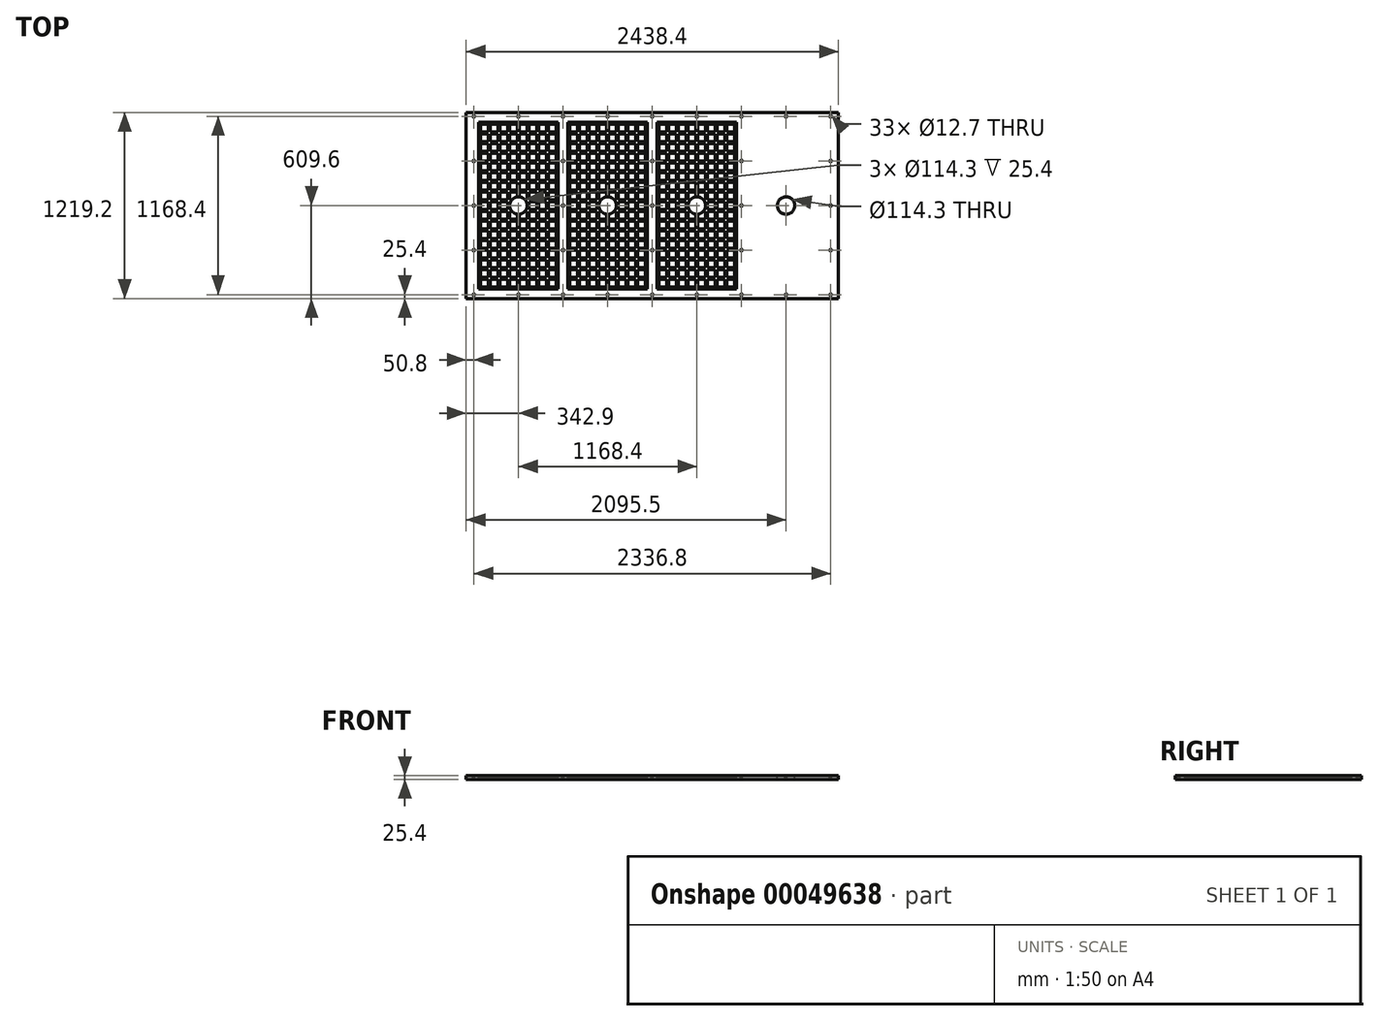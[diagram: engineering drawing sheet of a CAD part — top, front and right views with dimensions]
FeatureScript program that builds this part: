
annotation { "Feature Type Name" : "Feature", "Feature Type Description" : "" }
export const myFeature = defineFeature(function(context is Context, id is Id, definition is map)
    precondition{}
    {
        {
            var Q0;
            Q0=qCreatedBy(makeId("Top.planeOp"),FACE);
            var sketch = newSketch(context, id + "F0", { "sketchPlane" : qUnion([Q0])});
            skLineSegment(sketch, "E0", {"start": v(0, 0) * mm, "end": v(0, 1219.2) * mm});
            skLineSegment(sketch, "E1", {"start": v(0, 1219.2) * mm, "end": v(2438.4, 1219.2) * mm});
            skLineSegment(sketch, "E2", {"start": v(2438.4, 1219.2) * mm, "end": v(2438.4, 0) * mm});
            skLineSegment(sketch, "E3", {"start": v(2438.4, 0) * mm, "end": v(0, 0) * mm});
            skSolve(sketch);
        }
        {
            var Q0;
            Q0=makeQuery(id+"F0.imprint","IMPRINT",FACE,{"disambiguationData":[TD([[makeQuery(id+"F0.imprint","IMPRINT",EDGE,{"derivedFrom":sQuery(id+"F0.wireOp",EDGE,"E0")}),-1.0]])]});
            extrude(context, id + "F1", {"entities" : qUnion([Q0]), "depth" : 25.4 * mm});
        }
        {
            var Q0;
            Q0=makeQuery(id+"F1.opExtrude","CAP_FACE",FACE,{"disambiguationData":[OSD([sQuery(id+"F0.wireOp",EDGE,"E0"),sQuery(id+"F0.wireOp",EDGE,"E1"),sQuery(id+"F0.wireOp",EDGE,"E2"),sQuery(id+"F0.wireOp",EDGE,"E3")])],"isStart":false});
            var sketch = newSketch(context, id + "F2", { "sketchPlane" : qUnion([Q0])});
            skCircle(sketch, "E4", {"center": v(50.8, 1193.8) * mm, "radius": 6.35 * mm});
            skLineSegment(sketch, "E5", {"start": v(50.8, 1193.8) * mm, "end": v(635, 1193.8) * mm, "construction": true});
            skLineSegment(sketch, "E6", {"start": v(635, 1193.8) * mm, "end": v(1219.2, 1193.8) * mm, "construction": true});
            skLineSegment(sketch, "E7", {"start": v(1219.2, 1193.8) * mm, "end": v(1803.4, 1193.8) * mm, "construction": true});
            skLineSegment(sketch, "E8", {"start": v(1803.4, 1193.8) * mm, "end": v(2387.6, 1193.8) * mm, "construction": true});
            skLineSegment(sketch, "E9", {"start": v(2387.6, 1193.8) * mm, "end": v(2387.6, 609.6) * mm, "construction": true});
            skLineSegment(sketch, "E10", {"start": v(2387.6, 609.6) * mm, "end": v(2387.6, 25.4) * mm, "construction": true});
            skLineSegment(sketch, "E11", {"start": v(50.8, 1193.8) * mm, "end": v(0, 1193.8) * mm, "construction": true});
            skLineSegment(sketch, "E12", {"start": v(2387.6, 1193.8) * mm, "end": v(2438.4, 1193.8) * mm, "construction": true});
            skLineSegment(sketch, "E13", {"start": v(2387.6, 1193.8) * mm, "end": v(2387.6, 1219.2) * mm, "construction": true});
            skLineSegment(sketch, "E14", {"start": v(2387.6, 25.4) * mm, "end": v(2387.6, 0) * mm, "construction": true});
            skLineSegment(sketch, "E15", {"start": v(635, 1193.8) * mm, "end": v(635, 609.6) * mm, "construction": true});
            skLineSegment(sketch, "E16", {"start": v(1219.2, 1193.8) * mm, "end": v(1219.2, 609.6) * mm, "construction": true});
            skLineSegment(sketch, "E17", {"start": v(1803.4, 1193.8) * mm, "end": v(1803.4, 609.6) * mm, "construction": true});
            skCircle(sketch, "E18", {"center": v(635, 1193.8) * mm, "radius": 6.35 * mm});
            skCircle(sketch, "E19", {"center": v(342.9, 1193.8) * mm, "radius": 6.35 * mm});
            skCircle(sketch, "E20", {"center": v(927.1, 1193.8) * mm, "radius": 6.35 * mm});
            skCircle(sketch, "E21", {"center": v(1219.2, 1193.8) * mm, "radius": 6.35 * mm});
            skCircle(sketch, "E22", {"center": v(1511.3, 1193.8) * mm, "radius": 6.35 * mm});
            skCircle(sketch, "E23", {"center": v(1803.4, 1193.8) * mm, "radius": 6.35 * mm});
            skCircle(sketch, "E24", {"center": v(2095.5, 1193.8) * mm, "radius": 6.35 * mm});
            skCircle(sketch, "E25", {"center": v(2387.6, 1193.8) * mm, "radius": 6.35 * mm});
            skCircle(sketch, "E26", {"center": v(1803.4, 901.7) * mm, "radius": 6.35 * mm});
            skCircle(sketch, "E27", {"center": v(1219.2, 901.7) * mm, "radius": 6.35 * mm});
            skCircle(sketch, "E28", {"center": v(635, 901.7) * mm, "radius": 6.35 * mm});
            skCircle(sketch, "E29", {"center": v(2387.6, 901.7) * mm, "radius": 6.35 * mm});
            skLineSegment(sketch, "E30", {"start": v(50.8, 1193.8) * mm, "end": v(50.8, 609.6) * mm, "construction": true});
            skLineSegment(sketch, "E31", {"start": v(50.8, 609.6) * mm, "end": v(635, 609.6) * mm, "construction": true});
            skLineSegment(sketch, "E32", {"start": v(1219.2, 609.6) * mm, "end": v(635, 609.6) * mm, "construction": true});
            skLineSegment(sketch, "E33", {"start": v(1219.2, 609.6) * mm, "end": v(1803.4, 609.6) * mm, "construction": true});
            skLineSegment(sketch, "E34", {"start": v(1803.4, 609.6) * mm, "end": v(2387.6, 609.6) * mm, "construction": true});
            skCircle(sketch, "E35", {"center": v(342.9, 609.6) * mm, "radius": 57.15 * mm});
            skCircle(sketch, "E36", {"center": v(927.1, 609.6) * mm, "radius": 57.15 * mm});
            skCircle(sketch, "E37", {"center": v(1511.3, 609.6) * mm, "radius": 57.15 * mm});
            skCircle(sketch, "E38", {"center": v(2095.5, 609.6) * mm, "radius": 57.15 * mm});
            skCircle(sketch, "E39", {"center": v(50.8, 901.7) * mm, "radius": 6.35 * mm});
            skCircle(sketch, "E40.MirrorC", {"center": v(50.8, 317.5) * mm, "radius": 6.35 * mm});
            skCircle(sketch, "E41.MirrorC", {"center": v(50.8, 25.4) * mm, "radius": 6.35 * mm});
            skCircle(sketch, "E42.MirrorC", {"center": v(342.9, 25.4) * mm, "radius": 6.35 * mm});
            skCircle(sketch, "E43.MirrorC", {"center": v(635, 317.5) * mm, "radius": 6.35 * mm});
            skCircle(sketch, "E44.MirrorC", {"center": v(635, 25.4) * mm, "radius": 6.35 * mm});
            skCircle(sketch, "E45.MirrorC", {"center": v(927.1, 25.4) * mm, "radius": 6.35 * mm});
            skCircle(sketch, "E46.MirrorC", {"center": v(1219.2, 25.4) * mm, "radius": 6.35 * mm});
            skCircle(sketch, "E47.MirrorC", {"center": v(1219.2, 317.5) * mm, "radius": 6.35 * mm});
            skCircle(sketch, "E48.MirrorC", {"center": v(1511.3, 25.4) * mm, "radius": 6.35 * mm});
            skCircle(sketch, "E49.MirrorC", {"center": v(1803.4, 25.4) * mm, "radius": 6.35 * mm});
            skCircle(sketch, "E50.MirrorC", {"center": v(1803.4, 317.5) * mm, "radius": 6.35 * mm});
            skCircle(sketch, "E51.MirrorC", {"center": v(2095.5, 25.4) * mm, "radius": 6.35 * mm});
            skCircle(sketch, "E52.MirrorC", {"center": v(2387.6, 25.4) * mm, "radius": 6.35 * mm});
            skCircle(sketch, "E53.MirrorC", {"center": v(2387.6, 317.5) * mm, "radius": 6.35 * mm});
            skCircle(sketch, "E54", {"center": v(50.8, 609.6) * mm, "radius": 6.35 * mm});
            skCircle(sketch, "E55", {"center": v(635, 609.6) * mm, "radius": 6.35 * mm});
            skCircle(sketch, "E56", {"center": v(1219.2, 609.6) * mm, "radius": 6.35 * mm});
            skCircle(sketch, "E57", {"center": v(1803.4, 609.6) * mm, "radius": 6.35 * mm});
            skCircle(sketch, "E58", {"center": v(2387.6, 609.6) * mm, "radius": 6.35 * mm});
            skSolve(sketch);
        }
        {
            var Q0;
            Q0 = qSketchRegion(id + "F2", true);
            extrude(context, id + "F3", {"entities" : qUnion([Q0]), "operationType" : NewBodyOperationType.REMOVE, "endBound" : BoundingType.UP_TO_NEXT, "oppositeDirection" : true, "depth" : 25.4 * mm});
        }
        {
            var Q0;
            Q0=makeQuery(id+"F1.opExtrude","CAP_FACE",FACE,{"disambiguationData":[OSD([sQuery(id+"F0.wireOp",EDGE,"E0"),sQuery(id+"F0.wireOp",EDGE,"E1"),sQuery(id+"F0.wireOp",EDGE,"E2"),sQuery(id+"F0.wireOp",EDGE,"E3")])],"isStart":false});
            var sketch = newSketch(context, id + "F4", { "sketchPlane" : qUnion([Q0])});
            skLineSegment(sketch, "E59", {"start": v(342.9, 1193.8) * mm, "end": v(342.9, 1155.7) * mm, "construction": true});
            skLineSegment(sketch, "E60", {"start": v(603.25, 609.6) * mm, "end": v(635, 609.6) * mm, "construction": true});
            skLineSegment(sketch, "E61", {"start": v(342.9, 25.4) * mm, "end": v(342.9, 63.5) * mm, "construction": true});
            skLineSegment(sketch, "E62", {"start": v(50.8, 609.6) * mm, "end": v(82.55, 609.6) * mm, "construction": true});
            skLineSegment(sketch, "E63.rect.bottom", {"start": v(603.25, 1155.7) * mm, "end": v(82.55, 1155.7) * mm});
            skLineSegment(sketch, "E63.rect.top", {"start": v(603.25, 63.5) * mm, "end": v(82.55, 63.5) * mm});
            skLineSegment(sketch, "E63.rect.left", {"start": v(603.25, 1155.7) * mm, "end": v(603.25, 63.5) * mm});
            skLineSegment(sketch, "E63.rect.right", {"start": v(82.55, 1155.7) * mm, "end": v(82.55, 63.5) * mm});
            skPoint(sketch, "E63.rect.middle", {"position": v(342.9, 609.6) * mm});
            skLineSegment(sketch, "E64.rect.bottom", {"start": v(146.05, 1092.2) * mm, "end": v(95.25, 1092.2) * mm});
            skLineSegment(sketch, "E64.rect.top", {"start": v(146.05, 1143) * mm, "end": v(95.25, 1143) * mm});
            skLineSegment(sketch, "E64.rect.left", {"start": v(146.05, 1092.2) * mm, "end": v(146.05, 1143) * mm});
            skLineSegment(sketch, "E64.rect.right", {"start": v(95.25, 1092.2) * mm, "end": v(95.25, 1143) * mm});
            skPoint(sketch, "E64.rect.middle", {"position": v(120.65, 1117.6) * mm});
            skLineSegment(sketch, "E65.0.1.0", {"start": v(146.05, 1028.7) * mm, "end": v(146.05, 1079.5) * mm});
            skLineSegment(sketch, "E65.0.1.1", {"start": v(146.05, 1079.5) * mm, "end": v(95.25, 1079.5) * mm});
            skLineSegment(sketch, "E65.0.1.2", {"start": v(95.25, 1028.7) * mm, "end": v(95.25, 1079.5) * mm});
            skLineSegment(sketch, "E65.0.1.3", {"start": v(146.05, 1028.7) * mm, "end": v(95.25, 1028.7) * mm});
            skLineSegment(sketch, "E65.0.2.0", {"start": v(146.05, 965.2) * mm, "end": v(146.05, 1016) * mm});
            skLineSegment(sketch, "E65.0.2.1", {"start": v(146.05, 1016) * mm, "end": v(95.25, 1016) * mm});
            skLineSegment(sketch, "E65.0.2.2", {"start": v(95.25, 965.2) * mm, "end": v(95.25, 1016) * mm});
            skLineSegment(sketch, "E65.0.2.3", {"start": v(146.05, 965.2) * mm, "end": v(95.25, 965.2) * mm});
            skLineSegment(sketch, "E65.0.3.0", {"start": v(146.05, 901.7) * mm, "end": v(146.05, 952.5) * mm});
            skLineSegment(sketch, "E65.0.3.1", {"start": v(146.05, 952.5) * mm, "end": v(95.25, 952.5) * mm});
            skLineSegment(sketch, "E65.0.3.2", {"start": v(95.25, 901.7) * mm, "end": v(95.25, 952.5) * mm});
            skLineSegment(sketch, "E65.0.3.3", {"start": v(146.05, 901.7) * mm, "end": v(95.25, 901.7) * mm});
            skLineSegment(sketch, "E65.0.4.0", {"start": v(146.05, 838.2) * mm, "end": v(146.05, 889) * mm});
            skLineSegment(sketch, "E65.0.4.1", {"start": v(146.05, 889) * mm, "end": v(95.25, 889) * mm});
            skLineSegment(sketch, "E65.0.4.2", {"start": v(95.25, 838.2) * mm, "end": v(95.25, 889) * mm});
            skLineSegment(sketch, "E65.0.4.3", {"start": v(146.05, 838.2) * mm, "end": v(95.25, 838.2) * mm});
            skLineSegment(sketch, "E65.0.5.0", {"start": v(146.05, 774.7) * mm, "end": v(146.05, 825.5) * mm});
            skLineSegment(sketch, "E65.0.5.1", {"start": v(146.05, 825.5) * mm, "end": v(95.25, 825.5) * mm});
            skLineSegment(sketch, "E65.0.5.2", {"start": v(95.25, 774.7) * mm, "end": v(95.25, 825.5) * mm});
            skLineSegment(sketch, "E65.0.5.3", {"start": v(146.05, 774.7) * mm, "end": v(95.25, 774.7) * mm});
            skLineSegment(sketch, "E65.0.6.0", {"start": v(146.05, 711.2) * mm, "end": v(146.05, 762) * mm});
            skLineSegment(sketch, "E65.0.6.1", {"start": v(146.05, 762) * mm, "end": v(95.25, 762) * mm});
            skLineSegment(sketch, "E65.0.6.2", {"start": v(95.25, 711.2) * mm, "end": v(95.25, 762) * mm});
            skLineSegment(sketch, "E65.0.6.3", {"start": v(146.05, 711.2) * mm, "end": v(95.25, 711.2) * mm});
            skLineSegment(sketch, "E65.0.7.0", {"start": v(146.05, 647.7) * mm, "end": v(146.05, 698.5) * mm});
            skLineSegment(sketch, "E65.0.7.1", {"start": v(146.05, 698.5) * mm, "end": v(95.25, 698.5) * mm});
            skLineSegment(sketch, "E65.0.7.2", {"start": v(95.25, 647.7) * mm, "end": v(95.25, 698.5) * mm});
            skLineSegment(sketch, "E65.0.7.3", {"start": v(146.05, 647.7) * mm, "end": v(95.25, 647.7) * mm});
            skLineSegment(sketch, "E65.0.8.0", {"start": v(146.05, 584.2) * mm, "end": v(146.05, 635) * mm});
            skLineSegment(sketch, "E65.0.8.1", {"start": v(146.05, 635) * mm, "end": v(95.25, 635) * mm});
            skLineSegment(sketch, "E65.0.8.2", {"start": v(95.25, 584.2) * mm, "end": v(95.25, 635) * mm});
            skLineSegment(sketch, "E65.0.8.3", {"start": v(146.05, 584.2) * mm, "end": v(95.25, 584.2) * mm});
            skLineSegment(sketch, "E65.0.9.0", {"start": v(146.05, 520.7) * mm, "end": v(146.05, 571.5) * mm});
            skLineSegment(sketch, "E65.0.9.1", {"start": v(146.05, 571.5) * mm, "end": v(95.25, 571.5) * mm});
            skLineSegment(sketch, "E65.0.9.2", {"start": v(95.25, 520.7) * mm, "end": v(95.25, 571.5) * mm});
            skLineSegment(sketch, "E65.0.9.3", {"start": v(146.05, 520.7) * mm, "end": v(95.25, 520.7) * mm});
            skLineSegment(sketch, "E65.0.10.0", {"start": v(146.05, 457.2) * mm, "end": v(146.05, 508) * mm});
            skLineSegment(sketch, "E65.0.10.1", {"start": v(146.05, 508) * mm, "end": v(95.25, 508) * mm});
            skLineSegment(sketch, "E65.0.10.2", {"start": v(95.25, 457.2) * mm, "end": v(95.25, 508) * mm});
            skLineSegment(sketch, "E65.0.10.3", {"start": v(146.05, 457.2) * mm, "end": v(95.25, 457.2) * mm});
            skLineSegment(sketch, "E65.0.11.0", {"start": v(146.05, 393.7) * mm, "end": v(146.05, 444.5) * mm});
            skLineSegment(sketch, "E65.0.11.1", {"start": v(146.05, 444.5) * mm, "end": v(95.25, 444.5) * mm});
            skLineSegment(sketch, "E65.0.11.2", {"start": v(95.25, 393.7) * mm, "end": v(95.25, 444.5) * mm});
            skLineSegment(sketch, "E65.0.11.3", {"start": v(146.05, 393.7) * mm, "end": v(95.25, 393.7) * mm});
            skLineSegment(sketch, "E65.0.12.0", {"start": v(146.05, 330.2) * mm, "end": v(146.05, 381) * mm});
            skLineSegment(sketch, "E65.0.12.1", {"start": v(146.05, 381) * mm, "end": v(95.25, 381) * mm});
            skLineSegment(sketch, "E65.0.12.2", {"start": v(95.25, 330.2) * mm, "end": v(95.25, 381) * mm});
            skLineSegment(sketch, "E65.0.12.3", {"start": v(146.05, 330.2) * mm, "end": v(95.25, 330.2) * mm});
            skLineSegment(sketch, "E65.0.13.0", {"start": v(146.05, 266.7) * mm, "end": v(146.05, 317.5) * mm});
            skLineSegment(sketch, "E65.0.13.1", {"start": v(146.05, 317.5) * mm, "end": v(95.25, 317.5) * mm});
            skLineSegment(sketch, "E65.0.13.2", {"start": v(95.25, 266.7) * mm, "end": v(95.25, 317.5) * mm});
            skLineSegment(sketch, "E65.0.13.3", {"start": v(146.05, 266.7) * mm, "end": v(95.25, 266.7) * mm});
            skLineSegment(sketch, "E65.0.14.0", {"start": v(146.05, 203.2) * mm, "end": v(146.05, 254) * mm});
            skLineSegment(sketch, "E65.0.14.1", {"start": v(146.05, 254) * mm, "end": v(95.25, 254) * mm});
            skLineSegment(sketch, "E65.0.14.2", {"start": v(95.25, 203.2) * mm, "end": v(95.25, 254) * mm});
            skLineSegment(sketch, "E65.0.14.3", {"start": v(146.05, 203.2) * mm, "end": v(95.25, 203.2) * mm});
            skLineSegment(sketch, "E65.0.15.0", {"start": v(146.05, 139.7) * mm, "end": v(146.05, 190.5) * mm});
            skLineSegment(sketch, "E65.0.15.1", {"start": v(146.05, 190.5) * mm, "end": v(95.25, 190.5) * mm});
            skLineSegment(sketch, "E65.0.15.2", {"start": v(95.25, 139.7) * mm, "end": v(95.25, 190.5) * mm});
            skLineSegment(sketch, "E65.0.15.3", {"start": v(146.05, 139.7) * mm, "end": v(95.25, 139.7) * mm});
            skLineSegment(sketch, "E65.1.0.0", {"start": v(209.55, 1092.2) * mm, "end": v(209.55, 1143) * mm});
            skLineSegment(sketch, "E65.1.0.1", {"start": v(209.55, 1143) * mm, "end": v(158.75, 1143) * mm});
            skLineSegment(sketch, "E65.1.0.2", {"start": v(158.75, 1092.2) * mm, "end": v(158.75, 1143) * mm});
            skLineSegment(sketch, "E65.1.0.3", {"start": v(209.55, 1092.2) * mm, "end": v(158.75, 1092.2) * mm});
            skLineSegment(sketch, "E65.1.1.0", {"start": v(209.55, 1028.7) * mm, "end": v(209.55, 1079.5) * mm});
            skLineSegment(sketch, "E65.1.1.1", {"start": v(209.55, 1079.5) * mm, "end": v(158.75, 1079.5) * mm});
            skLineSegment(sketch, "E65.1.1.2", {"start": v(158.75, 1028.7) * mm, "end": v(158.75, 1079.5) * mm});
            skLineSegment(sketch, "E65.1.1.3", {"start": v(209.55, 1028.7) * mm, "end": v(158.75, 1028.7) * mm});
            skLineSegment(sketch, "E65.1.2.0", {"start": v(209.55, 965.2) * mm, "end": v(209.55, 1016) * mm});
            skLineSegment(sketch, "E65.1.2.1", {"start": v(209.55, 1016) * mm, "end": v(158.75, 1016) * mm});
            skLineSegment(sketch, "E65.1.2.2", {"start": v(158.75, 965.2) * mm, "end": v(158.75, 1016) * mm});
            skLineSegment(sketch, "E65.1.2.3", {"start": v(209.55, 965.2) * mm, "end": v(158.75, 965.2) * mm});
            skLineSegment(sketch, "E65.1.3.0", {"start": v(209.55, 901.7) * mm, "end": v(209.55, 952.5) * mm});
            skLineSegment(sketch, "E65.1.3.1", {"start": v(209.55, 952.5) * mm, "end": v(158.75, 952.5) * mm});
            skLineSegment(sketch, "E65.1.3.2", {"start": v(158.75, 901.7) * mm, "end": v(158.75, 952.5) * mm});
            skLineSegment(sketch, "E65.1.3.3", {"start": v(209.55, 901.7) * mm, "end": v(158.75, 901.7) * mm});
            skLineSegment(sketch, "E65.1.4.0", {"start": v(209.55, 838.2) * mm, "end": v(209.55, 889) * mm});
            skLineSegment(sketch, "E65.1.4.1", {"start": v(209.55, 889) * mm, "end": v(158.75, 889) * mm});
            skLineSegment(sketch, "E65.1.4.2", {"start": v(158.75, 838.2) * mm, "end": v(158.75, 889) * mm});
            skLineSegment(sketch, "E65.1.4.3", {"start": v(209.55, 838.2) * mm, "end": v(158.75, 838.2) * mm});
            skLineSegment(sketch, "E65.1.5.0", {"start": v(209.55, 774.7) * mm, "end": v(209.55, 825.5) * mm});
            skLineSegment(sketch, "E65.1.5.1", {"start": v(209.55, 825.5) * mm, "end": v(158.75, 825.5) * mm});
            skLineSegment(sketch, "E65.1.5.2", {"start": v(158.75, 774.7) * mm, "end": v(158.75, 825.5) * mm});
            skLineSegment(sketch, "E65.1.5.3", {"start": v(209.55, 774.7) * mm, "end": v(158.75, 774.7) * mm});
            skLineSegment(sketch, "E65.1.6.0", {"start": v(209.55, 711.2) * mm, "end": v(209.55, 762) * mm});
            skLineSegment(sketch, "E65.1.6.1", {"start": v(209.55, 762) * mm, "end": v(158.75, 762) * mm});
            skLineSegment(sketch, "E65.1.6.2", {"start": v(158.75, 711.2) * mm, "end": v(158.75, 762) * mm});
            skLineSegment(sketch, "E65.1.6.3", {"start": v(209.55, 711.2) * mm, "end": v(158.75, 711.2) * mm});
            skLineSegment(sketch, "E65.1.7.0", {"start": v(209.55, 647.7) * mm, "end": v(209.55, 698.5) * mm});
            skLineSegment(sketch, "E65.1.7.1", {"start": v(209.55, 698.5) * mm, "end": v(158.75, 698.5) * mm});
            skLineSegment(sketch, "E65.1.7.2", {"start": v(158.75, 647.7) * mm, "end": v(158.75, 698.5) * mm});
            skLineSegment(sketch, "E65.1.7.3", {"start": v(209.55, 647.7) * mm, "end": v(158.75, 647.7) * mm});
            skLineSegment(sketch, "E65.1.8.0", {"start": v(209.55, 584.2) * mm, "end": v(209.55, 635) * mm});
            skLineSegment(sketch, "E65.1.8.1", {"start": v(209.55, 635) * mm, "end": v(158.75, 635) * mm});
            skLineSegment(sketch, "E65.1.8.2", {"start": v(158.75, 584.2) * mm, "end": v(158.75, 635) * mm});
            skLineSegment(sketch, "E65.1.8.3", {"start": v(209.55, 584.2) * mm, "end": v(158.75, 584.2) * mm});
            skLineSegment(sketch, "E65.1.9.0", {"start": v(209.55, 520.7) * mm, "end": v(209.55, 571.5) * mm});
            skLineSegment(sketch, "E65.1.9.1", {"start": v(209.55, 571.5) * mm, "end": v(158.75, 571.5) * mm});
            skLineSegment(sketch, "E65.1.9.2", {"start": v(158.75, 520.7) * mm, "end": v(158.75, 571.5) * mm});
            skLineSegment(sketch, "E65.1.9.3", {"start": v(209.55, 520.7) * mm, "end": v(158.75, 520.7) * mm});
            skLineSegment(sketch, "E65.1.10.0", {"start": v(209.55, 457.2) * mm, "end": v(209.55, 508) * mm});
            skLineSegment(sketch, "E65.1.10.1", {"start": v(209.55, 508) * mm, "end": v(158.75, 508) * mm});
            skLineSegment(sketch, "E65.1.10.2", {"start": v(158.75, 457.2) * mm, "end": v(158.75, 508) * mm});
            skLineSegment(sketch, "E65.1.10.3", {"start": v(209.55, 457.2) * mm, "end": v(158.75, 457.2) * mm});
            skLineSegment(sketch, "E65.1.11.0", {"start": v(209.55, 393.7) * mm, "end": v(209.55, 444.5) * mm});
            skLineSegment(sketch, "E65.1.11.1", {"start": v(209.55, 444.5) * mm, "end": v(158.75, 444.5) * mm});
            skLineSegment(sketch, "E65.1.11.2", {"start": v(158.75, 393.7) * mm, "end": v(158.75, 444.5) * mm});
            skLineSegment(sketch, "E65.1.11.3", {"start": v(209.55, 393.7) * mm, "end": v(158.75, 393.7) * mm});
            skLineSegment(sketch, "E65.1.12.0", {"start": v(209.55, 330.2) * mm, "end": v(209.55, 381) * mm});
            skLineSegment(sketch, "E65.1.12.1", {"start": v(209.55, 381) * mm, "end": v(158.75, 381) * mm});
            skLineSegment(sketch, "E65.1.12.2", {"start": v(158.75, 330.2) * mm, "end": v(158.75, 381) * mm});
            skLineSegment(sketch, "E65.1.12.3", {"start": v(209.55, 330.2) * mm, "end": v(158.75, 330.2) * mm});
            skLineSegment(sketch, "E65.1.13.0", {"start": v(209.55, 266.7) * mm, "end": v(209.55, 317.5) * mm});
            skLineSegment(sketch, "E65.1.13.1", {"start": v(209.55, 317.5) * mm, "end": v(158.75, 317.5) * mm});
            skLineSegment(sketch, "E65.1.13.2", {"start": v(158.75, 266.7) * mm, "end": v(158.75, 317.5) * mm});
            skLineSegment(sketch, "E65.1.13.3", {"start": v(209.55, 266.7) * mm, "end": v(158.75, 266.7) * mm});
            skLineSegment(sketch, "E65.1.14.0", {"start": v(209.55, 203.2) * mm, "end": v(209.55, 254) * mm});
            skLineSegment(sketch, "E65.1.14.1", {"start": v(209.55, 254) * mm, "end": v(158.75, 254) * mm});
            skLineSegment(sketch, "E65.1.14.2", {"start": v(158.75, 203.2) * mm, "end": v(158.75, 254) * mm});
            skLineSegment(sketch, "E65.1.14.3", {"start": v(209.55, 203.2) * mm, "end": v(158.75, 203.2) * mm});
            skLineSegment(sketch, "E65.1.15.0", {"start": v(209.55, 139.7) * mm, "end": v(209.55, 190.5) * mm});
            skLineSegment(sketch, "E65.1.15.1", {"start": v(209.55, 190.5) * mm, "end": v(158.75, 190.5) * mm});
            skLineSegment(sketch, "E65.1.15.2", {"start": v(158.75, 139.7) * mm, "end": v(158.75, 190.5) * mm});
            skLineSegment(sketch, "E65.1.15.3", {"start": v(209.55, 139.7) * mm, "end": v(158.75, 139.7) * mm});
            skLineSegment(sketch, "E65.2.0.0", {"start": v(273.05, 1092.2) * mm, "end": v(273.05, 1143) * mm});
            skLineSegment(sketch, "E65.2.0.1", {"start": v(273.05, 1143) * mm, "end": v(222.25, 1143) * mm});
            skLineSegment(sketch, "E65.2.0.2", {"start": v(222.25, 1092.2) * mm, "end": v(222.25, 1143) * mm});
            skLineSegment(sketch, "E65.2.0.3", {"start": v(273.05, 1092.2) * mm, "end": v(222.25, 1092.2) * mm});
            skLineSegment(sketch, "E65.2.1.0", {"start": v(273.05, 1028.7) * mm, "end": v(273.05, 1079.5) * mm});
            skLineSegment(sketch, "E65.2.1.1", {"start": v(273.05, 1079.5) * mm, "end": v(222.25, 1079.5) * mm});
            skLineSegment(sketch, "E65.2.1.2", {"start": v(222.25, 1028.7) * mm, "end": v(222.25, 1079.5) * mm});
            skLineSegment(sketch, "E65.2.1.3", {"start": v(273.05, 1028.7) * mm, "end": v(222.25, 1028.7) * mm});
            skLineSegment(sketch, "E65.2.2.0", {"start": v(273.05, 965.2) * mm, "end": v(273.05, 1016) * mm});
            skLineSegment(sketch, "E65.2.2.1", {"start": v(273.05, 1016) * mm, "end": v(222.25, 1016) * mm});
            skLineSegment(sketch, "E65.2.2.2", {"start": v(222.25, 965.2) * mm, "end": v(222.25, 1016) * mm});
            skLineSegment(sketch, "E65.2.2.3", {"start": v(273.05, 965.2) * mm, "end": v(222.25, 965.2) * mm});
            skLineSegment(sketch, "E65.2.3.0", {"start": v(273.05, 901.7) * mm, "end": v(273.05, 952.5) * mm});
            skLineSegment(sketch, "E65.2.3.1", {"start": v(273.05, 952.5) * mm, "end": v(222.25, 952.5) * mm});
            skLineSegment(sketch, "E65.2.3.2", {"start": v(222.25, 901.7) * mm, "end": v(222.25, 952.5) * mm});
            skLineSegment(sketch, "E65.2.3.3", {"start": v(273.05, 901.7) * mm, "end": v(222.25, 901.7) * mm});
            skLineSegment(sketch, "E65.2.4.0", {"start": v(273.05, 838.2) * mm, "end": v(273.05, 889) * mm});
            skLineSegment(sketch, "E65.2.4.1", {"start": v(273.05, 889) * mm, "end": v(222.25, 889) * mm});
            skLineSegment(sketch, "E65.2.4.2", {"start": v(222.25, 838.2) * mm, "end": v(222.25, 889) * mm});
            skLineSegment(sketch, "E65.2.4.3", {"start": v(273.05, 838.2) * mm, "end": v(222.25, 838.2) * mm});
            skLineSegment(sketch, "E65.2.5.0", {"start": v(273.05, 774.7) * mm, "end": v(273.05, 825.5) * mm});
            skLineSegment(sketch, "E65.2.5.1", {"start": v(273.05, 825.5) * mm, "end": v(222.25, 825.5) * mm});
            skLineSegment(sketch, "E65.2.5.2", {"start": v(222.25, 774.7) * mm, "end": v(222.25, 825.5) * mm});
            skLineSegment(sketch, "E65.2.5.3", {"start": v(273.05, 774.7) * mm, "end": v(222.25, 774.7) * mm});
            skLineSegment(sketch, "E65.2.6.0", {"start": v(273.05, 711.2) * mm, "end": v(273.05, 762) * mm});
            skLineSegment(sketch, "E65.2.6.1", {"start": v(273.05, 762) * mm, "end": v(222.25, 762) * mm});
            skLineSegment(sketch, "E65.2.6.2", {"start": v(222.25, 711.2) * mm, "end": v(222.25, 762) * mm});
            skLineSegment(sketch, "E65.2.6.3", {"start": v(273.05, 711.2) * mm, "end": v(222.25, 711.2) * mm});
            skLineSegment(sketch, "E65.2.7.0", {"start": v(273.05, 647.7) * mm, "end": v(273.05, 698.5) * mm});
            skLineSegment(sketch, "E65.2.7.1", {"start": v(273.05, 698.5) * mm, "end": v(222.25, 698.5) * mm});
            skLineSegment(sketch, "E65.2.7.2", {"start": v(222.25, 647.7) * mm, "end": v(222.25, 698.5) * mm});
            skLineSegment(sketch, "E65.2.7.3", {"start": v(273.05, 647.7) * mm, "end": v(222.25, 647.7) * mm});
            skLineSegment(sketch, "E65.2.8.0", {"start": v(273.05, 584.2) * mm, "end": v(273.05, 635) * mm});
            skLineSegment(sketch, "E65.2.8.1", {"start": v(273.05, 635) * mm, "end": v(222.25, 635) * mm});
            skLineSegment(sketch, "E65.2.8.2", {"start": v(222.25, 584.2) * mm, "end": v(222.25, 635) * mm});
            skLineSegment(sketch, "E65.2.8.3", {"start": v(273.05, 584.2) * mm, "end": v(222.25, 584.2) * mm});
            skLineSegment(sketch, "E65.2.9.0", {"start": v(273.05, 520.7) * mm, "end": v(273.05, 571.5) * mm});
            skLineSegment(sketch, "E65.2.9.1", {"start": v(273.05, 571.5) * mm, "end": v(222.25, 571.5) * mm});
            skLineSegment(sketch, "E65.2.9.2", {"start": v(222.25, 520.7) * mm, "end": v(222.25, 571.5) * mm});
            skLineSegment(sketch, "E65.2.9.3", {"start": v(273.05, 520.7) * mm, "end": v(222.25, 520.7) * mm});
            skLineSegment(sketch, "E65.2.10.0", {"start": v(273.05, 457.2) * mm, "end": v(273.05, 508) * mm});
            skLineSegment(sketch, "E65.2.10.1", {"start": v(273.05, 508) * mm, "end": v(222.25, 508) * mm});
            skLineSegment(sketch, "E65.2.10.2", {"start": v(222.25, 457.2) * mm, "end": v(222.25, 508) * mm});
            skLineSegment(sketch, "E65.2.10.3", {"start": v(273.05, 457.2) * mm, "end": v(222.25, 457.2) * mm});
            skLineSegment(sketch, "E65.2.11.0", {"start": v(273.05, 393.7) * mm, "end": v(273.05, 444.5) * mm});
            skLineSegment(sketch, "E65.2.11.1", {"start": v(273.05, 444.5) * mm, "end": v(222.25, 444.5) * mm});
            skLineSegment(sketch, "E65.2.11.2", {"start": v(222.25, 393.7) * mm, "end": v(222.25, 444.5) * mm});
            skLineSegment(sketch, "E65.2.11.3", {"start": v(273.05, 393.7) * mm, "end": v(222.25, 393.7) * mm});
            skLineSegment(sketch, "E65.2.12.0", {"start": v(273.05, 330.2) * mm, "end": v(273.05, 381) * mm});
            skLineSegment(sketch, "E65.2.12.1", {"start": v(273.05, 381) * mm, "end": v(222.25, 381) * mm});
            skLineSegment(sketch, "E65.2.12.2", {"start": v(222.25, 330.2) * mm, "end": v(222.25, 381) * mm});
            skLineSegment(sketch, "E65.2.12.3", {"start": v(273.05, 330.2) * mm, "end": v(222.25, 330.2) * mm});
            skLineSegment(sketch, "E65.2.13.0", {"start": v(273.05, 266.7) * mm, "end": v(273.05, 317.5) * mm});
            skLineSegment(sketch, "E65.2.13.1", {"start": v(273.05, 317.5) * mm, "end": v(222.25, 317.5) * mm});
            skLineSegment(sketch, "E65.2.13.2", {"start": v(222.25, 266.7) * mm, "end": v(222.25, 317.5) * mm});
            skLineSegment(sketch, "E65.2.13.3", {"start": v(273.05, 266.7) * mm, "end": v(222.25, 266.7) * mm});
            skLineSegment(sketch, "E65.2.14.0", {"start": v(273.05, 203.2) * mm, "end": v(273.05, 254) * mm});
            skLineSegment(sketch, "E65.2.14.1", {"start": v(273.05, 254) * mm, "end": v(222.25, 254) * mm});
            skLineSegment(sketch, "E65.2.14.2", {"start": v(222.25, 203.2) * mm, "end": v(222.25, 254) * mm});
            skLineSegment(sketch, "E65.2.14.3", {"start": v(273.05, 203.2) * mm, "end": v(222.25, 203.2) * mm});
            skLineSegment(sketch, "E65.2.15.0", {"start": v(273.05, 139.7) * mm, "end": v(273.05, 190.5) * mm});
            skLineSegment(sketch, "E65.2.15.1", {"start": v(273.05, 190.5) * mm, "end": v(222.25, 190.5) * mm});
            skLineSegment(sketch, "E65.2.15.2", {"start": v(222.25, 139.7) * mm, "end": v(222.25, 190.5) * mm});
            skLineSegment(sketch, "E65.2.15.3", {"start": v(273.05, 139.7) * mm, "end": v(222.25, 139.7) * mm});
            skLineSegment(sketch, "E65.3.0.0", {"start": v(336.54, 1092.2) * mm, "end": v(336.54, 1143) * mm});
            skLineSegment(sketch, "E65.3.0.1", {"start": v(336.54, 1143) * mm, "end": v(285.74, 1143) * mm});
            skLineSegment(sketch, "E65.3.0.2", {"start": v(285.74, 1092.2) * mm, "end": v(285.74, 1143) * mm});
            skLineSegment(sketch, "E65.3.0.3", {"start": v(336.54, 1092.2) * mm, "end": v(285.74, 1092.2) * mm});
            skLineSegment(sketch, "E65.3.1.0", {"start": v(336.54, 1028.7) * mm, "end": v(336.54, 1079.5) * mm});
            skLineSegment(sketch, "E65.3.1.1", {"start": v(336.54, 1079.5) * mm, "end": v(285.74, 1079.5) * mm});
            skLineSegment(sketch, "E65.3.1.2", {"start": v(285.74, 1028.7) * mm, "end": v(285.74, 1079.5) * mm});
            skLineSegment(sketch, "E65.3.1.3", {"start": v(336.54, 1028.7) * mm, "end": v(285.74, 1028.7) * mm});
            skLineSegment(sketch, "E65.3.2.0", {"start": v(336.54, 965.2) * mm, "end": v(336.54, 1016) * mm});
            skLineSegment(sketch, "E65.3.2.1", {"start": v(336.54, 1016) * mm, "end": v(285.74, 1016) * mm});
            skLineSegment(sketch, "E65.3.2.2", {"start": v(285.74, 965.2) * mm, "end": v(285.74, 1016) * mm});
            skLineSegment(sketch, "E65.3.2.3", {"start": v(336.54, 965.2) * mm, "end": v(285.74, 965.2) * mm});
            skLineSegment(sketch, "E65.3.3.0", {"start": v(336.54, 901.7) * mm, "end": v(336.54, 952.5) * mm});
            skLineSegment(sketch, "E65.3.3.1", {"start": v(336.54, 952.5) * mm, "end": v(285.74, 952.5) * mm});
            skLineSegment(sketch, "E65.3.3.2", {"start": v(285.74, 901.7) * mm, "end": v(285.74, 952.5) * mm});
            skLineSegment(sketch, "E65.3.3.3", {"start": v(336.54, 901.7) * mm, "end": v(285.74, 901.7) * mm});
            skLineSegment(sketch, "E65.3.4.0", {"start": v(336.54, 838.2) * mm, "end": v(336.54, 889) * mm});
            skLineSegment(sketch, "E65.3.4.1", {"start": v(336.54, 889) * mm, "end": v(285.74, 889) * mm});
            skLineSegment(sketch, "E65.3.4.2", {"start": v(285.74, 838.2) * mm, "end": v(285.74, 889) * mm});
            skLineSegment(sketch, "E65.3.4.3", {"start": v(336.54, 838.2) * mm, "end": v(285.74, 838.2) * mm});
            skLineSegment(sketch, "E65.3.5.0", {"start": v(336.54, 774.7) * mm, "end": v(336.54, 825.5) * mm});
            skLineSegment(sketch, "E65.3.5.1", {"start": v(336.54, 825.5) * mm, "end": v(285.74, 825.5) * mm});
            skLineSegment(sketch, "E65.3.5.2", {"start": v(285.74, 774.7) * mm, "end": v(285.74, 825.5) * mm});
            skLineSegment(sketch, "E65.3.5.3", {"start": v(336.54, 774.7) * mm, "end": v(285.74, 774.7) * mm});
            skLineSegment(sketch, "E65.3.6.0", {"start": v(336.54, 711.2) * mm, "end": v(336.54, 762) * mm});
            skLineSegment(sketch, "E65.3.6.1", {"start": v(336.54, 762) * mm, "end": v(285.74, 762) * mm});
            skLineSegment(sketch, "E65.3.6.2", {"start": v(285.74, 711.2) * mm, "end": v(285.74, 762) * mm});
            skLineSegment(sketch, "E65.3.6.3", {"start": v(336.54, 711.2) * mm, "end": v(285.74, 711.2) * mm});
            skLineSegment(sketch, "E65.3.7.0", {"start": v(336.54, 647.7) * mm, "end": v(336.54, 698.5) * mm});
            skLineSegment(sketch, "E65.3.7.1", {"start": v(336.54, 698.5) * mm, "end": v(285.74, 698.5) * mm});
            skLineSegment(sketch, "E65.3.7.2", {"start": v(285.74, 647.7) * mm, "end": v(285.74, 698.5) * mm});
            skLineSegment(sketch, "E65.3.7.3", {"start": v(336.54, 647.7) * mm, "end": v(285.74, 647.7) * mm});
            skLineSegment(sketch, "E65.3.8.0", {"start": v(336.54, 584.2) * mm, "end": v(336.54, 635) * mm});
            skLineSegment(sketch, "E65.3.8.1", {"start": v(336.54, 635) * mm, "end": v(285.74, 635) * mm});
            skLineSegment(sketch, "E65.3.8.2", {"start": v(285.74, 584.2) * mm, "end": v(285.74, 635) * mm});
            skLineSegment(sketch, "E65.3.8.3", {"start": v(336.54, 584.2) * mm, "end": v(285.74, 584.2) * mm});
            skLineSegment(sketch, "E65.3.9.0", {"start": v(336.54, 520.7) * mm, "end": v(336.54, 571.5) * mm});
            skLineSegment(sketch, "E65.3.9.1", {"start": v(336.54, 571.5) * mm, "end": v(285.74, 571.5) * mm});
            skLineSegment(sketch, "E65.3.9.2", {"start": v(285.74, 520.7) * mm, "end": v(285.74, 571.5) * mm});
            skLineSegment(sketch, "E65.3.9.3", {"start": v(336.54, 520.7) * mm, "end": v(285.74, 520.7) * mm});
            skLineSegment(sketch, "E65.3.10.0", {"start": v(336.54, 457.2) * mm, "end": v(336.54, 508) * mm});
            skLineSegment(sketch, "E65.3.10.1", {"start": v(336.54, 508) * mm, "end": v(285.74, 508) * mm});
            skLineSegment(sketch, "E65.3.10.2", {"start": v(285.74, 457.2) * mm, "end": v(285.74, 508) * mm});
            skLineSegment(sketch, "E65.3.10.3", {"start": v(336.54, 457.2) * mm, "end": v(285.74, 457.2) * mm});
            skLineSegment(sketch, "E65.3.11.0", {"start": v(336.54, 393.7) * mm, "end": v(336.54, 444.5) * mm});
            skLineSegment(sketch, "E65.3.11.1", {"start": v(336.54, 444.5) * mm, "end": v(285.74, 444.5) * mm});
            skLineSegment(sketch, "E65.3.11.2", {"start": v(285.74, 393.7) * mm, "end": v(285.74, 444.5) * mm});
            skLineSegment(sketch, "E65.3.11.3", {"start": v(336.54, 393.7) * mm, "end": v(285.74, 393.7) * mm});
            skLineSegment(sketch, "E65.3.12.0", {"start": v(336.54, 330.2) * mm, "end": v(336.54, 381) * mm});
            skLineSegment(sketch, "E65.3.12.1", {"start": v(336.54, 381) * mm, "end": v(285.74, 381) * mm});
            skLineSegment(sketch, "E65.3.12.2", {"start": v(285.74, 330.2) * mm, "end": v(285.74, 381) * mm});
            skLineSegment(sketch, "E65.3.12.3", {"start": v(336.54, 330.2) * mm, "end": v(285.74, 330.2) * mm});
            skLineSegment(sketch, "E65.3.13.0", {"start": v(336.54, 266.7) * mm, "end": v(336.54, 317.5) * mm});
            skLineSegment(sketch, "E65.3.13.1", {"start": v(336.54, 317.5) * mm, "end": v(285.74, 317.5) * mm});
            skLineSegment(sketch, "E65.3.13.2", {"start": v(285.74, 266.7) * mm, "end": v(285.74, 317.5) * mm});
            skLineSegment(sketch, "E65.3.13.3", {"start": v(336.54, 266.7) * mm, "end": v(285.74, 266.7) * mm});
            skLineSegment(sketch, "E65.3.14.0", {"start": v(336.54, 203.2) * mm, "end": v(336.54, 254) * mm});
            skLineSegment(sketch, "E65.3.14.1", {"start": v(336.54, 254) * mm, "end": v(285.74, 254) * mm});
            skLineSegment(sketch, "E65.3.14.2", {"start": v(285.74, 203.2) * mm, "end": v(285.74, 254) * mm});
            skLineSegment(sketch, "E65.3.14.3", {"start": v(336.54, 203.2) * mm, "end": v(285.74, 203.2) * mm});
            skLineSegment(sketch, "E65.3.15.0", {"start": v(336.54, 139.7) * mm, "end": v(336.54, 190.5) * mm});
            skLineSegment(sketch, "E65.3.15.1", {"start": v(336.54, 190.5) * mm, "end": v(285.74, 190.5) * mm});
            skLineSegment(sketch, "E65.3.15.2", {"start": v(285.74, 139.7) * mm, "end": v(285.74, 190.5) * mm});
            skLineSegment(sketch, "E65.3.15.3", {"start": v(336.54, 139.7) * mm, "end": v(285.74, 139.7) * mm});
            skLineSegment(sketch, "E65.4.0.0", {"start": v(400.04, 1092.2) * mm, "end": v(400.04, 1143) * mm});
            skLineSegment(sketch, "E65.4.0.1", {"start": v(400.04, 1143) * mm, "end": v(349.24, 1143) * mm});
            skLineSegment(sketch, "E65.4.0.2", {"start": v(349.24, 1092.2) * mm, "end": v(349.24, 1143) * mm});
            skLineSegment(sketch, "E65.4.0.3", {"start": v(400.04, 1092.2) * mm, "end": v(349.24, 1092.2) * mm});
            skLineSegment(sketch, "E65.4.1.0", {"start": v(400.04, 1028.7) * mm, "end": v(400.04, 1079.5) * mm});
            skLineSegment(sketch, "E65.4.1.1", {"start": v(400.04, 1079.5) * mm, "end": v(349.24, 1079.5) * mm});
            skLineSegment(sketch, "E65.4.1.2", {"start": v(349.24, 1028.7) * mm, "end": v(349.24, 1079.5) * mm});
            skLineSegment(sketch, "E65.4.1.3", {"start": v(400.04, 1028.7) * mm, "end": v(349.24, 1028.7) * mm});
            skLineSegment(sketch, "E65.4.2.0", {"start": v(400.04, 965.2) * mm, "end": v(400.04, 1016) * mm});
            skLineSegment(sketch, "E65.4.2.1", {"start": v(400.04, 1016) * mm, "end": v(349.24, 1016) * mm});
            skLineSegment(sketch, "E65.4.2.2", {"start": v(349.24, 965.2) * mm, "end": v(349.24, 1016) * mm});
            skLineSegment(sketch, "E65.4.2.3", {"start": v(400.04, 965.2) * mm, "end": v(349.24, 965.2) * mm});
            skLineSegment(sketch, "E65.4.3.0", {"start": v(400.04, 901.7) * mm, "end": v(400.04, 952.5) * mm});
            skLineSegment(sketch, "E65.4.3.1", {"start": v(400.04, 952.5) * mm, "end": v(349.24, 952.5) * mm});
            skLineSegment(sketch, "E65.4.3.2", {"start": v(349.24, 901.7) * mm, "end": v(349.24, 952.5) * mm});
            skLineSegment(sketch, "E65.4.3.3", {"start": v(400.04, 901.7) * mm, "end": v(349.24, 901.7) * mm});
            skLineSegment(sketch, "E65.4.4.0", {"start": v(400.04, 838.2) * mm, "end": v(400.04, 889) * mm});
            skLineSegment(sketch, "E65.4.4.1", {"start": v(400.04, 889) * mm, "end": v(349.24, 889) * mm});
            skLineSegment(sketch, "E65.4.4.2", {"start": v(349.24, 838.2) * mm, "end": v(349.24, 889) * mm});
            skLineSegment(sketch, "E65.4.4.3", {"start": v(400.04, 838.2) * mm, "end": v(349.24, 838.2) * mm});
            skLineSegment(sketch, "E65.4.5.0", {"start": v(400.04, 774.7) * mm, "end": v(400.04, 825.5) * mm});
            skLineSegment(sketch, "E65.4.5.1", {"start": v(400.04, 825.5) * mm, "end": v(349.24, 825.5) * mm});
            skLineSegment(sketch, "E65.4.5.2", {"start": v(349.24, 774.7) * mm, "end": v(349.24, 825.5) * mm});
            skLineSegment(sketch, "E65.4.5.3", {"start": v(400.04, 774.7) * mm, "end": v(349.24, 774.7) * mm});
            skLineSegment(sketch, "E65.4.6.0", {"start": v(400.04, 711.2) * mm, "end": v(400.04, 762) * mm});
            skLineSegment(sketch, "E65.4.6.1", {"start": v(400.04, 762) * mm, "end": v(349.24, 762) * mm});
            skLineSegment(sketch, "E65.4.6.2", {"start": v(349.24, 711.2) * mm, "end": v(349.24, 762) * mm});
            skLineSegment(sketch, "E65.4.6.3", {"start": v(400.04, 711.2) * mm, "end": v(349.24, 711.2) * mm});
            skLineSegment(sketch, "E65.4.7.0", {"start": v(400.04, 647.7) * mm, "end": v(400.04, 698.5) * mm});
            skLineSegment(sketch, "E65.4.7.1", {"start": v(400.04, 698.5) * mm, "end": v(349.24, 698.5) * mm});
            skLineSegment(sketch, "E65.4.7.2", {"start": v(349.24, 647.7) * mm, "end": v(349.24, 698.5) * mm});
            skLineSegment(sketch, "E65.4.7.3", {"start": v(400.04, 647.7) * mm, "end": v(349.24, 647.7) * mm});
            skLineSegment(sketch, "E65.4.8.0", {"start": v(400.04, 584.2) * mm, "end": v(400.04, 635) * mm});
            skLineSegment(sketch, "E65.4.8.1", {"start": v(400.04, 635) * mm, "end": v(349.24, 635) * mm});
            skLineSegment(sketch, "E65.4.8.2", {"start": v(349.24, 584.2) * mm, "end": v(349.24, 635) * mm});
            skLineSegment(sketch, "E65.4.8.3", {"start": v(400.04, 584.2) * mm, "end": v(349.24, 584.2) * mm});
            skLineSegment(sketch, "E65.4.9.0", {"start": v(400.04, 520.7) * mm, "end": v(400.04, 571.5) * mm});
            skLineSegment(sketch, "E65.4.9.1", {"start": v(400.04, 571.5) * mm, "end": v(349.24, 571.5) * mm});
            skLineSegment(sketch, "E65.4.9.2", {"start": v(349.24, 520.7) * mm, "end": v(349.24, 571.5) * mm});
            skLineSegment(sketch, "E65.4.9.3", {"start": v(400.04, 520.7) * mm, "end": v(349.24, 520.7) * mm});
            skLineSegment(sketch, "E65.4.10.0", {"start": v(400.04, 457.2) * mm, "end": v(400.04, 508) * mm});
            skLineSegment(sketch, "E65.4.10.1", {"start": v(400.04, 508) * mm, "end": v(349.24, 508) * mm});
            skLineSegment(sketch, "E65.4.10.2", {"start": v(349.24, 457.2) * mm, "end": v(349.24, 508) * mm});
            skLineSegment(sketch, "E65.4.10.3", {"start": v(400.04, 457.2) * mm, "end": v(349.24, 457.2) * mm});
            skLineSegment(sketch, "E65.4.11.0", {"start": v(400.04, 393.7) * mm, "end": v(400.04, 444.5) * mm});
            skLineSegment(sketch, "E65.4.11.1", {"start": v(400.04, 444.5) * mm, "end": v(349.24, 444.5) * mm});
            skLineSegment(sketch, "E65.4.11.2", {"start": v(349.24, 393.7) * mm, "end": v(349.24, 444.5) * mm});
            skLineSegment(sketch, "E65.4.11.3", {"start": v(400.04, 393.7) * mm, "end": v(349.24, 393.7) * mm});
            skLineSegment(sketch, "E65.4.12.0", {"start": v(400.04, 330.2) * mm, "end": v(400.04, 381) * mm});
            skLineSegment(sketch, "E65.4.12.1", {"start": v(400.04, 381) * mm, "end": v(349.24, 381) * mm});
            skLineSegment(sketch, "E65.4.12.2", {"start": v(349.24, 330.2) * mm, "end": v(349.24, 381) * mm});
            skLineSegment(sketch, "E65.4.12.3", {"start": v(400.04, 330.2) * mm, "end": v(349.24, 330.2) * mm});
            skLineSegment(sketch, "E65.4.13.0", {"start": v(400.04, 266.7) * mm, "end": v(400.04, 317.5) * mm});
            skLineSegment(sketch, "E65.4.13.1", {"start": v(400.04, 317.5) * mm, "end": v(349.24, 317.5) * mm});
            skLineSegment(sketch, "E65.4.13.2", {"start": v(349.24, 266.7) * mm, "end": v(349.24, 317.5) * mm});
            skLineSegment(sketch, "E65.4.13.3", {"start": v(400.04, 266.7) * mm, "end": v(349.24, 266.7) * mm});
            skLineSegment(sketch, "E65.4.14.0", {"start": v(400.04, 203.2) * mm, "end": v(400.04, 254) * mm});
            skLineSegment(sketch, "E65.4.14.1", {"start": v(400.04, 254) * mm, "end": v(349.24, 254) * mm});
            skLineSegment(sketch, "E65.4.14.2", {"start": v(349.24, 203.2) * mm, "end": v(349.24, 254) * mm});
            skLineSegment(sketch, "E65.4.14.3", {"start": v(400.04, 203.2) * mm, "end": v(349.24, 203.2) * mm});
            skLineSegment(sketch, "E65.4.15.0", {"start": v(400.04, 139.7) * mm, "end": v(400.04, 190.5) * mm});
            skLineSegment(sketch, "E65.4.15.1", {"start": v(400.04, 190.5) * mm, "end": v(349.24, 190.5) * mm});
            skLineSegment(sketch, "E65.4.15.2", {"start": v(349.24, 139.7) * mm, "end": v(349.24, 190.5) * mm});
            skLineSegment(sketch, "E65.4.15.3", {"start": v(400.04, 139.7) * mm, "end": v(349.24, 139.7) * mm});
            skLineSegment(sketch, "E65.5.0.0", {"start": v(463.54, 1092.2) * mm, "end": v(463.54, 1143) * mm});
            skLineSegment(sketch, "E65.5.0.1", {"start": v(463.54, 1143) * mm, "end": v(412.74, 1143) * mm});
            skLineSegment(sketch, "E65.5.0.2", {"start": v(412.74, 1092.2) * mm, "end": v(412.74, 1143) * mm});
            skLineSegment(sketch, "E65.5.0.3", {"start": v(463.54, 1092.2) * mm, "end": v(412.74, 1092.2) * mm});
            skLineSegment(sketch, "E65.5.1.0", {"start": v(463.54, 1028.7) * mm, "end": v(463.54, 1079.5) * mm});
            skLineSegment(sketch, "E65.5.1.1", {"start": v(463.54, 1079.5) * mm, "end": v(412.74, 1079.5) * mm});
            skLineSegment(sketch, "E65.5.1.2", {"start": v(412.74, 1028.7) * mm, "end": v(412.74, 1079.5) * mm});
            skLineSegment(sketch, "E65.5.1.3", {"start": v(463.54, 1028.7) * mm, "end": v(412.74, 1028.7) * mm});
            skLineSegment(sketch, "E65.5.2.0", {"start": v(463.54, 965.2) * mm, "end": v(463.54, 1016) * mm});
            skLineSegment(sketch, "E65.5.2.1", {"start": v(463.54, 1016) * mm, "end": v(412.74, 1016) * mm});
            skLineSegment(sketch, "E65.5.2.2", {"start": v(412.74, 965.2) * mm, "end": v(412.74, 1016) * mm});
            skLineSegment(sketch, "E65.5.2.3", {"start": v(463.54, 965.2) * mm, "end": v(412.74, 965.2) * mm});
            skLineSegment(sketch, "E65.5.3.0", {"start": v(463.54, 901.7) * mm, "end": v(463.54, 952.5) * mm});
            skLineSegment(sketch, "E65.5.3.1", {"start": v(463.54, 952.5) * mm, "end": v(412.74, 952.5) * mm});
            skLineSegment(sketch, "E65.5.3.2", {"start": v(412.74, 901.7) * mm, "end": v(412.74, 952.5) * mm});
            skLineSegment(sketch, "E65.5.3.3", {"start": v(463.54, 901.7) * mm, "end": v(412.74, 901.7) * mm});
            skLineSegment(sketch, "E65.5.4.0", {"start": v(463.54, 838.2) * mm, "end": v(463.54, 889) * mm});
            skLineSegment(sketch, "E65.5.4.1", {"start": v(463.54, 889) * mm, "end": v(412.74, 889) * mm});
            skLineSegment(sketch, "E65.5.4.2", {"start": v(412.74, 838.2) * mm, "end": v(412.74, 889) * mm});
            skLineSegment(sketch, "E65.5.4.3", {"start": v(463.54, 838.2) * mm, "end": v(412.74, 838.2) * mm});
            skLineSegment(sketch, "E65.5.5.0", {"start": v(463.54, 774.7) * mm, "end": v(463.54, 825.5) * mm});
            skLineSegment(sketch, "E65.5.5.1", {"start": v(463.54, 825.5) * mm, "end": v(412.74, 825.5) * mm});
            skLineSegment(sketch, "E65.5.5.2", {"start": v(412.74, 774.7) * mm, "end": v(412.74, 825.5) * mm});
            skLineSegment(sketch, "E65.5.5.3", {"start": v(463.54, 774.7) * mm, "end": v(412.74, 774.7) * mm});
            skLineSegment(sketch, "E65.5.6.0", {"start": v(463.54, 711.2) * mm, "end": v(463.54, 762) * mm});
            skLineSegment(sketch, "E65.5.6.1", {"start": v(463.54, 762) * mm, "end": v(412.74, 762) * mm});
            skLineSegment(sketch, "E65.5.6.2", {"start": v(412.74, 711.2) * mm, "end": v(412.74, 762) * mm});
            skLineSegment(sketch, "E65.5.6.3", {"start": v(463.54, 711.2) * mm, "end": v(412.74, 711.2) * mm});
            skLineSegment(sketch, "E65.5.7.0", {"start": v(463.54, 647.7) * mm, "end": v(463.54, 698.5) * mm});
            skLineSegment(sketch, "E65.5.7.1", {"start": v(463.54, 698.5) * mm, "end": v(412.74, 698.5) * mm});
            skLineSegment(sketch, "E65.5.7.2", {"start": v(412.74, 647.7) * mm, "end": v(412.74, 698.5) * mm});
            skLineSegment(sketch, "E65.5.7.3", {"start": v(463.54, 647.7) * mm, "end": v(412.74, 647.7) * mm});
            skLineSegment(sketch, "E65.5.8.0", {"start": v(463.54, 584.2) * mm, "end": v(463.54, 635) * mm});
            skLineSegment(sketch, "E65.5.8.1", {"start": v(463.54, 635) * mm, "end": v(412.74, 635) * mm});
            skLineSegment(sketch, "E65.5.8.2", {"start": v(412.74, 584.2) * mm, "end": v(412.74, 635) * mm});
            skLineSegment(sketch, "E65.5.8.3", {"start": v(463.54, 584.2) * mm, "end": v(412.74, 584.2) * mm});
            skLineSegment(sketch, "E65.5.9.0", {"start": v(463.54, 520.7) * mm, "end": v(463.54, 571.5) * mm});
            skLineSegment(sketch, "E65.5.9.1", {"start": v(463.54, 571.5) * mm, "end": v(412.74, 571.5) * mm});
            skLineSegment(sketch, "E65.5.9.2", {"start": v(412.74, 520.7) * mm, "end": v(412.74, 571.5) * mm});
            skLineSegment(sketch, "E65.5.9.3", {"start": v(463.54, 520.7) * mm, "end": v(412.74, 520.7) * mm});
            skLineSegment(sketch, "E65.5.10.0", {"start": v(463.54, 457.2) * mm, "end": v(463.54, 508) * mm});
            skLineSegment(sketch, "E65.5.10.1", {"start": v(463.54, 508) * mm, "end": v(412.74, 508) * mm});
            skLineSegment(sketch, "E65.5.10.2", {"start": v(412.74, 457.2) * mm, "end": v(412.74, 508) * mm});
            skLineSegment(sketch, "E65.5.10.3", {"start": v(463.54, 457.2) * mm, "end": v(412.74, 457.2) * mm});
            skLineSegment(sketch, "E65.5.11.0", {"start": v(463.54, 393.7) * mm, "end": v(463.54, 444.5) * mm});
            skLineSegment(sketch, "E65.5.11.1", {"start": v(463.54, 444.5) * mm, "end": v(412.74, 444.5) * mm});
            skLineSegment(sketch, "E65.5.11.2", {"start": v(412.74, 393.7) * mm, "end": v(412.74, 444.5) * mm});
            skLineSegment(sketch, "E65.5.11.3", {"start": v(463.54, 393.7) * mm, "end": v(412.74, 393.7) * mm});
            skLineSegment(sketch, "E65.5.12.0", {"start": v(463.54, 330.2) * mm, "end": v(463.54, 381) * mm});
            skLineSegment(sketch, "E65.5.12.1", {"start": v(463.54, 381) * mm, "end": v(412.74, 381) * mm});
            skLineSegment(sketch, "E65.5.12.2", {"start": v(412.74, 330.2) * mm, "end": v(412.74, 381) * mm});
            skLineSegment(sketch, "E65.5.12.3", {"start": v(463.54, 330.2) * mm, "end": v(412.74, 330.2) * mm});
            skLineSegment(sketch, "E65.5.13.0", {"start": v(463.54, 266.7) * mm, "end": v(463.54, 317.5) * mm});
            skLineSegment(sketch, "E65.5.13.1", {"start": v(463.54, 317.5) * mm, "end": v(412.74, 317.5) * mm});
            skLineSegment(sketch, "E65.5.13.2", {"start": v(412.74, 266.7) * mm, "end": v(412.74, 317.5) * mm});
            skLineSegment(sketch, "E65.5.13.3", {"start": v(463.54, 266.7) * mm, "end": v(412.74, 266.7) * mm});
            skLineSegment(sketch, "E65.5.14.0", {"start": v(463.54, 203.2) * mm, "end": v(463.54, 254) * mm});
            skLineSegment(sketch, "E65.5.14.1", {"start": v(463.54, 254) * mm, "end": v(412.74, 254) * mm});
            skLineSegment(sketch, "E65.5.14.2", {"start": v(412.74, 203.2) * mm, "end": v(412.74, 254) * mm});
            skLineSegment(sketch, "E65.5.14.3", {"start": v(463.54, 203.2) * mm, "end": v(412.74, 203.2) * mm});
            skLineSegment(sketch, "E65.5.15.0", {"start": v(463.54, 139.7) * mm, "end": v(463.54, 190.5) * mm});
            skLineSegment(sketch, "E65.5.15.1", {"start": v(463.54, 190.5) * mm, "end": v(412.74, 190.5) * mm});
            skLineSegment(sketch, "E65.5.15.2", {"start": v(412.74, 139.7) * mm, "end": v(412.74, 190.5) * mm});
            skLineSegment(sketch, "E65.5.15.3", {"start": v(463.54, 139.7) * mm, "end": v(412.74, 139.7) * mm});
            skLineSegment(sketch, "E65.6.0.0", {"start": v(527.04, 1092.2) * mm, "end": v(527.04, 1143) * mm});
            skLineSegment(sketch, "E65.6.0.1", {"start": v(527.04, 1143) * mm, "end": v(476.24, 1143) * mm});
            skLineSegment(sketch, "E65.6.0.2", {"start": v(476.24, 1092.2) * mm, "end": v(476.24, 1143) * mm});
            skLineSegment(sketch, "E65.6.0.3", {"start": v(527.04, 1092.2) * mm, "end": v(476.24, 1092.2) * mm});
            skLineSegment(sketch, "E65.6.1.0", {"start": v(527.04, 1028.7) * mm, "end": v(527.04, 1079.5) * mm});
            skLineSegment(sketch, "E65.6.1.1", {"start": v(527.04, 1079.5) * mm, "end": v(476.24, 1079.5) * mm});
            skLineSegment(sketch, "E65.6.1.2", {"start": v(476.24, 1028.7) * mm, "end": v(476.24, 1079.5) * mm});
            skLineSegment(sketch, "E65.6.1.3", {"start": v(527.04, 1028.7) * mm, "end": v(476.24, 1028.7) * mm});
            skLineSegment(sketch, "E65.6.2.0", {"start": v(527.04, 965.2) * mm, "end": v(527.04, 1016) * mm});
            skLineSegment(sketch, "E65.6.2.1", {"start": v(527.04, 1016) * mm, "end": v(476.24, 1016) * mm});
            skLineSegment(sketch, "E65.6.2.2", {"start": v(476.24, 965.2) * mm, "end": v(476.24, 1016) * mm});
            skLineSegment(sketch, "E65.6.2.3", {"start": v(527.04, 965.2) * mm, "end": v(476.24, 965.2) * mm});
            skLineSegment(sketch, "E65.6.3.0", {"start": v(527.04, 901.7) * mm, "end": v(527.04, 952.5) * mm});
            skLineSegment(sketch, "E65.6.3.1", {"start": v(527.04, 952.5) * mm, "end": v(476.24, 952.5) * mm});
            skLineSegment(sketch, "E65.6.3.2", {"start": v(476.24, 901.7) * mm, "end": v(476.24, 952.5) * mm});
            skLineSegment(sketch, "E65.6.3.3", {"start": v(527.04, 901.7) * mm, "end": v(476.24, 901.7) * mm});
            skLineSegment(sketch, "E65.6.4.0", {"start": v(527.04, 838.2) * mm, "end": v(527.04, 889) * mm});
            skLineSegment(sketch, "E65.6.4.1", {"start": v(527.04, 889) * mm, "end": v(476.24, 889) * mm});
            skLineSegment(sketch, "E65.6.4.2", {"start": v(476.24, 838.2) * mm, "end": v(476.24, 889) * mm});
            skLineSegment(sketch, "E65.6.4.3", {"start": v(527.04, 838.2) * mm, "end": v(476.24, 838.2) * mm});
            skLineSegment(sketch, "E65.6.5.0", {"start": v(527.04, 774.7) * mm, "end": v(527.04, 825.5) * mm});
            skLineSegment(sketch, "E65.6.5.1", {"start": v(527.04, 825.5) * mm, "end": v(476.24, 825.5) * mm});
            skLineSegment(sketch, "E65.6.5.2", {"start": v(476.24, 774.7) * mm, "end": v(476.24, 825.5) * mm});
            skLineSegment(sketch, "E65.6.5.3", {"start": v(527.04, 774.7) * mm, "end": v(476.24, 774.7) * mm});
            skLineSegment(sketch, "E65.6.6.0", {"start": v(527.04, 711.2) * mm, "end": v(527.04, 762) * mm});
            skLineSegment(sketch, "E65.6.6.1", {"start": v(527.04, 762) * mm, "end": v(476.24, 762) * mm});
            skLineSegment(sketch, "E65.6.6.2", {"start": v(476.24, 711.2) * mm, "end": v(476.24, 762) * mm});
            skLineSegment(sketch, "E65.6.6.3", {"start": v(527.04, 711.2) * mm, "end": v(476.24, 711.2) * mm});
            skLineSegment(sketch, "E65.6.7.0", {"start": v(527.04, 647.7) * mm, "end": v(527.04, 698.5) * mm});
            skLineSegment(sketch, "E65.6.7.1", {"start": v(527.04, 698.5) * mm, "end": v(476.24, 698.5) * mm});
            skLineSegment(sketch, "E65.6.7.2", {"start": v(476.24, 647.7) * mm, "end": v(476.24, 698.5) * mm});
            skLineSegment(sketch, "E65.6.7.3", {"start": v(527.04, 647.7) * mm, "end": v(476.24, 647.7) * mm});
            skLineSegment(sketch, "E65.6.8.0", {"start": v(527.04, 584.2) * mm, "end": v(527.04, 635) * mm});
            skLineSegment(sketch, "E65.6.8.1", {"start": v(527.04, 635) * mm, "end": v(476.24, 635) * mm});
            skLineSegment(sketch, "E65.6.8.2", {"start": v(476.24, 584.2) * mm, "end": v(476.24, 635) * mm});
            skLineSegment(sketch, "E65.6.8.3", {"start": v(527.04, 584.2) * mm, "end": v(476.24, 584.2) * mm});
            skLineSegment(sketch, "E65.6.9.0", {"start": v(527.04, 520.7) * mm, "end": v(527.04, 571.5) * mm});
            skLineSegment(sketch, "E65.6.9.1", {"start": v(527.04, 571.5) * mm, "end": v(476.24, 571.5) * mm});
            skLineSegment(sketch, "E65.6.9.2", {"start": v(476.24, 520.7) * mm, "end": v(476.24, 571.5) * mm});
            skLineSegment(sketch, "E65.6.9.3", {"start": v(527.04, 520.7) * mm, "end": v(476.24, 520.7) * mm});
            skLineSegment(sketch, "E65.6.10.0", {"start": v(527.04, 457.2) * mm, "end": v(527.04, 508) * mm});
            skLineSegment(sketch, "E65.6.10.1", {"start": v(527.04, 508) * mm, "end": v(476.24, 508) * mm});
            skLineSegment(sketch, "E65.6.10.2", {"start": v(476.24, 457.2) * mm, "end": v(476.24, 508) * mm});
            skLineSegment(sketch, "E65.6.10.3", {"start": v(527.04, 457.2) * mm, "end": v(476.24, 457.2) * mm});
            skLineSegment(sketch, "E65.6.11.0", {"start": v(527.04, 393.7) * mm, "end": v(527.04, 444.5) * mm});
            skLineSegment(sketch, "E65.6.11.1", {"start": v(527.04, 444.5) * mm, "end": v(476.24, 444.5) * mm});
            skLineSegment(sketch, "E65.6.11.2", {"start": v(476.24, 393.7) * mm, "end": v(476.24, 444.5) * mm});
            skLineSegment(sketch, "E65.6.11.3", {"start": v(527.04, 393.7) * mm, "end": v(476.24, 393.7) * mm});
            skLineSegment(sketch, "E65.6.12.0", {"start": v(527.04, 330.2) * mm, "end": v(527.04, 381) * mm});
            skLineSegment(sketch, "E65.6.12.1", {"start": v(527.04, 381) * mm, "end": v(476.24, 381) * mm});
            skLineSegment(sketch, "E65.6.12.2", {"start": v(476.24, 330.2) * mm, "end": v(476.24, 381) * mm});
            skLineSegment(sketch, "E65.6.12.3", {"start": v(527.04, 330.2) * mm, "end": v(476.24, 330.2) * mm});
            skLineSegment(sketch, "E65.6.13.0", {"start": v(527.04, 266.7) * mm, "end": v(527.04, 317.5) * mm});
            skLineSegment(sketch, "E65.6.13.1", {"start": v(527.04, 317.5) * mm, "end": v(476.24, 317.5) * mm});
            skLineSegment(sketch, "E65.6.13.2", {"start": v(476.24, 266.7) * mm, "end": v(476.24, 317.5) * mm});
            skLineSegment(sketch, "E65.6.13.3", {"start": v(527.04, 266.7) * mm, "end": v(476.24, 266.7) * mm});
            skLineSegment(sketch, "E65.6.14.0", {"start": v(527.04, 203.2) * mm, "end": v(527.04, 254) * mm});
            skLineSegment(sketch, "E65.6.14.1", {"start": v(527.04, 254) * mm, "end": v(476.24, 254) * mm});
            skLineSegment(sketch, "E65.6.14.2", {"start": v(476.24, 203.2) * mm, "end": v(476.24, 254) * mm});
            skLineSegment(sketch, "E65.6.14.3", {"start": v(527.04, 203.2) * mm, "end": v(476.24, 203.2) * mm});
            skLineSegment(sketch, "E65.6.15.0", {"start": v(527.04, 139.7) * mm, "end": v(527.04, 190.5) * mm});
            skLineSegment(sketch, "E65.6.15.1", {"start": v(527.04, 190.5) * mm, "end": v(476.24, 190.5) * mm});
            skLineSegment(sketch, "E65.6.15.2", {"start": v(476.24, 139.7) * mm, "end": v(476.24, 190.5) * mm});
            skLineSegment(sketch, "E65.6.15.3", {"start": v(527.04, 139.7) * mm, "end": v(476.24, 139.7) * mm});
            skLineSegment(sketch, "E65.7.0.0", {"start": v(590.53, 1092.2) * mm, "end": v(590.53, 1143) * mm});
            skLineSegment(sketch, "E65.7.0.1", {"start": v(590.53, 1143) * mm, "end": v(539.73, 1143) * mm});
            skLineSegment(sketch, "E65.7.0.2", {"start": v(539.73, 1092.2) * mm, "end": v(539.73, 1143) * mm});
            skLineSegment(sketch, "E65.7.0.3", {"start": v(590.53, 1092.2) * mm, "end": v(539.73, 1092.2) * mm});
            skLineSegment(sketch, "E65.7.1.0", {"start": v(590.53, 1028.7) * mm, "end": v(590.53, 1079.5) * mm});
            skLineSegment(sketch, "E65.7.1.1", {"start": v(590.53, 1079.5) * mm, "end": v(539.73, 1079.5) * mm});
            skLineSegment(sketch, "E65.7.1.2", {"start": v(539.73, 1028.7) * mm, "end": v(539.73, 1079.5) * mm});
            skLineSegment(sketch, "E65.7.1.3", {"start": v(590.53, 1028.7) * mm, "end": v(539.73, 1028.7) * mm});
            skLineSegment(sketch, "E65.7.2.0", {"start": v(590.53, 965.2) * mm, "end": v(590.53, 1016) * mm});
            skLineSegment(sketch, "E65.7.2.1", {"start": v(590.53, 1016) * mm, "end": v(539.73, 1016) * mm});
            skLineSegment(sketch, "E65.7.2.2", {"start": v(539.73, 965.2) * mm, "end": v(539.73, 1016) * mm});
            skLineSegment(sketch, "E65.7.2.3", {"start": v(590.53, 965.2) * mm, "end": v(539.73, 965.2) * mm});
            skLineSegment(sketch, "E65.7.3.0", {"start": v(590.53, 901.7) * mm, "end": v(590.53, 952.5) * mm});
            skLineSegment(sketch, "E65.7.3.1", {"start": v(590.53, 952.5) * mm, "end": v(539.73, 952.5) * mm});
            skLineSegment(sketch, "E65.7.3.2", {"start": v(539.73, 901.7) * mm, "end": v(539.73, 952.5) * mm});
            skLineSegment(sketch, "E65.7.3.3", {"start": v(590.53, 901.7) * mm, "end": v(539.73, 901.7) * mm});
            skLineSegment(sketch, "E65.7.4.0", {"start": v(590.53, 838.2) * mm, "end": v(590.53, 889) * mm});
            skLineSegment(sketch, "E65.7.4.1", {"start": v(590.53, 889) * mm, "end": v(539.73, 889) * mm});
            skLineSegment(sketch, "E65.7.4.2", {"start": v(539.73, 838.2) * mm, "end": v(539.73, 889) * mm});
            skLineSegment(sketch, "E65.7.4.3", {"start": v(590.53, 838.2) * mm, "end": v(539.73, 838.2) * mm});
            skLineSegment(sketch, "E65.7.5.0", {"start": v(590.53, 774.7) * mm, "end": v(590.53, 825.5) * mm});
            skLineSegment(sketch, "E65.7.5.1", {"start": v(590.53, 825.5) * mm, "end": v(539.73, 825.5) * mm});
            skLineSegment(sketch, "E65.7.5.2", {"start": v(539.73, 774.7) * mm, "end": v(539.73, 825.5) * mm});
            skLineSegment(sketch, "E65.7.5.3", {"start": v(590.53, 774.7) * mm, "end": v(539.73, 774.7) * mm});
            skLineSegment(sketch, "E65.7.6.0", {"start": v(590.53, 711.2) * mm, "end": v(590.53, 762) * mm});
            skLineSegment(sketch, "E65.7.6.1", {"start": v(590.53, 762) * mm, "end": v(539.73, 762) * mm});
            skLineSegment(sketch, "E65.7.6.2", {"start": v(539.73, 711.2) * mm, "end": v(539.73, 762) * mm});
            skLineSegment(sketch, "E65.7.6.3", {"start": v(590.53, 711.2) * mm, "end": v(539.73, 711.2) * mm});
            skLineSegment(sketch, "E65.7.7.0", {"start": v(590.53, 647.7) * mm, "end": v(590.53, 698.5) * mm});
            skLineSegment(sketch, "E65.7.7.1", {"start": v(590.53, 698.5) * mm, "end": v(539.73, 698.5) * mm});
            skLineSegment(sketch, "E65.7.7.2", {"start": v(539.73, 647.7) * mm, "end": v(539.73, 698.5) * mm});
            skLineSegment(sketch, "E65.7.7.3", {"start": v(590.53, 647.7) * mm, "end": v(539.73, 647.7) * mm});
            skLineSegment(sketch, "E65.7.8.0", {"start": v(590.53, 584.2) * mm, "end": v(590.53, 635) * mm});
            skLineSegment(sketch, "E65.7.8.1", {"start": v(590.53, 635) * mm, "end": v(539.73, 635) * mm});
            skLineSegment(sketch, "E65.7.8.2", {"start": v(539.73, 584.2) * mm, "end": v(539.73, 635) * mm});
            skLineSegment(sketch, "E65.7.8.3", {"start": v(590.53, 584.2) * mm, "end": v(539.73, 584.2) * mm});
            skLineSegment(sketch, "E65.7.9.0", {"start": v(590.53, 520.7) * mm, "end": v(590.53, 571.5) * mm});
            skLineSegment(sketch, "E65.7.9.1", {"start": v(590.53, 571.5) * mm, "end": v(539.73, 571.5) * mm});
            skLineSegment(sketch, "E65.7.9.2", {"start": v(539.73, 520.7) * mm, "end": v(539.73, 571.5) * mm});
            skLineSegment(sketch, "E65.7.9.3", {"start": v(590.53, 520.7) * mm, "end": v(539.73, 520.7) * mm});
            skLineSegment(sketch, "E65.7.10.0", {"start": v(590.53, 457.2) * mm, "end": v(590.53, 508) * mm});
            skLineSegment(sketch, "E65.7.10.1", {"start": v(590.53, 508) * mm, "end": v(539.73, 508) * mm});
            skLineSegment(sketch, "E65.7.10.2", {"start": v(539.73, 457.2) * mm, "end": v(539.73, 508) * mm});
            skLineSegment(sketch, "E65.7.10.3", {"start": v(590.53, 457.2) * mm, "end": v(539.73, 457.2) * mm});
            skLineSegment(sketch, "E65.7.11.0", {"start": v(590.53, 393.7) * mm, "end": v(590.53, 444.5) * mm});
            skLineSegment(sketch, "E65.7.11.1", {"start": v(590.53, 444.5) * mm, "end": v(539.73, 444.5) * mm});
            skLineSegment(sketch, "E65.7.11.2", {"start": v(539.73, 393.7) * mm, "end": v(539.73, 444.5) * mm});
            skLineSegment(sketch, "E65.7.11.3", {"start": v(590.53, 393.7) * mm, "end": v(539.73, 393.7) * mm});
            skLineSegment(sketch, "E65.7.12.0", {"start": v(590.53, 330.2) * mm, "end": v(590.53, 381) * mm});
            skLineSegment(sketch, "E65.7.12.1", {"start": v(590.53, 381) * mm, "end": v(539.73, 381) * mm});
            skLineSegment(sketch, "E65.7.12.2", {"start": v(539.73, 330.2) * mm, "end": v(539.73, 381) * mm});
            skLineSegment(sketch, "E65.7.12.3", {"start": v(590.53, 330.2) * mm, "end": v(539.73, 330.2) * mm});
            skLineSegment(sketch, "E65.7.13.0", {"start": v(590.53, 266.7) * mm, "end": v(590.53, 317.5) * mm});
            skLineSegment(sketch, "E65.7.13.1", {"start": v(590.53, 317.5) * mm, "end": v(539.73, 317.5) * mm});
            skLineSegment(sketch, "E65.7.13.2", {"start": v(539.73, 266.7) * mm, "end": v(539.73, 317.5) * mm});
            skLineSegment(sketch, "E65.7.13.3", {"start": v(590.53, 266.7) * mm, "end": v(539.73, 266.7) * mm});
            skLineSegment(sketch, "E65.7.14.0", {"start": v(590.53, 203.2) * mm, "end": v(590.53, 254) * mm});
            skLineSegment(sketch, "E65.7.14.1", {"start": v(590.53, 254) * mm, "end": v(539.73, 254) * mm});
            skLineSegment(sketch, "E65.7.14.2", {"start": v(539.73, 203.2) * mm, "end": v(539.73, 254) * mm});
            skLineSegment(sketch, "E65.7.14.3", {"start": v(590.53, 203.2) * mm, "end": v(539.73, 203.2) * mm});
            skLineSegment(sketch, "E65.7.15.0", {"start": v(590.53, 139.7) * mm, "end": v(590.53, 190.5) * mm});
            skLineSegment(sketch, "E65.7.15.1", {"start": v(590.53, 190.5) * mm, "end": v(539.73, 190.5) * mm});
            skLineSegment(sketch, "E65.7.15.2", {"start": v(539.73, 139.7) * mm, "end": v(539.73, 190.5) * mm});
            skLineSegment(sketch, "E65.7.15.3", {"start": v(590.53, 139.7) * mm, "end": v(539.73, 139.7) * mm});
            skLineSegment(sketch, "E65.direction1", {"start": v(109.18, 1054.37) * mm, "end": v(201.15, 1054.37) * mm, "construction": true});
            skLineSegment(sketch, "E65.direction2", {"start": v(109.18, 1054.37) * mm, "end": v(109.18, 952.93) * mm, "construction": true});
            skLineSegment(sketch, "E66.direction1", {"start": v(95.25, 266.7) * mm, "end": v(679.45, 266.7) * mm, "construction": true});
            skLineSegment(sketch, "E67.0.0.16", {"start": v(146.05, 76.2) * mm, "end": v(146.05, 127) * mm});
            skLineSegment(sketch, "E67.3.0.16", {"start": v(146.05, 127) * mm, "end": v(95.25, 127) * mm});
            skLineSegment(sketch, "E67.6.0.16", {"start": v(95.25, 76.2) * mm, "end": v(95.25, 127) * mm});
            skLineSegment(sketch, "E67.9.0.16", {"start": v(146.05, 76.2) * mm, "end": v(95.25, 76.2) * mm});
            skLineSegment(sketch, "E67.0.1.16", {"start": v(209.55, 76.2) * mm, "end": v(209.55, 127) * mm});
            skLineSegment(sketch, "E67.3.1.16", {"start": v(209.55, 127) * mm, "end": v(158.75, 127) * mm});
            skLineSegment(sketch, "E67.6.1.16", {"start": v(158.75, 76.2) * mm, "end": v(158.75, 127) * mm});
            skLineSegment(sketch, "E67.9.1.16", {"start": v(209.55, 76.2) * mm, "end": v(158.75, 76.2) * mm});
            skLineSegment(sketch, "E67.0.2.16", {"start": v(273.05, 76.2) * mm, "end": v(273.05, 127) * mm});
            skLineSegment(sketch, "E67.3.2.16", {"start": v(273.05, 127) * mm, "end": v(222.25, 127) * mm});
            skLineSegment(sketch, "E67.6.2.16", {"start": v(222.25, 76.2) * mm, "end": v(222.25, 127) * mm});
            skLineSegment(sketch, "E67.9.2.16", {"start": v(273.05, 76.2) * mm, "end": v(222.25, 76.2) * mm});
            skLineSegment(sketch, "E67.0.3.16", {"start": v(336.54, 76.2) * mm, "end": v(336.54, 127) * mm});
            skLineSegment(sketch, "E67.3.3.16", {"start": v(336.54, 127) * mm, "end": v(285.74, 127) * mm});
            skLineSegment(sketch, "E67.6.3.16", {"start": v(285.74, 76.2) * mm, "end": v(285.74, 127) * mm});
            skLineSegment(sketch, "E67.9.3.16", {"start": v(336.54, 76.2) * mm, "end": v(285.74, 76.2) * mm});
            skLineSegment(sketch, "E67.0.4.16", {"start": v(400.04, 76.2) * mm, "end": v(400.04, 127) * mm});
            skLineSegment(sketch, "E67.3.4.16", {"start": v(400.04, 127) * mm, "end": v(349.24, 127) * mm});
            skLineSegment(sketch, "E67.6.4.16", {"start": v(349.24, 76.2) * mm, "end": v(349.24, 127) * mm});
            skLineSegment(sketch, "E67.9.4.16", {"start": v(400.04, 76.2) * mm, "end": v(349.24, 76.2) * mm});
            skLineSegment(sketch, "E67.0.5.16", {"start": v(463.54, 76.2) * mm, "end": v(463.54, 127) * mm});
            skLineSegment(sketch, "E67.3.5.16", {"start": v(463.54, 127) * mm, "end": v(412.74, 127) * mm});
            skLineSegment(sketch, "E67.6.5.16", {"start": v(412.74, 76.2) * mm, "end": v(412.74, 127) * mm});
            skLineSegment(sketch, "E67.9.5.16", {"start": v(463.54, 76.2) * mm, "end": v(412.74, 76.2) * mm});
            skLineSegment(sketch, "E67.0.6.16", {"start": v(527.04, 76.2) * mm, "end": v(527.04, 127) * mm});
            skLineSegment(sketch, "E67.3.6.16", {"start": v(527.04, 127) * mm, "end": v(476.24, 127) * mm});
            skLineSegment(sketch, "E67.6.6.16", {"start": v(476.24, 76.2) * mm, "end": v(476.24, 127) * mm});
            skLineSegment(sketch, "E67.9.6.16", {"start": v(527.04, 76.2) * mm, "end": v(476.24, 76.2) * mm});
            skLineSegment(sketch, "E67.0.7.16", {"start": v(590.53, 76.2) * mm, "end": v(590.53, 127) * mm});
            skLineSegment(sketch, "E67.3.7.16", {"start": v(590.53, 127) * mm, "end": v(539.73, 127) * mm});
            skLineSegment(sketch, "E67.6.7.16", {"start": v(539.73, 76.2) * mm, "end": v(539.73, 127) * mm});
            skLineSegment(sketch, "E67.9.7.16", {"start": v(590.53, 76.2) * mm, "end": v(539.73, 76.2) * mm});
            skLineSegment(sketch, "E68.direction1", {"start": v(285.74, 127) * mm, "end": v(870.3, 127) * mm, "construction": true});
            skLineSegment(sketch, "E69.1.0.0", {"start": v(1111.24, 774.7) * mm, "end": v(1060.44, 774.7) * mm});
            skLineSegment(sketch, "E69.1.0.1", {"start": v(1111.24, 1028.7) * mm, "end": v(1060.44, 1028.7) * mm});
            skLineSegment(sketch, "E69.1.0.2", {"start": v(1047.74, 266.7) * mm, "end": v(996.94, 266.7) * mm});
            skLineSegment(sketch, "E69.1.0.3", {"start": v(1047.74, 520.7) * mm, "end": v(996.94, 520.7) * mm});
            skLineSegment(sketch, "E69.1.0.4", {"start": v(1111.24, 266.7) * mm, "end": v(1060.44, 266.7) * mm});
            skLineSegment(sketch, "E69.1.0.5", {"start": v(1111.24, 520.7) * mm, "end": v(1060.44, 520.7) * mm});
            skLineSegment(sketch, "E69.1.0.6", {"start": v(1174.73, 266.7) * mm, "end": v(1123.93, 266.7) * mm});
            skLineSegment(sketch, "E69.1.0.7", {"start": v(1174.73, 520.7) * mm, "end": v(1123.93, 520.7) * mm});
            skLineSegment(sketch, "E69.1.0.8", {"start": v(1174.73, 774.7) * mm, "end": v(1123.93, 774.7) * mm});
            skLineSegment(sketch, "E69.1.0.9", {"start": v(1174.73, 1028.7) * mm, "end": v(1123.93, 1028.7) * mm});
            skLineSegment(sketch, "E69.1.0.10", {"start": v(1047.74, 76.2) * mm, "end": v(1047.74, 127) * mm});
            skLineSegment(sketch, "E69.1.0.11", {"start": v(793.75, 76.2) * mm, "end": v(793.75, 127) * mm});
            skLineSegment(sketch, "E69.1.0.12", {"start": v(730.25, 774.7) * mm, "end": v(679.45, 774.7) * mm});
            skLineSegment(sketch, "E69.1.0.13", {"start": v(793.75, 774.7) * mm, "end": v(742.95, 774.7) * mm});
            skLineSegment(sketch, "E69.1.0.14", {"start": v(793.75, 1028.7) * mm, "end": v(742.95, 1028.7) * mm});
            skLineSegment(sketch, "E69.1.0.15", {"start": v(730.25, 266.7) * mm, "end": v(679.45, 266.7) * mm});
            skLineSegment(sketch, "E69.1.0.16", {"start": v(730.25, 520.7) * mm, "end": v(679.45, 520.7) * mm});
            skLineSegment(sketch, "E69.1.0.17", {"start": v(857.25, 774.7) * mm, "end": v(806.45, 774.7) * mm});
            skLineSegment(sketch, "E69.1.0.18", {"start": v(857.25, 1028.7) * mm, "end": v(806.45, 1028.7) * mm});
            skLineSegment(sketch, "E69.1.0.19", {"start": v(793.75, 266.7) * mm, "end": v(742.95, 266.7) * mm});
            skLineSegment(sketch, "E69.1.0.20", {"start": v(793.75, 520.7) * mm, "end": v(742.95, 520.7) * mm});
            skLineSegment(sketch, "E69.1.0.21", {"start": v(920.74, 774.7) * mm, "end": v(869.94, 774.7) * mm});
            skLineSegment(sketch, "E69.1.0.22", {"start": v(920.74, 1028.7) * mm, "end": v(869.94, 1028.7) * mm});
            skLineSegment(sketch, "E69.1.0.23", {"start": v(857.25, 266.7) * mm, "end": v(806.45, 266.7) * mm});
            skLineSegment(sketch, "E69.1.0.24", {"start": v(857.25, 520.7) * mm, "end": v(806.45, 520.7) * mm});
            skLineSegment(sketch, "E69.1.0.25", {"start": v(984.24, 774.7) * mm, "end": v(933.44, 774.7) * mm});
            skLineSegment(sketch, "E69.1.0.26", {"start": v(984.24, 1028.7) * mm, "end": v(933.44, 1028.7) * mm});
            skLineSegment(sketch, "E69.1.0.27", {"start": v(920.74, 266.7) * mm, "end": v(869.94, 266.7) * mm});
            skLineSegment(sketch, "E69.1.0.28", {"start": v(920.74, 520.7) * mm, "end": v(869.94, 520.7) * mm});
            skLineSegment(sketch, "E69.1.0.29", {"start": v(1047.74, 774.7) * mm, "end": v(996.94, 774.7) * mm});
            skLineSegment(sketch, "E69.1.0.30", {"start": v(1047.74, 1028.7) * mm, "end": v(996.94, 1028.7) * mm});
            skLineSegment(sketch, "E69.1.0.31", {"start": v(984.24, 266.7) * mm, "end": v(933.44, 266.7) * mm});
            skLineSegment(sketch, "E69.1.0.32", {"start": v(984.24, 520.7) * mm, "end": v(933.44, 520.7) * mm});
            skLineSegment(sketch, "E69.1.0.33", {"start": v(730.25, 711.2) * mm, "end": v(730.25, 762) * mm});
            skLineSegment(sketch, "E69.1.0.34", {"start": v(730.25, 965.2) * mm, "end": v(730.25, 1016) * mm});
            skLineSegment(sketch, "E69.1.0.35", {"start": v(793.75, 711.2) * mm, "end": v(793.75, 762) * mm});
            skLineSegment(sketch, "E69.1.0.36", {"start": v(793.75, 965.2) * mm, "end": v(793.75, 1016) * mm});
            skLineSegment(sketch, "E69.1.0.37", {"start": v(730.25, 203.2) * mm, "end": v(730.25, 254) * mm});
            skLineSegment(sketch, "E69.1.0.38", {"start": v(730.25, 457.2) * mm, "end": v(730.25, 508) * mm});
            skLineSegment(sketch, "E69.1.0.39", {"start": v(857.25, 711.2) * mm, "end": v(857.25, 762) * mm});
            skLineSegment(sketch, "E69.1.0.40", {"start": v(857.25, 965.2) * mm, "end": v(857.25, 1016) * mm});
            skLineSegment(sketch, "E69.1.0.41", {"start": v(793.75, 203.2) * mm, "end": v(793.75, 254) * mm});
            skLineSegment(sketch, "E69.1.0.42", {"start": v(793.75, 457.2) * mm, "end": v(793.75, 508) * mm});
            skLineSegment(sketch, "E69.1.0.43", {"start": v(920.74, 711.2) * mm, "end": v(920.74, 762) * mm});
            skLineSegment(sketch, "E69.1.0.44", {"start": v(920.74, 965.2) * mm, "end": v(920.74, 1016) * mm});
            skLineSegment(sketch, "E69.1.0.45", {"start": v(857.25, 203.2) * mm, "end": v(857.25, 254) * mm});
            skLineSegment(sketch, "E69.1.0.46", {"start": v(857.25, 457.2) * mm, "end": v(857.25, 508) * mm});
            skLineSegment(sketch, "E69.1.0.47", {"start": v(984.24, 711.2) * mm, "end": v(984.24, 762) * mm});
            skLineSegment(sketch, "E69.1.0.48", {"start": v(984.24, 965.2) * mm, "end": v(984.24, 1016) * mm});
            skLineSegment(sketch, "E69.1.0.49", {"start": v(920.74, 203.2) * mm, "end": v(920.74, 254) * mm});
            skLineSegment(sketch, "E69.1.0.50", {"start": v(920.74, 457.2) * mm, "end": v(920.74, 508) * mm});
            skLineSegment(sketch, "E69.1.0.51", {"start": v(1047.74, 711.2) * mm, "end": v(1047.74, 762) * mm});
            skLineSegment(sketch, "E69.1.0.52", {"start": v(1047.74, 965.2) * mm, "end": v(1047.74, 1016) * mm});
            skLineSegment(sketch, "E69.1.0.53", {"start": v(984.24, 203.2) * mm, "end": v(984.24, 254) * mm});
            skLineSegment(sketch, "E69.1.0.54", {"start": v(984.24, 457.2) * mm, "end": v(984.24, 508) * mm});
            skLineSegment(sketch, "E69.1.0.55", {"start": v(1111.24, 965.2) * mm, "end": v(1111.24, 1016) * mm});
            skLineSegment(sketch, "E69.1.0.56", {"start": v(1047.74, 203.2) * mm, "end": v(1047.74, 254) * mm});
            skLineSegment(sketch, "E69.1.0.57", {"start": v(1047.74, 457.2) * mm, "end": v(1047.74, 508) * mm});
            skLineSegment(sketch, "E69.1.0.58", {"start": v(1111.24, 203.2) * mm, "end": v(1111.24, 254) * mm});
            skLineSegment(sketch, "E69.1.0.59", {"start": v(1111.24, 457.2) * mm, "end": v(1111.24, 508) * mm});
            skLineSegment(sketch, "E69.1.0.60", {"start": v(1111.24, 711.2) * mm, "end": v(1111.24, 762) * mm});
            skLineSegment(sketch, "E69.1.0.61", {"start": v(1174.73, 203.2) * mm, "end": v(1174.73, 254) * mm});
            skLineSegment(sketch, "E69.1.0.62", {"start": v(1174.73, 457.2) * mm, "end": v(1174.73, 508) * mm});
            skLineSegment(sketch, "E69.1.0.63", {"start": v(1174.73, 711.2) * mm, "end": v(1174.73, 762) * mm});
            skLineSegment(sketch, "E69.1.0.64", {"start": v(1174.73, 965.2) * mm, "end": v(1174.73, 1016) * mm});
            skLineSegment(sketch, "E69.1.0.65", {"start": v(1047.74, 127) * mm, "end": v(996.94, 127) * mm});
            skLineSegment(sketch, "E69.1.0.66", {"start": v(793.75, 127) * mm, "end": v(742.95, 127) * mm});
            skLineSegment(sketch, "E69.1.0.67", {"start": v(793.75, 762) * mm, "end": v(742.95, 762) * mm});
            skLineSegment(sketch, "E69.1.0.68", {"start": v(793.75, 1016) * mm, "end": v(742.95, 1016) * mm});
            skLineSegment(sketch, "E69.1.0.69", {"start": v(730.25, 254) * mm, "end": v(679.45, 254) * mm});
            skLineSegment(sketch, "E69.1.0.70", {"start": v(730.25, 508) * mm, "end": v(679.45, 508) * mm});
            skLineSegment(sketch, "E69.1.0.71", {"start": v(857.25, 762) * mm, "end": v(806.45, 762) * mm});
            skLineSegment(sketch, "E69.1.0.72", {"start": v(857.25, 1016) * mm, "end": v(806.45, 1016) * mm});
            skLineSegment(sketch, "E69.1.0.73", {"start": v(793.75, 254) * mm, "end": v(742.95, 254) * mm});
            skLineSegment(sketch, "E69.1.0.74", {"start": v(793.75, 508) * mm, "end": v(742.95, 508) * mm});
            skLineSegment(sketch, "E69.1.0.75", {"start": v(920.74, 762) * mm, "end": v(869.94, 762) * mm});
            skLineSegment(sketch, "E69.1.0.76", {"start": v(920.74, 1016) * mm, "end": v(869.94, 1016) * mm});
            skLineSegment(sketch, "E69.1.0.77", {"start": v(857.25, 254) * mm, "end": v(806.45, 254) * mm});
            skLineSegment(sketch, "E69.1.0.78", {"start": v(857.25, 508) * mm, "end": v(806.45, 508) * mm});
            skLineSegment(sketch, "E69.1.0.79", {"start": v(984.24, 762) * mm, "end": v(933.44, 762) * mm});
            skLineSegment(sketch, "E69.1.0.80", {"start": v(984.24, 1016) * mm, "end": v(933.44, 1016) * mm});
            skLineSegment(sketch, "E69.1.0.81", {"start": v(920.74, 254) * mm, "end": v(869.94, 254) * mm});
            skLineSegment(sketch, "E69.1.0.82", {"start": v(920.74, 508) * mm, "end": v(869.94, 508) * mm});
            skLineSegment(sketch, "E69.1.0.83", {"start": v(1047.74, 762) * mm, "end": v(996.94, 762) * mm});
            skLineSegment(sketch, "E69.1.0.84", {"start": v(1047.74, 1016) * mm, "end": v(996.94, 1016) * mm});
            skLineSegment(sketch, "E69.1.0.85", {"start": v(984.24, 254) * mm, "end": v(933.44, 254) * mm});
            skLineSegment(sketch, "E69.1.0.86", {"start": v(984.24, 508) * mm, "end": v(933.44, 508) * mm});
            skLineSegment(sketch, "E69.1.0.87", {"start": v(1111.24, 1016) * mm, "end": v(1060.44, 1016) * mm});
            skLineSegment(sketch, "E69.1.0.88", {"start": v(1047.74, 254) * mm, "end": v(996.94, 254) * mm});
            skLineSegment(sketch, "E69.1.0.89", {"start": v(1047.74, 508) * mm, "end": v(996.94, 508) * mm});
            skLineSegment(sketch, "E69.1.0.90", {"start": v(1111.24, 254) * mm, "end": v(1060.44, 254) * mm});
            skLineSegment(sketch, "E69.1.0.91", {"start": v(1111.24, 508) * mm, "end": v(1060.44, 508) * mm});
            skLineSegment(sketch, "E69.1.0.92", {"start": v(1111.24, 762) * mm, "end": v(1060.44, 762) * mm});
            skLineSegment(sketch, "E69.1.0.93", {"start": v(730.25, 762) * mm, "end": v(679.45, 762) * mm});
            skLineSegment(sketch, "E69.1.0.94", {"start": v(730.25, 1016) * mm, "end": v(679.45, 1016) * mm});
            skLineSegment(sketch, "E69.1.0.95", {"start": v(1174.73, 254) * mm, "end": v(1123.93, 254) * mm});
            skLineSegment(sketch, "E69.1.0.96", {"start": v(1174.73, 508) * mm, "end": v(1123.93, 508) * mm});
            skLineSegment(sketch, "E69.1.0.97", {"start": v(1174.73, 762) * mm, "end": v(1123.93, 762) * mm});
            skLineSegment(sketch, "E69.1.0.98", {"start": v(1174.73, 1016) * mm, "end": v(1123.93, 1016) * mm});
            skLineSegment(sketch, "E69.1.0.99", {"start": v(996.94, 76.2) * mm, "end": v(996.94, 127) * mm});
            skLineSegment(sketch, "E69.1.0.100", {"start": v(742.95, 76.2) * mm, "end": v(742.95, 127) * mm});
            skLineSegment(sketch, "E69.1.0.101", {"start": v(806.45, 711.2) * mm, "end": v(806.45, 762) * mm});
            skLineSegment(sketch, "E69.1.0.102", {"start": v(806.45, 965.2) * mm, "end": v(806.45, 1016) * mm});
            skLineSegment(sketch, "E69.1.0.103", {"start": v(742.95, 203.2) * mm, "end": v(742.95, 254) * mm});
            skLineSegment(sketch, "E69.1.0.104", {"start": v(742.95, 457.2) * mm, "end": v(742.95, 508) * mm});
            skLineSegment(sketch, "E69.1.0.105", {"start": v(869.94, 711.2) * mm, "end": v(869.94, 762) * mm});
            skLineSegment(sketch, "E69.1.0.106", {"start": v(869.94, 965.2) * mm, "end": v(869.94, 1016) * mm});
            skLineSegment(sketch, "E69.1.0.107", {"start": v(806.45, 203.2) * mm, "end": v(806.45, 254) * mm});
            skLineSegment(sketch, "E69.1.0.108", {"start": v(806.45, 457.2) * mm, "end": v(806.45, 508) * mm});
            skLineSegment(sketch, "E69.1.0.109", {"start": v(933.44, 711.2) * mm, "end": v(933.44, 762) * mm});
            skLineSegment(sketch, "E69.1.0.110", {"start": v(933.44, 965.2) * mm, "end": v(933.44, 1016) * mm});
            skLineSegment(sketch, "E69.1.0.111", {"start": v(869.94, 203.2) * mm, "end": v(869.94, 254) * mm});
            skLineSegment(sketch, "E69.1.0.112", {"start": v(869.94, 457.2) * mm, "end": v(869.94, 508) * mm});
            skLineSegment(sketch, "E69.1.0.113", {"start": v(996.94, 711.2) * mm, "end": v(996.94, 762) * mm});
            skLineSegment(sketch, "E69.1.0.114", {"start": v(996.94, 965.2) * mm, "end": v(996.94, 1016) * mm});
            skLineSegment(sketch, "E69.1.0.115", {"start": v(933.44, 203.2) * mm, "end": v(933.44, 254) * mm});
            skLineSegment(sketch, "E69.1.0.116", {"start": v(933.44, 457.2) * mm, "end": v(933.44, 508) * mm});
            skLineSegment(sketch, "E69.1.0.117", {"start": v(1060.44, 965.2) * mm, "end": v(1060.44, 1016) * mm});
            skPoint(sketch, "E69.1.0.118", {"position": v(927.1, 609.6) * mm});
            skLineSegment(sketch, "E69.1.0.119", {"start": v(996.94, 203.2) * mm, "end": v(996.94, 254) * mm});
            skLineSegment(sketch, "E69.1.0.120", {"start": v(996.94, 457.2) * mm, "end": v(996.94, 508) * mm});
            skLineSegment(sketch, "E69.1.0.121", {"start": v(1060.44, 203.2) * mm, "end": v(1060.44, 254) * mm});
            skLineSegment(sketch, "E69.1.0.122", {"start": v(1060.44, 457.2) * mm, "end": v(1060.44, 508) * mm});
            skLineSegment(sketch, "E69.1.0.123", {"start": v(1060.44, 711.2) * mm, "end": v(1060.44, 762) * mm});
            skLineSegment(sketch, "E69.1.0.124", {"start": v(1123.93, 203.2) * mm, "end": v(1123.93, 254) * mm});
            skLineSegment(sketch, "E69.1.0.125", {"start": v(1123.93, 457.2) * mm, "end": v(1123.93, 508) * mm});
            skLineSegment(sketch, "E69.1.0.126", {"start": v(1123.93, 711.2) * mm, "end": v(1123.93, 762) * mm});
            skLineSegment(sketch, "E69.1.0.127", {"start": v(1123.93, 965.2) * mm, "end": v(1123.93, 1016) * mm});
            skLineSegment(sketch, "E69.1.0.128", {"start": v(679.45, 711.2) * mm, "end": v(679.45, 762) * mm});
            skLineSegment(sketch, "E69.1.0.129", {"start": v(679.45, 965.2) * mm, "end": v(679.45, 1016) * mm});
            skLineSegment(sketch, "E69.1.0.130", {"start": v(742.95, 711.2) * mm, "end": v(742.95, 762) * mm});
            skLineSegment(sketch, "E69.1.0.131", {"start": v(742.95, 965.2) * mm, "end": v(742.95, 1016) * mm});
            skLineSegment(sketch, "E69.1.0.132", {"start": v(679.45, 203.2) * mm, "end": v(679.45, 254) * mm});
            skLineSegment(sketch, "E69.1.0.133", {"start": v(679.45, 457.2) * mm, "end": v(679.45, 508) * mm});
            skLineSegment(sketch, "E69.1.0.134", {"start": v(1047.74, 76.2) * mm, "end": v(996.94, 76.2) * mm});
            skLineSegment(sketch, "E69.1.0.135", {"start": v(793.75, 76.2) * mm, "end": v(742.95, 76.2) * mm});
            skLineSegment(sketch, "E69.1.0.136", {"start": v(920.74, 711.2) * mm, "end": v(869.94, 711.2) * mm});
            skLineSegment(sketch, "E69.1.0.137", {"start": v(857.25, 203.2) * mm, "end": v(806.45, 203.2) * mm});
            skLineSegment(sketch, "E69.1.0.138", {"start": v(857.25, 457.2) * mm, "end": v(806.45, 457.2) * mm});
            skLineSegment(sketch, "E69.1.0.139", {"start": v(984.24, 711.2) * mm, "end": v(933.44, 711.2) * mm});
            skLineSegment(sketch, "E69.1.0.140", {"start": v(984.24, 965.2) * mm, "end": v(933.44, 965.2) * mm});
            skLineSegment(sketch, "E69.1.0.141", {"start": v(920.74, 203.2) * mm, "end": v(869.94, 203.2) * mm});
            skLineSegment(sketch, "E69.1.0.142", {"start": v(920.74, 457.2) * mm, "end": v(869.94, 457.2) * mm});
            skLineSegment(sketch, "E69.1.0.143", {"start": v(1047.74, 711.2) * mm, "end": v(996.94, 711.2) * mm});
            skLineSegment(sketch, "E69.1.0.144", {"start": v(1047.74, 965.2) * mm, "end": v(996.94, 965.2) * mm});
            skLineSegment(sketch, "E69.1.0.145", {"start": v(984.24, 203.2) * mm, "end": v(933.44, 203.2) * mm});
            skLineSegment(sketch, "E69.1.0.146", {"start": v(984.24, 457.2) * mm, "end": v(933.44, 457.2) * mm});
            skLineSegment(sketch, "E69.1.0.147", {"start": v(1111.24, 965.2) * mm, "end": v(1060.44, 965.2) * mm});
            skLineSegment(sketch, "E69.1.0.148", {"start": v(1047.74, 203.2) * mm, "end": v(996.94, 203.2) * mm});
            skLineSegment(sketch, "E69.1.0.149", {"start": v(1047.74, 457.2) * mm, "end": v(996.94, 457.2) * mm});
            skLineSegment(sketch, "E69.1.0.150", {"start": v(1111.24, 203.2) * mm, "end": v(1060.44, 203.2) * mm});
            skLineSegment(sketch, "E69.1.0.151", {"start": v(1111.24, 457.2) * mm, "end": v(1060.44, 457.2) * mm});
            skLineSegment(sketch, "E69.1.0.152", {"start": v(1111.24, 711.2) * mm, "end": v(1060.44, 711.2) * mm});
            skLineSegment(sketch, "E69.1.0.153", {"start": v(1174.73, 203.2) * mm, "end": v(1123.93, 203.2) * mm});
            skLineSegment(sketch, "E69.1.0.154", {"start": v(1174.73, 457.2) * mm, "end": v(1123.93, 457.2) * mm});
            skLineSegment(sketch, "E69.1.0.155", {"start": v(1174.73, 711.2) * mm, "end": v(1123.93, 711.2) * mm});
            skLineSegment(sketch, "E69.1.0.156", {"start": v(1174.73, 965.2) * mm, "end": v(1123.93, 965.2) * mm});
            skLineSegment(sketch, "E69.1.0.157", {"start": v(1111.24, 76.2) * mm, "end": v(1111.24, 127) * mm});
            skLineSegment(sketch, "E69.1.0.158", {"start": v(857.25, 76.2) * mm, "end": v(857.25, 127) * mm});
            skLineSegment(sketch, "E69.1.0.159", {"start": v(730.25, 711.2) * mm, "end": v(679.45, 711.2) * mm});
            skLineSegment(sketch, "E69.1.0.160", {"start": v(793.75, 711.2) * mm, "end": v(742.95, 711.2) * mm});
            skLineSegment(sketch, "E69.1.0.161", {"start": v(793.75, 965.2) * mm, "end": v(742.95, 965.2) * mm});
            skLineSegment(sketch, "E69.1.0.162", {"start": v(730.25, 203.2) * mm, "end": v(679.45, 203.2) * mm});
            skLineSegment(sketch, "E69.1.0.163", {"start": v(730.25, 457.2) * mm, "end": v(679.45, 457.2) * mm});
            skLineSegment(sketch, "E69.1.0.164", {"start": v(857.25, 711.2) * mm, "end": v(806.45, 711.2) * mm});
            skLineSegment(sketch, "E69.1.0.165", {"start": v(857.25, 965.2) * mm, "end": v(806.45, 965.2) * mm});
            skLineSegment(sketch, "E69.1.0.166", {"start": v(793.75, 203.2) * mm, "end": v(742.95, 203.2) * mm});
            skLineSegment(sketch, "E69.1.0.167", {"start": v(793.75, 457.2) * mm, "end": v(742.95, 457.2) * mm});
            skLineSegment(sketch, "E69.1.0.168", {"start": v(984.24, 647.7) * mm, "end": v(984.24, 698.5) * mm});
            skLineSegment(sketch, "E69.1.0.169", {"start": v(984.24, 901.7) * mm, "end": v(984.24, 952.5) * mm});
            skLineSegment(sketch, "E69.1.0.170", {"start": v(920.74, 139.7) * mm, "end": v(920.74, 190.5) * mm});
            skLineSegment(sketch, "E69.1.0.171", {"start": v(920.74, 393.7) * mm, "end": v(920.74, 444.5) * mm});
            skLineSegment(sketch, "E69.1.0.172", {"start": v(1047.74, 647.7) * mm, "end": v(1047.74, 698.5) * mm});
            skLineSegment(sketch, "E69.1.0.173", {"start": v(1047.74, 901.7) * mm, "end": v(1047.74, 952.5) * mm});
            skLineSegment(sketch, "E69.1.0.174", {"start": v(984.24, 139.7) * mm, "end": v(984.24, 190.5) * mm});
            skLineSegment(sketch, "E69.1.0.175", {"start": v(984.24, 393.7) * mm, "end": v(984.24, 444.5) * mm});
            skLineSegment(sketch, "E69.1.0.176", {"start": v(1111.24, 901.7) * mm, "end": v(1111.24, 952.5) * mm});
            skLineSegment(sketch, "E69.1.0.177", {"start": v(1047.74, 139.7) * mm, "end": v(1047.74, 190.5) * mm});
            skLineSegment(sketch, "E69.1.0.178", {"start": v(1047.74, 393.7) * mm, "end": v(1047.74, 444.5) * mm});
            skLineSegment(sketch, "E69.1.0.179", {"start": v(1111.24, 139.7) * mm, "end": v(1111.24, 190.5) * mm});
            skLineSegment(sketch, "E69.1.0.180", {"start": v(1111.24, 393.7) * mm, "end": v(1111.24, 444.5) * mm});
            skLineSegment(sketch, "E69.1.0.181", {"start": v(1111.24, 647.7) * mm, "end": v(1111.24, 698.5) * mm});
            skLineSegment(sketch, "E69.1.0.182", {"start": v(1174.73, 139.7) * mm, "end": v(1174.73, 190.5) * mm});
            skLineSegment(sketch, "E69.1.0.183", {"start": v(1174.73, 393.7) * mm, "end": v(1174.73, 444.5) * mm});
            skLineSegment(sketch, "E69.1.0.184", {"start": v(1174.73, 647.7) * mm, "end": v(1174.73, 698.5) * mm});
            skLineSegment(sketch, "E69.1.0.185", {"start": v(1174.73, 901.7) * mm, "end": v(1174.73, 952.5) * mm});
            skLineSegment(sketch, "E69.1.0.186", {"start": v(1111.24, 127) * mm, "end": v(1060.44, 127) * mm});
            skLineSegment(sketch, "E69.1.0.187", {"start": v(857.25, 127) * mm, "end": v(806.45, 127) * mm});
            skLineSegment(sketch, "E69.1.0.188", {"start": v(730.25, 647.7) * mm, "end": v(730.25, 698.5) * mm});
            skLineSegment(sketch, "E69.1.0.189", {"start": v(730.25, 901.7) * mm, "end": v(730.25, 952.5) * mm});
            skLineSegment(sketch, "E69.1.0.190", {"start": v(793.75, 647.7) * mm, "end": v(793.75, 698.5) * mm});
            skLineSegment(sketch, "E69.1.0.191", {"start": v(793.75, 901.7) * mm, "end": v(793.75, 952.5) * mm});
            skLineSegment(sketch, "E69.1.0.192", {"start": v(730.25, 139.7) * mm, "end": v(730.25, 190.5) * mm});
            skLineSegment(sketch, "E69.1.0.193", {"start": v(730.25, 393.7) * mm, "end": v(730.25, 444.5) * mm});
            skLineSegment(sketch, "E69.1.0.194", {"start": v(857.25, 647.7) * mm, "end": v(857.25, 698.5) * mm});
            skLineSegment(sketch, "E69.1.0.195", {"start": v(857.25, 901.7) * mm, "end": v(857.25, 952.5) * mm});
            skLineSegment(sketch, "E69.1.0.196", {"start": v(793.75, 139.7) * mm, "end": v(793.75, 190.5) * mm});
            skLineSegment(sketch, "E69.1.0.197", {"start": v(793.75, 393.7) * mm, "end": v(793.75, 444.5) * mm});
            skLineSegment(sketch, "E69.1.0.198", {"start": v(920.74, 647.7) * mm, "end": v(920.74, 698.5) * mm});
            skLineSegment(sketch, "E69.1.0.199", {"start": v(920.74, 901.7) * mm, "end": v(920.74, 952.5) * mm});
            skLineSegment(sketch, "E69.1.0.200", {"start": v(857.25, 139.7) * mm, "end": v(857.25, 190.5) * mm});
            skLineSegment(sketch, "E69.1.0.201", {"start": v(857.25, 393.7) * mm, "end": v(857.25, 444.5) * mm});
            skLineSegment(sketch, "E69.1.0.202", {"start": v(1047.74, 698.5) * mm, "end": v(996.94, 698.5) * mm});
            skLineSegment(sketch, "E69.1.0.203", {"start": v(1047.74, 952.5) * mm, "end": v(996.94, 952.5) * mm});
            skLineSegment(sketch, "E69.1.0.204", {"start": v(984.24, 190.5) * mm, "end": v(933.44, 190.5) * mm});
            skLineSegment(sketch, "E69.1.0.205", {"start": v(984.24, 444.5) * mm, "end": v(933.44, 444.5) * mm});
            skLineSegment(sketch, "E69.1.0.206", {"start": v(1111.24, 952.5) * mm, "end": v(1060.44, 952.5) * mm});
            skLineSegment(sketch, "E69.1.0.207", {"start": v(1047.74, 190.5) * mm, "end": v(996.94, 190.5) * mm});
            skLineSegment(sketch, "E69.1.0.208", {"start": v(1047.74, 444.5) * mm, "end": v(996.94, 444.5) * mm});
            skLineSegment(sketch, "E69.1.0.209", {"start": v(1111.24, 190.5) * mm, "end": v(1060.44, 190.5) * mm});
            skLineSegment(sketch, "E69.1.0.210", {"start": v(1111.24, 444.5) * mm, "end": v(1060.44, 444.5) * mm});
            skLineSegment(sketch, "E69.1.0.211", {"start": v(1111.24, 698.5) * mm, "end": v(1060.44, 698.5) * mm});
            skLineSegment(sketch, "E69.1.0.212", {"start": v(1174.73, 190.5) * mm, "end": v(1123.93, 190.5) * mm});
            skLineSegment(sketch, "E69.1.0.213", {"start": v(1174.73, 444.5) * mm, "end": v(1123.93, 444.5) * mm});
            skLineSegment(sketch, "E69.1.0.214", {"start": v(1174.73, 698.5) * mm, "end": v(1123.93, 698.5) * mm});
            skLineSegment(sketch, "E69.1.0.215", {"start": v(1174.73, 952.5) * mm, "end": v(1123.93, 952.5) * mm});
            skLineSegment(sketch, "E69.1.0.216", {"start": v(1060.44, 76.2) * mm, "end": v(1060.44, 127) * mm});
            skLineSegment(sketch, "E69.1.0.217", {"start": v(806.45, 76.2) * mm, "end": v(806.45, 127) * mm});
            skLineSegment(sketch, "E69.1.0.218", {"start": v(730.25, 698.5) * mm, "end": v(679.45, 698.5) * mm});
            skLineSegment(sketch, "E69.1.0.219", {"start": v(793.75, 698.5) * mm, "end": v(742.95, 698.5) * mm});
            skLineSegment(sketch, "E69.1.0.220", {"start": v(793.75, 952.5) * mm, "end": v(742.95, 952.5) * mm});
            skLineSegment(sketch, "E69.1.0.221", {"start": v(730.25, 190.5) * mm, "end": v(679.45, 190.5) * mm});
            skLineSegment(sketch, "E69.1.0.222", {"start": v(730.25, 444.5) * mm, "end": v(679.45, 444.5) * mm});
            skLineSegment(sketch, "E69.1.0.223", {"start": v(857.25, 698.5) * mm, "end": v(806.45, 698.5) * mm});
            skLineSegment(sketch, "E69.1.0.224", {"start": v(857.25, 952.5) * mm, "end": v(806.45, 952.5) * mm});
            skLineSegment(sketch, "E69.1.0.225", {"start": v(793.75, 190.5) * mm, "end": v(742.95, 190.5) * mm});
            skLineSegment(sketch, "E69.1.0.226", {"start": v(793.75, 444.5) * mm, "end": v(742.95, 444.5) * mm});
            skLineSegment(sketch, "E69.1.0.227", {"start": v(920.74, 698.5) * mm, "end": v(869.94, 698.5) * mm});
            skLineSegment(sketch, "E69.1.0.228", {"start": v(857.25, 190.5) * mm, "end": v(806.45, 190.5) * mm});
            skLineSegment(sketch, "E69.1.0.229", {"start": v(857.25, 444.5) * mm, "end": v(806.45, 444.5) * mm});
            skLineSegment(sketch, "E69.1.0.230", {"start": v(984.24, 698.5) * mm, "end": v(933.44, 698.5) * mm});
            skLineSegment(sketch, "E69.1.0.231", {"start": v(984.24, 952.5) * mm, "end": v(933.44, 952.5) * mm});
            skLineSegment(sketch, "E69.1.0.232", {"start": v(920.74, 190.5) * mm, "end": v(869.94, 190.5) * mm});
            skLineSegment(sketch, "E69.1.0.233", {"start": v(920.74, 444.5) * mm, "end": v(869.94, 444.5) * mm});
            skLineSegment(sketch, "E69.1.0.234", {"start": v(1060.44, 901.7) * mm, "end": v(1060.44, 952.5) * mm});
            skLineSegment(sketch, "E69.1.0.235", {"start": v(996.94, 139.7) * mm, "end": v(996.94, 190.5) * mm});
            skLineSegment(sketch, "E69.1.0.236", {"start": v(996.94, 393.7) * mm, "end": v(996.94, 444.5) * mm});
            skLineSegment(sketch, "E69.1.0.237", {"start": v(1060.44, 139.7) * mm, "end": v(1060.44, 190.5) * mm});
            skLineSegment(sketch, "E69.1.0.238", {"start": v(1060.44, 393.7) * mm, "end": v(1060.44, 444.5) * mm});
            skLineSegment(sketch, "E69.1.0.239", {"start": v(1060.44, 647.7) * mm, "end": v(1060.44, 698.5) * mm});
            skLineSegment(sketch, "E69.1.0.240", {"start": v(1123.93, 139.7) * mm, "end": v(1123.93, 190.5) * mm});
            skLineSegment(sketch, "E69.1.0.241", {"start": v(1123.93, 393.7) * mm, "end": v(1123.93, 444.5) * mm});
            skLineSegment(sketch, "E69.1.0.242", {"start": v(1123.93, 647.7) * mm, "end": v(1123.93, 698.5) * mm});
            skLineSegment(sketch, "E69.1.0.243", {"start": v(1123.93, 901.7) * mm, "end": v(1123.93, 952.5) * mm});
            skLineSegment(sketch, "E69.1.0.244", {"start": v(1111.24, 76.2) * mm, "end": v(1060.44, 76.2) * mm});
            skLineSegment(sketch, "E69.1.0.245", {"start": v(857.25, 76.2) * mm, "end": v(806.45, 76.2) * mm});
            skLineSegment(sketch, "E69.1.0.246", {"start": v(679.45, 647.7) * mm, "end": v(679.45, 698.5) * mm});
            skLineSegment(sketch, "E69.1.0.247", {"start": v(679.45, 901.7) * mm, "end": v(679.45, 952.5) * mm});
            skLineSegment(sketch, "E69.1.0.248", {"start": v(742.95, 647.7) * mm, "end": v(742.95, 698.5) * mm});
            skLineSegment(sketch, "E69.1.0.249", {"start": v(742.95, 901.7) * mm, "end": v(742.95, 952.5) * mm});
            skLineSegment(sketch, "E69.1.0.250", {"start": v(679.45, 139.7) * mm, "end": v(679.45, 190.5) * mm});
            skLineSegment(sketch, "E69.1.0.251", {"start": v(679.45, 393.7) * mm, "end": v(679.45, 444.5) * mm});
            skLineSegment(sketch, "E69.1.0.252", {"start": v(806.45, 647.7) * mm, "end": v(806.45, 698.5) * mm});
            skLineSegment(sketch, "E69.1.0.253", {"start": v(806.45, 901.7) * mm, "end": v(806.45, 952.5) * mm});
            skLineSegment(sketch, "E69.1.0.254", {"start": v(742.95, 139.7) * mm, "end": v(742.95, 190.5) * mm});
            skLineSegment(sketch, "E69.1.0.255", {"start": v(742.95, 393.7) * mm, "end": v(742.95, 444.5) * mm});
            skLineSegment(sketch, "E69.1.0.256", {"start": v(869.94, 647.7) * mm, "end": v(869.94, 698.5) * mm});
            skLineSegment(sketch, "E69.1.0.257", {"start": v(869.94, 901.7) * mm, "end": v(869.94, 952.5) * mm});
            skLineSegment(sketch, "E69.1.0.258", {"start": v(806.45, 139.7) * mm, "end": v(806.45, 190.5) * mm});
            skLineSegment(sketch, "E69.1.0.259", {"start": v(806.45, 393.7) * mm, "end": v(806.45, 444.5) * mm});
            skLineSegment(sketch, "E69.1.0.260", {"start": v(933.44, 647.7) * mm, "end": v(933.44, 698.5) * mm});
            skLineSegment(sketch, "E69.1.0.261", {"start": v(933.44, 901.7) * mm, "end": v(933.44, 952.5) * mm});
            skLineSegment(sketch, "E69.1.0.262", {"start": v(869.94, 139.7) * mm, "end": v(869.94, 190.5) * mm});
            skLineSegment(sketch, "E69.1.0.263", {"start": v(869.94, 393.7) * mm, "end": v(869.94, 444.5) * mm});
            skLineSegment(sketch, "E69.1.0.264", {"start": v(996.94, 647.7) * mm, "end": v(996.94, 698.5) * mm});
            skLineSegment(sketch, "E69.1.0.265", {"start": v(996.94, 901.7) * mm, "end": v(996.94, 952.5) * mm});
            skLineSegment(sketch, "E69.1.0.266", {"start": v(933.44, 139.7) * mm, "end": v(933.44, 190.5) * mm});
            skLineSegment(sketch, "E69.1.0.267", {"start": v(933.44, 393.7) * mm, "end": v(933.44, 444.5) * mm});
            skLineSegment(sketch, "E69.1.0.268", {"start": v(1174.73, 647.7) * mm, "end": v(1123.93, 647.7) * mm});
            skLineSegment(sketch, "E69.1.0.269", {"start": v(1174.73, 901.7) * mm, "end": v(1123.93, 901.7) * mm});
            skLineSegment(sketch, "E69.1.0.270", {"start": v(1111.24, 139.7) * mm, "end": v(1060.44, 139.7) * mm});
            skLineSegment(sketch, "E69.1.0.271", {"start": v(1111.24, 393.7) * mm, "end": v(1060.44, 393.7) * mm});
            skLineSegment(sketch, "E69.1.0.272", {"start": v(1174.73, 76.2) * mm, "end": v(1174.73, 127) * mm});
            skLineSegment(sketch, "E69.1.0.273", {"start": v(920.74, 76.2) * mm, "end": v(920.74, 127) * mm});
            skLineSegment(sketch, "E69.1.0.274", {"start": v(1174.73, 139.7) * mm, "end": v(1123.93, 139.7) * mm});
            skLineSegment(sketch, "E69.1.0.275", {"start": v(1174.73, 393.7) * mm, "end": v(1123.93, 393.7) * mm});
            skLineSegment(sketch, "E69.1.0.276", {"start": v(730.25, 139.7) * mm, "end": v(679.45, 139.7) * mm});
            skLineSegment(sketch, "E69.1.0.277", {"start": v(730.25, 393.7) * mm, "end": v(679.45, 393.7) * mm});
            skLineSegment(sketch, "E69.1.0.278", {"start": v(730.25, 647.7) * mm, "end": v(679.45, 647.7) * mm});
            skLineSegment(sketch, "E69.1.0.279", {"start": v(730.25, 901.7) * mm, "end": v(679.45, 901.7) * mm});
            skLineSegment(sketch, "E69.1.0.280", {"start": v(793.75, 139.7) * mm, "end": v(742.95, 139.7) * mm});
            skLineSegment(sketch, "E69.1.0.281", {"start": v(793.75, 393.7) * mm, "end": v(742.95, 393.7) * mm});
            skLineSegment(sketch, "E69.1.0.282", {"start": v(793.75, 647.7) * mm, "end": v(742.95, 647.7) * mm});
            skLineSegment(sketch, "E69.1.0.283", {"start": v(793.75, 901.7) * mm, "end": v(742.95, 901.7) * mm});
            skLineSegment(sketch, "E69.1.0.284", {"start": v(857.25, 139.7) * mm, "end": v(806.45, 139.7) * mm});
            skLineSegment(sketch, "E69.1.0.285", {"start": v(857.25, 393.7) * mm, "end": v(806.45, 393.7) * mm});
            skLineSegment(sketch, "E69.1.0.286", {"start": v(857.25, 647.7) * mm, "end": v(806.45, 647.7) * mm});
            skLineSegment(sketch, "E69.1.0.287", {"start": v(857.25, 901.7) * mm, "end": v(806.45, 901.7) * mm});
            skLineSegment(sketch, "E69.1.0.288", {"start": v(920.74, 139.7) * mm, "end": v(869.94, 139.7) * mm});
            skLineSegment(sketch, "E69.1.0.289", {"start": v(920.74, 393.7) * mm, "end": v(869.94, 393.7) * mm});
            skLineSegment(sketch, "E69.1.0.290", {"start": v(920.74, 647.7) * mm, "end": v(869.94, 647.7) * mm});
            skLineSegment(sketch, "E69.1.0.291", {"start": v(920.74, 901.7) * mm, "end": v(869.94, 901.7) * mm});
            skLineSegment(sketch, "E69.1.0.292", {"start": v(984.24, 139.7) * mm, "end": v(933.44, 139.7) * mm});
            skLineSegment(sketch, "E69.1.0.293", {"start": v(984.24, 393.7) * mm, "end": v(933.44, 393.7) * mm});
            skLineSegment(sketch, "E69.1.0.294", {"start": v(984.24, 647.7) * mm, "end": v(933.44, 647.7) * mm});
            skLineSegment(sketch, "E69.1.0.295", {"start": v(984.24, 901.7) * mm, "end": v(933.44, 901.7) * mm});
            skLineSegment(sketch, "E69.1.0.296", {"start": v(1047.74, 139.7) * mm, "end": v(996.94, 139.7) * mm});
            skLineSegment(sketch, "E69.1.0.297", {"start": v(1047.74, 393.7) * mm, "end": v(996.94, 393.7) * mm});
            skLineSegment(sketch, "E69.1.0.298", {"start": v(1047.74, 647.7) * mm, "end": v(996.94, 647.7) * mm});
            skLineSegment(sketch, "E69.1.0.299", {"start": v(1047.74, 901.7) * mm, "end": v(996.94, 901.7) * mm});
            skLineSegment(sketch, "E69.1.0.300", {"start": v(1111.24, 901.7) * mm, "end": v(1060.44, 901.7) * mm});
            skLineSegment(sketch, "E69.1.0.301", {"start": v(1111.24, 647.7) * mm, "end": v(1060.44, 647.7) * mm});
            skLineSegment(sketch, "E69.1.0.302", {"start": v(793.75, 1092.2) * mm, "end": v(793.75, 1143) * mm});
            skLineSegment(sketch, "E69.1.0.303", {"start": v(730.25, 330.2) * mm, "end": v(730.25, 381) * mm});
            skLineSegment(sketch, "E69.1.0.304", {"start": v(730.25, 584.2) * mm, "end": v(730.25, 635) * mm});
            skLineSegment(sketch, "E69.1.0.305", {"start": v(730.25, 838.2) * mm, "end": v(730.25, 889) * mm});
            skLineSegment(sketch, "E69.1.0.306", {"start": v(1174.73, 127) * mm, "end": v(1123.93, 127) * mm});
            skLineSegment(sketch, "E69.1.0.307", {"start": v(920.74, 127) * mm, "end": v(869.94, 127) * mm});
            skLineSegment(sketch, "E69.1.0.308", {"start": v(693.38, 1054.37) * mm, "end": v(785.35, 1054.37) * mm, "construction": true});
            skLineSegment(sketch, "E69.1.0.309", {"start": v(1174.73, 330.2) * mm, "end": v(1174.73, 381) * mm});
            skLineSegment(sketch, "E69.1.0.310", {"start": v(857.25, 1092.2) * mm, "end": v(857.25, 1143) * mm});
            skLineSegment(sketch, "E69.1.0.311", {"start": v(793.75, 330.2) * mm, "end": v(793.75, 381) * mm});
            skLineSegment(sketch, "E69.1.0.312", {"start": v(793.75, 584.2) * mm, "end": v(793.75, 635) * mm});
            skLineSegment(sketch, "E69.1.0.313", {"start": v(793.75, 838.2) * mm, "end": v(793.75, 889) * mm});
            skLineSegment(sketch, "E69.1.0.314", {"start": v(920.74, 1092.2) * mm, "end": v(920.74, 1143) * mm});
            skLineSegment(sketch, "E69.1.0.315", {"start": v(857.25, 330.2) * mm, "end": v(857.25, 381) * mm});
            skLineSegment(sketch, "E69.1.0.316", {"start": v(857.25, 584.2) * mm, "end": v(857.25, 635) * mm});
            skLineSegment(sketch, "E69.1.0.317", {"start": v(857.25, 838.2) * mm, "end": v(857.25, 889) * mm});
            skLineSegment(sketch, "E69.1.0.318", {"start": v(984.24, 1092.2) * mm, "end": v(984.24, 1143) * mm});
            skLineSegment(sketch, "E69.1.0.319", {"start": v(920.74, 330.2) * mm, "end": v(920.74, 381) * mm});
            skLineSegment(sketch, "E69.1.0.320", {"start": v(920.74, 838.2) * mm, "end": v(920.74, 889) * mm});
            skLineSegment(sketch, "E69.1.0.321", {"start": v(1047.74, 1092.2) * mm, "end": v(1047.74, 1143) * mm});
            skLineSegment(sketch, "E69.1.0.322", {"start": v(984.24, 330.2) * mm, "end": v(984.24, 381) * mm});
            skLineSegment(sketch, "E69.1.0.323", {"start": v(984.24, 584.2) * mm, "end": v(984.24, 635) * mm});
            skLineSegment(sketch, "E69.1.0.324", {"start": v(984.24, 838.2) * mm, "end": v(984.24, 889) * mm});
            skLineSegment(sketch, "E69.1.0.325", {"start": v(1111.24, 1092.2) * mm, "end": v(1111.24, 1143) * mm});
            skLineSegment(sketch, "E69.1.0.326", {"start": v(1047.74, 330.2) * mm, "end": v(1047.74, 381) * mm});
            skLineSegment(sketch, "E69.1.0.327", {"start": v(1047.74, 584.2) * mm, "end": v(1047.74, 635) * mm});
            skLineSegment(sketch, "E69.1.0.328", {"start": v(1047.74, 838.2) * mm, "end": v(1047.74, 889) * mm});
            skLineSegment(sketch, "E69.1.0.329", {"start": v(1111.24, 838.2) * mm, "end": v(1111.24, 889) * mm});
            skLineSegment(sketch, "E69.1.0.330", {"start": v(1111.24, 584.2) * mm, "end": v(1111.24, 635) * mm});
            skLineSegment(sketch, "E69.1.0.331", {"start": v(1174.73, 838.2) * mm, "end": v(1174.73, 889) * mm});
            skLineSegment(sketch, "E69.1.0.332", {"start": v(1174.73, 1092.2) * mm, "end": v(1174.73, 1143) * mm});
            skLineSegment(sketch, "E69.1.0.333", {"start": v(1111.24, 330.2) * mm, "end": v(1111.24, 381) * mm});
            skLineSegment(sketch, "E69.1.0.334", {"start": v(793.75, 1143) * mm, "end": v(742.95, 1143) * mm});
            skLineSegment(sketch, "E69.1.0.335", {"start": v(730.25, 381) * mm, "end": v(679.45, 381) * mm});
            skLineSegment(sketch, "E69.1.0.336", {"start": v(730.25, 635) * mm, "end": v(679.45, 635) * mm});
            skLineSegment(sketch, "E69.1.0.337", {"start": v(730.25, 889) * mm, "end": v(679.45, 889) * mm});
            skLineSegment(sketch, "E69.1.0.338", {"start": v(857.25, 1143) * mm, "end": v(806.45, 1143) * mm});
            skLineSegment(sketch, "E69.1.0.339", {"start": v(793.75, 381) * mm, "end": v(742.95, 381) * mm});
            skLineSegment(sketch, "E69.1.0.340", {"start": v(793.75, 635) * mm, "end": v(742.95, 635) * mm});
            skLineSegment(sketch, "E69.1.0.341", {"start": v(793.75, 889) * mm, "end": v(742.95, 889) * mm});
            skLineSegment(sketch, "E69.1.0.342", {"start": v(920.74, 1143) * mm, "end": v(869.94, 1143) * mm});
            skLineSegment(sketch, "E69.1.0.343", {"start": v(857.25, 381) * mm, "end": v(806.45, 381) * mm});
            skLineSegment(sketch, "E69.1.0.344", {"start": v(857.25, 635) * mm, "end": v(806.45, 635) * mm});
            skLineSegment(sketch, "E69.1.0.345", {"start": v(857.25, 889) * mm, "end": v(806.45, 889) * mm});
            skLineSegment(sketch, "E69.1.0.346", {"start": v(984.24, 1143) * mm, "end": v(933.44, 1143) * mm});
            skLineSegment(sketch, "E69.1.0.347", {"start": v(920.74, 381) * mm, "end": v(869.94, 381) * mm});
            skLineSegment(sketch, "E69.1.0.348", {"start": v(920.74, 635) * mm, "end": v(869.94, 635) * mm});
            skLineSegment(sketch, "E69.1.0.349", {"start": v(920.74, 889) * mm, "end": v(869.94, 889) * mm});
            skLineSegment(sketch, "E69.1.0.350", {"start": v(1047.74, 1143) * mm, "end": v(996.94, 1143) * mm});
            skLineSegment(sketch, "E69.1.0.351", {"start": v(984.24, 381) * mm, "end": v(933.44, 381) * mm});
            skLineSegment(sketch, "E69.1.0.352", {"start": v(984.24, 635) * mm, "end": v(933.44, 635) * mm});
            skLineSegment(sketch, "E69.1.0.353", {"start": v(984.24, 889) * mm, "end": v(933.44, 889) * mm});
            skLineSegment(sketch, "E69.1.0.354", {"start": v(1111.24, 1143) * mm, "end": v(1060.44, 1143) * mm});
            skLineSegment(sketch, "E69.1.0.355", {"start": v(1047.74, 381) * mm, "end": v(996.94, 381) * mm});
            skLineSegment(sketch, "E69.1.0.356", {"start": v(1047.74, 635) * mm, "end": v(996.94, 635) * mm});
            skLineSegment(sketch, "E69.1.0.357", {"start": v(1047.74, 889) * mm, "end": v(996.94, 889) * mm});
            skLineSegment(sketch, "E69.1.0.358", {"start": v(1111.24, 889) * mm, "end": v(1060.44, 889) * mm});
            skLineSegment(sketch, "E69.1.0.359", {"start": v(1111.24, 635) * mm, "end": v(1060.44, 635) * mm});
            skLineSegment(sketch, "E69.1.0.360", {"start": v(1174.73, 635) * mm, "end": v(1123.93, 635) * mm});
            skLineSegment(sketch, "E69.1.0.361", {"start": v(1174.73, 889) * mm, "end": v(1123.93, 889) * mm});
            skLineSegment(sketch, "E69.1.0.362", {"start": v(1174.73, 1143) * mm, "end": v(1123.93, 1143) * mm});
            skLineSegment(sketch, "E69.1.0.363", {"start": v(1111.24, 381) * mm, "end": v(1060.44, 381) * mm});
            skLineSegment(sketch, "E69.1.0.364", {"start": v(1123.93, 76.2) * mm, "end": v(1123.93, 127) * mm});
            skLineSegment(sketch, "E69.1.0.365", {"start": v(869.94, 76.2) * mm, "end": v(869.94, 127) * mm});
            skLineSegment(sketch, "E69.1.0.366", {"start": v(693.38, 1054.37) * mm, "end": v(693.38, 952.93) * mm, "construction": true});
            skLineSegment(sketch, "E69.1.0.367", {"start": v(1174.73, 381) * mm, "end": v(1123.93, 381) * mm});
            skLineSegment(sketch, "E69.1.0.368", {"start": v(742.95, 1092.2) * mm, "end": v(742.95, 1143) * mm});
            skLineSegment(sketch, "E69.1.0.369", {"start": v(679.45, 330.2) * mm, "end": v(679.45, 381) * mm});
            skLineSegment(sketch, "E69.1.0.370", {"start": v(679.45, 838.2) * mm, "end": v(679.45, 889) * mm});
            skLineSegment(sketch, "E69.1.0.371", {"start": v(806.45, 1092.2) * mm, "end": v(806.45, 1143) * mm});
            skLineSegment(sketch, "E69.1.0.372", {"start": v(742.95, 330.2) * mm, "end": v(742.95, 381) * mm});
            skLineSegment(sketch, "E69.1.0.373", {"start": v(742.95, 584.2) * mm, "end": v(742.95, 635) * mm});
            skLineSegment(sketch, "E69.1.0.374", {"start": v(742.95, 838.2) * mm, "end": v(742.95, 889) * mm});
            skLineSegment(sketch, "E69.1.0.375", {"start": v(869.94, 1092.2) * mm, "end": v(869.94, 1143) * mm});
            skLineSegment(sketch, "E69.1.0.376", {"start": v(806.45, 330.2) * mm, "end": v(806.45, 381) * mm});
            skLineSegment(sketch, "E69.1.0.377", {"start": v(806.45, 584.2) * mm, "end": v(806.45, 635) * mm});
            skLineSegment(sketch, "E69.1.0.378", {"start": v(806.45, 838.2) * mm, "end": v(806.45, 889) * mm});
            skLineSegment(sketch, "E69.1.0.379", {"start": v(933.44, 1092.2) * mm, "end": v(933.44, 1143) * mm});
            skLineSegment(sketch, "E69.1.0.380", {"start": v(869.94, 330.2) * mm, "end": v(869.94, 381) * mm});
            skLineSegment(sketch, "E69.1.0.381", {"start": v(869.94, 584.2) * mm, "end": v(869.94, 635) * mm});
            skLineSegment(sketch, "E69.1.0.382", {"start": v(869.94, 838.2) * mm, "end": v(869.94, 889) * mm});
            skLineSegment(sketch, "E69.1.0.383", {"start": v(996.94, 1092.2) * mm, "end": v(996.94, 1143) * mm});
            skLineSegment(sketch, "E69.1.0.384", {"start": v(933.44, 330.2) * mm, "end": v(933.44, 381) * mm});
            skLineSegment(sketch, "E69.1.0.385", {"start": v(933.44, 838.2) * mm, "end": v(933.44, 889) * mm});
            skLineSegment(sketch, "E69.1.0.386", {"start": v(1060.44, 1092.2) * mm, "end": v(1060.44, 1143) * mm});
            skLineSegment(sketch, "E69.1.0.387", {"start": v(996.94, 330.2) * mm, "end": v(996.94, 381) * mm});
            skLineSegment(sketch, "E69.1.0.388", {"start": v(996.94, 584.2) * mm, "end": v(996.94, 635) * mm});
            skLineSegment(sketch, "E69.1.0.389", {"start": v(996.94, 838.2) * mm, "end": v(996.94, 889) * mm});
            skLineSegment(sketch, "E69.1.0.390", {"start": v(1060.44, 838.2) * mm, "end": v(1060.44, 889) * mm});
            skLineSegment(sketch, "E69.1.0.391", {"start": v(1060.44, 584.2) * mm, "end": v(1060.44, 635) * mm});
            skLineSegment(sketch, "E69.1.0.392", {"start": v(1123.93, 584.2) * mm, "end": v(1123.93, 635) * mm});
            skLineSegment(sketch, "E69.1.0.393", {"start": v(1123.93, 838.2) * mm, "end": v(1123.93, 889) * mm});
            skLineSegment(sketch, "E69.1.0.394", {"start": v(1123.93, 1092.2) * mm, "end": v(1123.93, 1143) * mm});
            skLineSegment(sketch, "E69.1.0.395", {"start": v(1060.44, 330.2) * mm, "end": v(1060.44, 381) * mm});
            skLineSegment(sketch, "E69.1.0.396", {"start": v(920.74, 76.2) * mm, "end": v(869.94, 76.2) * mm});
            skLineSegment(sketch, "E69.1.0.397", {"start": v(679.45, 266.7) * mm, "end": v(1263.65, 266.7) * mm, "construction": true});
            skLineSegment(sketch, "E69.1.0.398", {"start": v(1123.93, 330.2) * mm, "end": v(1123.93, 381) * mm});
            skLineSegment(sketch, "E69.1.0.399", {"start": v(793.75, 1092.2) * mm, "end": v(742.95, 1092.2) * mm});
            skLineSegment(sketch, "E69.1.0.400", {"start": v(730.25, 330.2) * mm, "end": v(679.45, 330.2) * mm});
            skLineSegment(sketch, "E69.1.0.401", {"start": v(730.25, 584.2) * mm, "end": v(679.45, 584.2) * mm});
            skLineSegment(sketch, "E69.1.0.402", {"start": v(730.25, 838.2) * mm, "end": v(679.45, 838.2) * mm});
            skLineSegment(sketch, "E69.1.0.403", {"start": v(857.25, 1092.2) * mm, "end": v(806.45, 1092.2) * mm});
            skLineSegment(sketch, "E69.1.0.404", {"start": v(793.75, 330.2) * mm, "end": v(742.95, 330.2) * mm});
            skLineSegment(sketch, "E69.1.0.405", {"start": v(793.75, 584.2) * mm, "end": v(742.95, 584.2) * mm});
            skLineSegment(sketch, "E69.1.0.406", {"start": v(793.75, 838.2) * mm, "end": v(742.95, 838.2) * mm});
            skLineSegment(sketch, "E69.1.0.407", {"start": v(920.74, 1092.2) * mm, "end": v(869.94, 1092.2) * mm});
            skLineSegment(sketch, "E69.1.0.408", {"start": v(857.25, 330.2) * mm, "end": v(806.45, 330.2) * mm});
            skLineSegment(sketch, "E69.1.0.409", {"start": v(857.25, 584.2) * mm, "end": v(806.45, 584.2) * mm});
            skLineSegment(sketch, "E69.1.0.410", {"start": v(857.25, 838.2) * mm, "end": v(806.45, 838.2) * mm});
            skLineSegment(sketch, "E69.1.0.411", {"start": v(984.24, 1092.2) * mm, "end": v(933.44, 1092.2) * mm});
            skLineSegment(sketch, "E69.1.0.412", {"start": v(920.74, 330.2) * mm, "end": v(869.94, 330.2) * mm});
            skLineSegment(sketch, "E69.1.0.413", {"start": v(920.74, 584.2) * mm, "end": v(869.94, 584.2) * mm});
            skLineSegment(sketch, "E69.1.0.414", {"start": v(920.74, 838.2) * mm, "end": v(869.94, 838.2) * mm});
            skLineSegment(sketch, "E69.1.0.415", {"start": v(1047.74, 1092.2) * mm, "end": v(996.94, 1092.2) * mm});
            skLineSegment(sketch, "E69.1.0.416", {"start": v(984.24, 330.2) * mm, "end": v(933.44, 330.2) * mm});
            skLineSegment(sketch, "E69.1.0.417", {"start": v(984.24, 584.2) * mm, "end": v(933.44, 584.2) * mm});
            skLineSegment(sketch, "E69.1.0.418", {"start": v(984.24, 838.2) * mm, "end": v(933.44, 838.2) * mm});
            skLineSegment(sketch, "E69.1.0.419", {"start": v(1111.24, 1092.2) * mm, "end": v(1060.44, 1092.2) * mm});
            skLineSegment(sketch, "E69.1.0.420", {"start": v(1047.74, 330.2) * mm, "end": v(996.94, 330.2) * mm});
            skLineSegment(sketch, "E69.1.0.421", {"start": v(1047.74, 584.2) * mm, "end": v(996.94, 584.2) * mm});
            skLineSegment(sketch, "E69.1.0.422", {"start": v(1047.74, 838.2) * mm, "end": v(996.94, 838.2) * mm});
            skLineSegment(sketch, "E69.1.0.423", {"start": v(1111.24, 838.2) * mm, "end": v(1060.44, 838.2) * mm});
            skLineSegment(sketch, "E69.1.0.424", {"start": v(1111.24, 584.2) * mm, "end": v(1060.44, 584.2) * mm});
            skLineSegment(sketch, "E69.1.0.425", {"start": v(1174.73, 584.2) * mm, "end": v(1123.93, 584.2) * mm});
            skLineSegment(sketch, "E69.1.0.426", {"start": v(1174.73, 838.2) * mm, "end": v(1123.93, 838.2) * mm});
            skLineSegment(sketch, "E69.1.0.427", {"start": v(1174.73, 1092.2) * mm, "end": v(1123.93, 1092.2) * mm});
            skLineSegment(sketch, "E69.1.0.428", {"start": v(1111.24, 330.2) * mm, "end": v(1060.44, 330.2) * mm});
            skLineSegment(sketch, "E69.1.0.429", {"start": v(869.94, 127) * mm, "end": v(1454.5, 127) * mm, "construction": true});
            skLineSegment(sketch, "E69.1.0.430", {"start": v(730.25, 76.2) * mm, "end": v(730.25, 127) * mm});
            skLineSegment(sketch, "E69.1.0.431", {"start": v(1174.73, 330.2) * mm, "end": v(1123.93, 330.2) * mm});
            skLineSegment(sketch, "E69.1.0.432", {"start": v(730.25, 266.7) * mm, "end": v(730.25, 317.5) * mm});
            skLineSegment(sketch, "E69.1.0.433", {"start": v(730.25, 520.7) * mm, "end": v(730.25, 571.5) * mm});
            skLineSegment(sketch, "E69.1.0.434", {"start": v(730.25, 774.7) * mm, "end": v(730.25, 825.5) * mm});
            skLineSegment(sketch, "E69.1.0.435", {"start": v(857.25, 1028.7) * mm, "end": v(857.25, 1079.5) * mm});
            skLineSegment(sketch, "E69.1.0.436", {"start": v(793.75, 266.7) * mm, "end": v(793.75, 317.5) * mm});
            skLineSegment(sketch, "E69.1.0.437", {"start": v(793.75, 520.7) * mm, "end": v(793.75, 571.5) * mm});
            skLineSegment(sketch, "E69.1.0.438", {"start": v(793.75, 774.7) * mm, "end": v(793.75, 825.5) * mm});
            skLineSegment(sketch, "E69.1.0.439", {"start": v(920.74, 1028.7) * mm, "end": v(920.74, 1079.5) * mm});
            skLineSegment(sketch, "E69.1.0.440", {"start": v(857.25, 266.7) * mm, "end": v(857.25, 317.5) * mm});
            skLineSegment(sketch, "E69.1.0.441", {"start": v(857.25, 520.7) * mm, "end": v(857.25, 571.5) * mm});
            skLineSegment(sketch, "E69.1.0.442", {"start": v(857.25, 774.7) * mm, "end": v(857.25, 825.5) * mm});
            skLineSegment(sketch, "E69.1.0.443", {"start": v(984.24, 1028.7) * mm, "end": v(984.24, 1079.5) * mm});
            skLineSegment(sketch, "E69.1.0.444", {"start": v(920.74, 266.7) * mm, "end": v(920.74, 317.5) * mm});
            skLineSegment(sketch, "E69.1.0.445", {"start": v(920.74, 520.7) * mm, "end": v(920.74, 571.5) * mm});
            skLineSegment(sketch, "E69.1.0.446", {"start": v(920.74, 774.7) * mm, "end": v(920.74, 825.5) * mm});
            skLineSegment(sketch, "E69.1.0.447", {"start": v(1047.74, 1028.7) * mm, "end": v(1047.74, 1079.5) * mm});
            skLineSegment(sketch, "E69.1.0.448", {"start": v(984.24, 266.7) * mm, "end": v(984.24, 317.5) * mm});
            skLineSegment(sketch, "E69.1.0.449", {"start": v(984.24, 520.7) * mm, "end": v(984.24, 571.5) * mm});
            skLineSegment(sketch, "E69.1.0.450", {"start": v(984.24, 774.7) * mm, "end": v(984.24, 825.5) * mm});
            skLineSegment(sketch, "E69.1.0.451", {"start": v(1111.24, 1028.7) * mm, "end": v(1111.24, 1079.5) * mm});
            skLineSegment(sketch, "E69.1.0.452", {"start": v(1047.74, 266.7) * mm, "end": v(1047.74, 317.5) * mm});
            skLineSegment(sketch, "E69.1.0.453", {"start": v(1047.74, 520.7) * mm, "end": v(1047.74, 571.5) * mm});
            skLineSegment(sketch, "E69.1.0.454", {"start": v(1047.74, 774.7) * mm, "end": v(1047.74, 825.5) * mm});
            skLineSegment(sketch, "E69.1.0.455", {"start": v(1111.24, 774.7) * mm, "end": v(1111.24, 825.5) * mm});
            skLineSegment(sketch, "E69.1.0.456", {"start": v(1111.24, 520.7) * mm, "end": v(1111.24, 571.5) * mm});
            skLineSegment(sketch, "E69.1.0.457", {"start": v(1174.73, 520.7) * mm, "end": v(1174.73, 571.5) * mm});
            skLineSegment(sketch, "E69.1.0.458", {"start": v(1174.73, 774.7) * mm, "end": v(1174.73, 825.5) * mm});
            skLineSegment(sketch, "E69.1.0.459", {"start": v(1174.73, 1028.7) * mm, "end": v(1174.73, 1079.5) * mm});
            skLineSegment(sketch, "E69.1.0.460", {"start": v(1111.24, 266.7) * mm, "end": v(1111.24, 317.5) * mm});
            skLineSegment(sketch, "E69.1.0.461", {"start": v(984.24, 127) * mm, "end": v(933.44, 127) * mm});
            skLineSegment(sketch, "E69.1.0.462", {"start": v(730.25, 127) * mm, "end": v(679.45, 127) * mm});
            skLineSegment(sketch, "E69.1.0.463", {"start": v(1174.73, 266.7) * mm, "end": v(1174.73, 317.5) * mm});
            skPoint(sketch, "E69.1.0.464", {"position": v(704.85, 1117.6) * mm});
            skLineSegment(sketch, "E69.1.0.465", {"start": v(984.24, 825.5) * mm, "end": v(933.44, 825.5) * mm});
            skLineSegment(sketch, "E69.1.0.466", {"start": v(984.24, 1079.5) * mm, "end": v(933.44, 1079.5) * mm});
            skLineSegment(sketch, "E69.1.0.467", {"start": v(920.74, 317.5) * mm, "end": v(869.94, 317.5) * mm});
            skLineSegment(sketch, "E69.1.0.468", {"start": v(920.74, 571.5) * mm, "end": v(869.94, 571.5) * mm});
            skLineSegment(sketch, "E69.1.0.469", {"start": v(1047.74, 825.5) * mm, "end": v(996.94, 825.5) * mm});
            skLineSegment(sketch, "E69.1.0.470", {"start": v(1047.74, 1079.5) * mm, "end": v(996.94, 1079.5) * mm});
            skLineSegment(sketch, "E69.1.0.471", {"start": v(984.24, 317.5) * mm, "end": v(933.44, 317.5) * mm});
            skLineSegment(sketch, "E69.1.0.472", {"start": v(984.24, 571.5) * mm, "end": v(933.44, 571.5) * mm});
            skLineSegment(sketch, "E69.1.0.473", {"start": v(1111.24, 825.5) * mm, "end": v(1060.44, 825.5) * mm});
            skLineSegment(sketch, "E69.1.0.474", {"start": v(1111.24, 1079.5) * mm, "end": v(1060.44, 1079.5) * mm});
            skLineSegment(sketch, "E69.1.0.475", {"start": v(1047.74, 317.5) * mm, "end": v(996.94, 317.5) * mm});
            skLineSegment(sketch, "E69.1.0.476", {"start": v(1047.74, 571.5) * mm, "end": v(996.94, 571.5) * mm});
            skLineSegment(sketch, "E69.1.0.477", {"start": v(1111.24, 317.5) * mm, "end": v(1060.44, 317.5) * mm});
            skLineSegment(sketch, "E69.1.0.478", {"start": v(1111.24, 571.5) * mm, "end": v(1060.44, 571.5) * mm});
            skLineSegment(sketch, "E69.1.0.479", {"start": v(1174.73, 317.5) * mm, "end": v(1123.93, 317.5) * mm});
            skLineSegment(sketch, "E69.1.0.480", {"start": v(1174.73, 571.5) * mm, "end": v(1123.93, 571.5) * mm});
            skLineSegment(sketch, "E69.1.0.481", {"start": v(1174.73, 825.5) * mm, "end": v(1123.93, 825.5) * mm});
            skLineSegment(sketch, "E69.1.0.482", {"start": v(1174.73, 1079.5) * mm, "end": v(1123.93, 1079.5) * mm});
            skLineSegment(sketch, "E69.1.0.483", {"start": v(933.44, 76.2) * mm, "end": v(933.44, 127) * mm});
            skLineSegment(sketch, "E69.1.0.484", {"start": v(679.45, 76.2) * mm, "end": v(679.45, 127) * mm});
            skLineSegment(sketch, "E69.1.0.485", {"start": v(730.25, 825.5) * mm, "end": v(679.45, 825.5) * mm});
            skLineSegment(sketch, "E69.1.0.486", {"start": v(793.75, 825.5) * mm, "end": v(742.95, 825.5) * mm});
            skLineSegment(sketch, "E69.1.0.487", {"start": v(793.75, 1079.5) * mm, "end": v(742.95, 1079.5) * mm});
            skLineSegment(sketch, "E69.1.0.488", {"start": v(730.25, 317.5) * mm, "end": v(679.45, 317.5) * mm});
            skLineSegment(sketch, "E69.1.0.489", {"start": v(730.25, 571.5) * mm, "end": v(679.45, 571.5) * mm});
            skLineSegment(sketch, "E69.1.0.490", {"start": v(857.25, 825.5) * mm, "end": v(806.45, 825.5) * mm});
            skLineSegment(sketch, "E69.1.0.491", {"start": v(857.25, 1079.5) * mm, "end": v(806.45, 1079.5) * mm});
            skLineSegment(sketch, "E69.1.0.492", {"start": v(793.75, 317.5) * mm, "end": v(742.95, 317.5) * mm});
            skLineSegment(sketch, "E69.1.0.493", {"start": v(793.75, 571.5) * mm, "end": v(742.95, 571.5) * mm});
            skLineSegment(sketch, "E69.1.0.494", {"start": v(920.74, 825.5) * mm, "end": v(869.94, 825.5) * mm});
            skLineSegment(sketch, "E69.1.0.495", {"start": v(920.74, 1079.5) * mm, "end": v(869.94, 1079.5) * mm});
            skLineSegment(sketch, "E69.1.0.496", {"start": v(857.25, 317.5) * mm, "end": v(806.45, 317.5) * mm});
            skLineSegment(sketch, "E69.1.0.497", {"start": v(857.25, 571.5) * mm, "end": v(806.45, 571.5) * mm});
            skLineSegment(sketch, "E69.1.0.498", {"start": v(730.25, 1079.5) * mm, "end": v(679.45, 1079.5) * mm});
            skLineSegment(sketch, "E69.1.0.499", {"start": v(730.25, 1028.7) * mm, "end": v(679.45, 1028.7) * mm});
            skLineSegment(sketch, "E69.1.0.500", {"start": v(1187.45, 1155.7) * mm, "end": v(666.75, 1155.7) * mm});
            skLineSegment(sketch, "E69.1.0.501", {"start": v(1187.45, 63.5) * mm, "end": v(666.75, 63.5) * mm});
            skLineSegment(sketch, "E69.1.0.502", {"start": v(1187.45, 1155.7) * mm, "end": v(1187.45, 63.5) * mm});
            skLineSegment(sketch, "E69.1.0.503", {"start": v(666.75, 1155.7) * mm, "end": v(666.75, 63.5) * mm});
            skLineSegment(sketch, "E69.1.0.504", {"start": v(996.94, 774.7) * mm, "end": v(996.94, 825.5) * mm});
            skLineSegment(sketch, "E69.1.0.505", {"start": v(996.94, 1028.7) * mm, "end": v(996.94, 1079.5) * mm});
            skLineSegment(sketch, "E69.1.0.506", {"start": v(933.44, 266.7) * mm, "end": v(933.44, 317.5) * mm});
            skLineSegment(sketch, "E69.1.0.507", {"start": v(933.44, 520.7) * mm, "end": v(933.44, 571.5) * mm});
            skLineSegment(sketch, "E69.1.0.508", {"start": v(730.25, 1092.2) * mm, "end": v(679.45, 1092.2) * mm});
            skLineSegment(sketch, "E69.1.0.509", {"start": v(1060.44, 774.7) * mm, "end": v(1060.44, 825.5) * mm});
            skLineSegment(sketch, "E69.1.0.510", {"start": v(1060.44, 1028.7) * mm, "end": v(1060.44, 1079.5) * mm});
            skLineSegment(sketch, "E69.1.0.511", {"start": v(996.94, 266.7) * mm, "end": v(996.94, 317.5) * mm});
            skLineSegment(sketch, "E69.1.0.512", {"start": v(996.94, 520.7) * mm, "end": v(996.94, 571.5) * mm});
            skLineSegment(sketch, "E69.1.0.513", {"start": v(730.25, 1143) * mm, "end": v(679.45, 1143) * mm});
            skLineSegment(sketch, "E69.1.0.514", {"start": v(730.25, 1092.2) * mm, "end": v(730.25, 1143) * mm});
            skLineSegment(sketch, "E69.1.0.515", {"start": v(1060.44, 266.7) * mm, "end": v(1060.44, 317.5) * mm});
            skLineSegment(sketch, "E69.1.0.516", {"start": v(1060.44, 520.7) * mm, "end": v(1060.44, 571.5) * mm});
            skLineSegment(sketch, "E69.1.0.517", {"start": v(679.45, 1092.2) * mm, "end": v(679.45, 1143) * mm});
            skLineSegment(sketch, "E69.1.0.518", {"start": v(1123.93, 266.7) * mm, "end": v(1123.93, 317.5) * mm});
            skLineSegment(sketch, "E69.1.0.519", {"start": v(1123.93, 520.7) * mm, "end": v(1123.93, 571.5) * mm});
            skLineSegment(sketch, "E69.1.0.520", {"start": v(1123.93, 774.7) * mm, "end": v(1123.93, 825.5) * mm});
            skLineSegment(sketch, "E69.1.0.521", {"start": v(1123.93, 1028.7) * mm, "end": v(1123.93, 1079.5) * mm});
            skLineSegment(sketch, "E69.1.0.522", {"start": v(730.25, 1028.7) * mm, "end": v(730.25, 1079.5) * mm});
            skLineSegment(sketch, "E69.1.0.523", {"start": v(730.25, 76.2) * mm, "end": v(679.45, 76.2) * mm});
            skLineSegment(sketch, "E69.1.0.524", {"start": v(679.45, 774.7) * mm, "end": v(679.45, 825.5) * mm});
            skLineSegment(sketch, "E69.1.0.525", {"start": v(742.95, 774.7) * mm, "end": v(742.95, 825.5) * mm});
            skLineSegment(sketch, "E69.1.0.526", {"start": v(742.95, 1028.7) * mm, "end": v(742.95, 1079.5) * mm});
            skLineSegment(sketch, "E69.1.0.527", {"start": v(679.45, 266.7) * mm, "end": v(679.45, 317.5) * mm});
            skLineSegment(sketch, "E69.1.0.528", {"start": v(679.45, 520.7) * mm, "end": v(679.45, 571.5) * mm});
            skLineSegment(sketch, "E69.1.0.529", {"start": v(806.45, 774.7) * mm, "end": v(806.45, 825.5) * mm});
            skLineSegment(sketch, "E69.1.0.530", {"start": v(806.45, 1028.7) * mm, "end": v(806.45, 1079.5) * mm});
            skLineSegment(sketch, "E69.1.0.531", {"start": v(742.95, 266.7) * mm, "end": v(742.95, 317.5) * mm});
            skLineSegment(sketch, "E69.1.0.532", {"start": v(742.95, 520.7) * mm, "end": v(742.95, 571.5) * mm});
            skLineSegment(sketch, "E69.1.0.533", {"start": v(869.94, 774.7) * mm, "end": v(869.94, 825.5) * mm});
            skLineSegment(sketch, "E69.1.0.534", {"start": v(869.94, 1028.7) * mm, "end": v(869.94, 1079.5) * mm});
            skLineSegment(sketch, "E69.1.0.535", {"start": v(806.45, 266.7) * mm, "end": v(806.45, 317.5) * mm});
            skLineSegment(sketch, "E69.1.0.536", {"start": v(806.45, 520.7) * mm, "end": v(806.45, 571.5) * mm});
            skLineSegment(sketch, "E69.1.0.537", {"start": v(933.44, 774.7) * mm, "end": v(933.44, 825.5) * mm});
            skLineSegment(sketch, "E69.1.0.538", {"start": v(933.44, 1028.7) * mm, "end": v(933.44, 1079.5) * mm});
            skLineSegment(sketch, "E69.1.0.539", {"start": v(869.94, 266.7) * mm, "end": v(869.94, 317.5) * mm});
            skLineSegment(sketch, "E69.1.0.540", {"start": v(869.94, 520.7) * mm, "end": v(869.94, 571.5) * mm});
            skLineSegment(sketch, "E69.1.0.541", {"start": v(920.74, 965.2) * mm, "end": v(869.94, 965.2) * mm});
            skLineSegment(sketch, "E69.1.0.542", {"start": v(730.25, 965.2) * mm, "end": v(679.45, 965.2) * mm});
            skLineSegment(sketch, "E69.1.0.543", {"start": v(730.25, 952.5) * mm, "end": v(679.45, 952.5) * mm});
            skLineSegment(sketch, "E69.1.0.544", {"start": v(920.74, 952.5) * mm, "end": v(869.94, 952.5) * mm});
            skLineSegment(sketch, "E69.1.0.545", {"start": v(920.74, 584.2) * mm, "end": v(920.74, 635) * mm});
            skLineSegment(sketch, "E69.1.0.546", {"start": v(1174.73, 584.2) * mm, "end": v(1174.73, 635) * mm});
            skLineSegment(sketch, "E69.1.0.547", {"start": v(679.45, 584.2) * mm, "end": v(679.45, 635) * mm});
            skLineSegment(sketch, "E69.1.0.548", {"start": v(933.44, 584.2) * mm, "end": v(933.44, 635) * mm});
            skLineSegment(sketch, "E69.1.0.549", {"start": v(1174.73, 76.2) * mm, "end": v(1123.93, 76.2) * mm});
            skLineSegment(sketch, "E69.1.0.550", {"start": v(984.24, 76.2) * mm, "end": v(984.24, 127) * mm});
            skLineSegment(sketch, "E69.1.0.551", {"start": v(793.75, 1028.7) * mm, "end": v(793.75, 1079.5) * mm});
            skLineSegment(sketch, "E69.1.0.552", {"start": v(927.1, 1193.8) * mm, "end": v(927.1, 1155.7) * mm, "construction": true});
            skLineSegment(sketch, "E69.1.0.553", {"start": v(1187.45, 609.6) * mm, "end": v(1219.2, 609.6) * mm, "construction": true});
            skLineSegment(sketch, "E69.1.0.554", {"start": v(927.1, 25.4) * mm, "end": v(927.1, 63.5) * mm, "construction": true});
            skLineSegment(sketch, "E69.1.0.555", {"start": v(635, 609.6) * mm, "end": v(666.75, 609.6) * mm, "construction": true});
            skLineSegment(sketch, "E69.1.0.556", {"start": v(984.24, 76.2) * mm, "end": v(933.44, 76.2) * mm});
            skLineSegment(sketch, "E69.1.0.557", {"start": v(679.45, 1028.7) * mm, "end": v(679.45, 1079.5) * mm});
            skLineSegment(sketch, "E69.2.0.0", {"start": v(1695.44, 774.7) * mm, "end": v(1644.64, 774.7) * mm});
            skLineSegment(sketch, "E69.2.0.1", {"start": v(1695.44, 1028.7) * mm, "end": v(1644.64, 1028.7) * mm});
            skLineSegment(sketch, "E69.2.0.2", {"start": v(1631.94, 266.7) * mm, "end": v(1581.14, 266.7) * mm});
            skLineSegment(sketch, "E69.2.0.3", {"start": v(1631.94, 520.7) * mm, "end": v(1581.14, 520.7) * mm});
            skLineSegment(sketch, "E69.2.0.4", {"start": v(1695.44, 266.7) * mm, "end": v(1644.64, 266.7) * mm});
            skLineSegment(sketch, "E69.2.0.5", {"start": v(1695.44, 520.7) * mm, "end": v(1644.64, 520.7) * mm});
            skLineSegment(sketch, "E69.2.0.6", {"start": v(1758.93, 266.7) * mm, "end": v(1708.13, 266.7) * mm});
            skLineSegment(sketch, "E69.2.0.7", {"start": v(1758.93, 520.7) * mm, "end": v(1708.13, 520.7) * mm});
            skLineSegment(sketch, "E69.2.0.8", {"start": v(1758.93, 774.7) * mm, "end": v(1708.13, 774.7) * mm});
            skLineSegment(sketch, "E69.2.0.9", {"start": v(1758.93, 1028.7) * mm, "end": v(1708.13, 1028.7) * mm});
            skLineSegment(sketch, "E69.2.0.10", {"start": v(1631.94, 76.2) * mm, "end": v(1631.94, 127) * mm});
            skLineSegment(sketch, "E69.2.0.11", {"start": v(1377.95, 76.2) * mm, "end": v(1377.95, 127) * mm});
            skLineSegment(sketch, "E69.2.0.12", {"start": v(1314.45, 774.7) * mm, "end": v(1263.65, 774.7) * mm});
            skLineSegment(sketch, "E69.2.0.13", {"start": v(1377.95, 774.7) * mm, "end": v(1327.15, 774.7) * mm});
            skLineSegment(sketch, "E69.2.0.14", {"start": v(1377.95, 1028.7) * mm, "end": v(1327.15, 1028.7) * mm});
            skLineSegment(sketch, "E69.2.0.15", {"start": v(1314.45, 266.7) * mm, "end": v(1263.65, 266.7) * mm});
            skLineSegment(sketch, "E69.2.0.16", {"start": v(1314.45, 520.7) * mm, "end": v(1263.65, 520.7) * mm});
            skLineSegment(sketch, "E69.2.0.17", {"start": v(1441.45, 774.7) * mm, "end": v(1390.65, 774.7) * mm});
            skLineSegment(sketch, "E69.2.0.18", {"start": v(1441.45, 1028.7) * mm, "end": v(1390.65, 1028.7) * mm});
            skLineSegment(sketch, "E69.2.0.19", {"start": v(1377.95, 266.7) * mm, "end": v(1327.15, 266.7) * mm});
            skLineSegment(sketch, "E69.2.0.20", {"start": v(1377.95, 520.7) * mm, "end": v(1327.15, 520.7) * mm});
            skLineSegment(sketch, "E69.2.0.21", {"start": v(1504.94, 774.7) * mm, "end": v(1454.14, 774.7) * mm});
            skLineSegment(sketch, "E69.2.0.22", {"start": v(1504.94, 1028.7) * mm, "end": v(1454.14, 1028.7) * mm});
            skLineSegment(sketch, "E69.2.0.23", {"start": v(1441.45, 266.7) * mm, "end": v(1390.65, 266.7) * mm});
            skLineSegment(sketch, "E69.2.0.24", {"start": v(1441.45, 520.7) * mm, "end": v(1390.65, 520.7) * mm});
            skLineSegment(sketch, "E69.2.0.25", {"start": v(1568.44, 774.7) * mm, "end": v(1517.64, 774.7) * mm});
            skLineSegment(sketch, "E69.2.0.26", {"start": v(1568.44, 1028.7) * mm, "end": v(1517.64, 1028.7) * mm});
            skLineSegment(sketch, "E69.2.0.27", {"start": v(1504.94, 266.7) * mm, "end": v(1454.14, 266.7) * mm});
            skLineSegment(sketch, "E69.2.0.28", {"start": v(1504.94, 520.7) * mm, "end": v(1454.14, 520.7) * mm});
            skLineSegment(sketch, "E69.2.0.29", {"start": v(1631.94, 774.7) * mm, "end": v(1581.14, 774.7) * mm});
            skLineSegment(sketch, "E69.2.0.30", {"start": v(1631.94, 1028.7) * mm, "end": v(1581.14, 1028.7) * mm});
            skLineSegment(sketch, "E69.2.0.31", {"start": v(1568.44, 266.7) * mm, "end": v(1517.64, 266.7) * mm});
            skLineSegment(sketch, "E69.2.0.32", {"start": v(1568.44, 520.7) * mm, "end": v(1517.64, 520.7) * mm});
            skLineSegment(sketch, "E69.2.0.33", {"start": v(1314.45, 711.2) * mm, "end": v(1314.45, 762) * mm});
            skLineSegment(sketch, "E69.2.0.34", {"start": v(1314.45, 965.2) * mm, "end": v(1314.45, 1016) * mm});
            skLineSegment(sketch, "E69.2.0.35", {"start": v(1377.95, 711.2) * mm, "end": v(1377.95, 762) * mm});
            skLineSegment(sketch, "E69.2.0.36", {"start": v(1377.95, 965.2) * mm, "end": v(1377.95, 1016) * mm});
            skLineSegment(sketch, "E69.2.0.37", {"start": v(1314.45, 203.2) * mm, "end": v(1314.45, 254) * mm});
            skLineSegment(sketch, "E69.2.0.38", {"start": v(1314.45, 457.2) * mm, "end": v(1314.45, 508) * mm});
            skLineSegment(sketch, "E69.2.0.39", {"start": v(1441.45, 711.2) * mm, "end": v(1441.45, 762) * mm});
            skLineSegment(sketch, "E69.2.0.40", {"start": v(1441.45, 965.2) * mm, "end": v(1441.45, 1016) * mm});
            skLineSegment(sketch, "E69.2.0.41", {"start": v(1377.95, 203.2) * mm, "end": v(1377.95, 254) * mm});
            skLineSegment(sketch, "E69.2.0.42", {"start": v(1377.95, 457.2) * mm, "end": v(1377.95, 508) * mm});
            skLineSegment(sketch, "E69.2.0.43", {"start": v(1504.94, 711.2) * mm, "end": v(1504.94, 762) * mm});
            skLineSegment(sketch, "E69.2.0.44", {"start": v(1504.94, 965.2) * mm, "end": v(1504.94, 1016) * mm});
            skLineSegment(sketch, "E69.2.0.45", {"start": v(1441.45, 203.2) * mm, "end": v(1441.45, 254) * mm});
            skLineSegment(sketch, "E69.2.0.46", {"start": v(1441.45, 457.2) * mm, "end": v(1441.45, 508) * mm});
            skLineSegment(sketch, "E69.2.0.47", {"start": v(1568.44, 711.2) * mm, "end": v(1568.44, 762) * mm});
            skLineSegment(sketch, "E69.2.0.48", {"start": v(1568.44, 965.2) * mm, "end": v(1568.44, 1016) * mm});
            skLineSegment(sketch, "E69.2.0.49", {"start": v(1504.94, 203.2) * mm, "end": v(1504.94, 254) * mm});
            skLineSegment(sketch, "E69.2.0.50", {"start": v(1504.94, 457.2) * mm, "end": v(1504.94, 508) * mm});
            skLineSegment(sketch, "E69.2.0.51", {"start": v(1631.94, 711.2) * mm, "end": v(1631.94, 762) * mm});
            skLineSegment(sketch, "E69.2.0.52", {"start": v(1631.94, 965.2) * mm, "end": v(1631.94, 1016) * mm});
            skLineSegment(sketch, "E69.2.0.53", {"start": v(1568.44, 203.2) * mm, "end": v(1568.44, 254) * mm});
            skLineSegment(sketch, "E69.2.0.54", {"start": v(1568.44, 457.2) * mm, "end": v(1568.44, 508) * mm});
            skLineSegment(sketch, "E69.2.0.55", {"start": v(1695.44, 965.2) * mm, "end": v(1695.44, 1016) * mm});
            skLineSegment(sketch, "E69.2.0.56", {"start": v(1631.94, 203.2) * mm, "end": v(1631.94, 254) * mm});
            skLineSegment(sketch, "E69.2.0.57", {"start": v(1631.94, 457.2) * mm, "end": v(1631.94, 508) * mm});
            skLineSegment(sketch, "E69.2.0.58", {"start": v(1695.44, 203.2) * mm, "end": v(1695.44, 254) * mm});
            skLineSegment(sketch, "E69.2.0.59", {"start": v(1695.44, 457.2) * mm, "end": v(1695.44, 508) * mm});
            skLineSegment(sketch, "E69.2.0.60", {"start": v(1695.44, 711.2) * mm, "end": v(1695.44, 762) * mm});
            skLineSegment(sketch, "E69.2.0.61", {"start": v(1758.93, 203.2) * mm, "end": v(1758.93, 254) * mm});
            skLineSegment(sketch, "E69.2.0.62", {"start": v(1758.93, 457.2) * mm, "end": v(1758.93, 508) * mm});
            skLineSegment(sketch, "E69.2.0.63", {"start": v(1758.93, 711.2) * mm, "end": v(1758.93, 762) * mm});
            skLineSegment(sketch, "E69.2.0.64", {"start": v(1758.93, 965.2) * mm, "end": v(1758.93, 1016) * mm});
            skLineSegment(sketch, "E69.2.0.65", {"start": v(1631.94, 127) * mm, "end": v(1581.14, 127) * mm});
            skLineSegment(sketch, "E69.2.0.66", {"start": v(1377.95, 127) * mm, "end": v(1327.15, 127) * mm});
            skLineSegment(sketch, "E69.2.0.67", {"start": v(1377.95, 762) * mm, "end": v(1327.15, 762) * mm});
            skLineSegment(sketch, "E69.2.0.68", {"start": v(1377.95, 1016) * mm, "end": v(1327.15, 1016) * mm});
            skLineSegment(sketch, "E69.2.0.69", {"start": v(1314.45, 254) * mm, "end": v(1263.65, 254) * mm});
            skLineSegment(sketch, "E69.2.0.70", {"start": v(1314.45, 508) * mm, "end": v(1263.65, 508) * mm});
            skLineSegment(sketch, "E69.2.0.71", {"start": v(1441.45, 762) * mm, "end": v(1390.65, 762) * mm});
            skLineSegment(sketch, "E69.2.0.72", {"start": v(1441.45, 1016) * mm, "end": v(1390.65, 1016) * mm});
            skLineSegment(sketch, "E69.2.0.73", {"start": v(1377.95, 254) * mm, "end": v(1327.15, 254) * mm});
            skLineSegment(sketch, "E69.2.0.74", {"start": v(1377.95, 508) * mm, "end": v(1327.15, 508) * mm});
            skLineSegment(sketch, "E69.2.0.75", {"start": v(1504.94, 762) * mm, "end": v(1454.14, 762) * mm});
            skLineSegment(sketch, "E69.2.0.76", {"start": v(1504.94, 1016) * mm, "end": v(1454.14, 1016) * mm});
            skLineSegment(sketch, "E69.2.0.77", {"start": v(1441.45, 254) * mm, "end": v(1390.65, 254) * mm});
            skLineSegment(sketch, "E69.2.0.78", {"start": v(1441.45, 508) * mm, "end": v(1390.65, 508) * mm});
            skLineSegment(sketch, "E69.2.0.79", {"start": v(1568.44, 762) * mm, "end": v(1517.64, 762) * mm});
            skLineSegment(sketch, "E69.2.0.80", {"start": v(1568.44, 1016) * mm, "end": v(1517.64, 1016) * mm});
            skLineSegment(sketch, "E69.2.0.81", {"start": v(1504.94, 254) * mm, "end": v(1454.14, 254) * mm});
            skLineSegment(sketch, "E69.2.0.82", {"start": v(1504.94, 508) * mm, "end": v(1454.14, 508) * mm});
            skLineSegment(sketch, "E69.2.0.83", {"start": v(1631.94, 762) * mm, "end": v(1581.14, 762) * mm});
            skLineSegment(sketch, "E69.2.0.84", {"start": v(1631.94, 1016) * mm, "end": v(1581.14, 1016) * mm});
            skLineSegment(sketch, "E69.2.0.85", {"start": v(1568.44, 254) * mm, "end": v(1517.64, 254) * mm});
            skLineSegment(sketch, "E69.2.0.86", {"start": v(1568.44, 508) * mm, "end": v(1517.64, 508) * mm});
            skLineSegment(sketch, "E69.2.0.87", {"start": v(1695.44, 1016) * mm, "end": v(1644.64, 1016) * mm});
            skLineSegment(sketch, "E69.2.0.88", {"start": v(1631.94, 254) * mm, "end": v(1581.14, 254) * mm});
            skLineSegment(sketch, "E69.2.0.89", {"start": v(1631.94, 508) * mm, "end": v(1581.14, 508) * mm});
            skLineSegment(sketch, "E69.2.0.90", {"start": v(1695.44, 254) * mm, "end": v(1644.64, 254) * mm});
            skLineSegment(sketch, "E69.2.0.91", {"start": v(1695.44, 508) * mm, "end": v(1644.64, 508) * mm});
            skLineSegment(sketch, "E69.2.0.92", {"start": v(1695.44, 762) * mm, "end": v(1644.64, 762) * mm});
            skLineSegment(sketch, "E69.2.0.93", {"start": v(1314.45, 762) * mm, "end": v(1263.65, 762) * mm});
            skLineSegment(sketch, "E69.2.0.94", {"start": v(1314.45, 1016) * mm, "end": v(1263.65, 1016) * mm});
            skLineSegment(sketch, "E69.2.0.95", {"start": v(1758.93, 254) * mm, "end": v(1708.13, 254) * mm});
            skLineSegment(sketch, "E69.2.0.96", {"start": v(1758.93, 508) * mm, "end": v(1708.13, 508) * mm});
            skLineSegment(sketch, "E69.2.0.97", {"start": v(1758.93, 762) * mm, "end": v(1708.13, 762) * mm});
            skLineSegment(sketch, "E69.2.0.98", {"start": v(1758.93, 1016) * mm, "end": v(1708.13, 1016) * mm});
            skLineSegment(sketch, "E69.2.0.99", {"start": v(1581.14, 76.2) * mm, "end": v(1581.14, 127) * mm});
            skLineSegment(sketch, "E69.2.0.100", {"start": v(1327.15, 76.2) * mm, "end": v(1327.15, 127) * mm});
            skLineSegment(sketch, "E69.2.0.101", {"start": v(1390.65, 711.2) * mm, "end": v(1390.65, 762) * mm});
            skLineSegment(sketch, "E69.2.0.102", {"start": v(1390.65, 965.2) * mm, "end": v(1390.65, 1016) * mm});
            skLineSegment(sketch, "E69.2.0.103", {"start": v(1327.15, 203.2) * mm, "end": v(1327.15, 254) * mm});
            skLineSegment(sketch, "E69.2.0.104", {"start": v(1327.15, 457.2) * mm, "end": v(1327.15, 508) * mm});
            skLineSegment(sketch, "E69.2.0.105", {"start": v(1454.14, 711.2) * mm, "end": v(1454.14, 762) * mm});
            skLineSegment(sketch, "E69.2.0.106", {"start": v(1454.14, 965.2) * mm, "end": v(1454.14, 1016) * mm});
            skLineSegment(sketch, "E69.2.0.107", {"start": v(1390.65, 203.2) * mm, "end": v(1390.65, 254) * mm});
            skLineSegment(sketch, "E69.2.0.108", {"start": v(1390.65, 457.2) * mm, "end": v(1390.65, 508) * mm});
            skLineSegment(sketch, "E69.2.0.109", {"start": v(1517.64, 711.2) * mm, "end": v(1517.64, 762) * mm});
            skLineSegment(sketch, "E69.2.0.110", {"start": v(1517.64, 965.2) * mm, "end": v(1517.64, 1016) * mm});
            skLineSegment(sketch, "E69.2.0.111", {"start": v(1454.14, 203.2) * mm, "end": v(1454.14, 254) * mm});
            skLineSegment(sketch, "E69.2.0.112", {"start": v(1454.14, 457.2) * mm, "end": v(1454.14, 508) * mm});
            skLineSegment(sketch, "E69.2.0.113", {"start": v(1581.14, 711.2) * mm, "end": v(1581.14, 762) * mm});
            skLineSegment(sketch, "E69.2.0.114", {"start": v(1581.14, 965.2) * mm, "end": v(1581.14, 1016) * mm});
            skLineSegment(sketch, "E69.2.0.115", {"start": v(1517.64, 203.2) * mm, "end": v(1517.64, 254) * mm});
            skLineSegment(sketch, "E69.2.0.116", {"start": v(1517.64, 457.2) * mm, "end": v(1517.64, 508) * mm});
            skLineSegment(sketch, "E69.2.0.117", {"start": v(1644.64, 965.2) * mm, "end": v(1644.64, 1016) * mm});
            skPoint(sketch, "E69.2.0.118", {"position": v(1511.3, 609.6) * mm});
            skLineSegment(sketch, "E69.2.0.119", {"start": v(1581.14, 203.2) * mm, "end": v(1581.14, 254) * mm});
            skLineSegment(sketch, "E69.2.0.120", {"start": v(1581.14, 457.2) * mm, "end": v(1581.14, 508) * mm});
            skLineSegment(sketch, "E69.2.0.121", {"start": v(1644.64, 203.2) * mm, "end": v(1644.64, 254) * mm});
            skLineSegment(sketch, "E69.2.0.122", {"start": v(1644.64, 457.2) * mm, "end": v(1644.64, 508) * mm});
            skLineSegment(sketch, "E69.2.0.123", {"start": v(1644.64, 711.2) * mm, "end": v(1644.64, 762) * mm});
            skLineSegment(sketch, "E69.2.0.124", {"start": v(1708.13, 203.2) * mm, "end": v(1708.13, 254) * mm});
            skLineSegment(sketch, "E69.2.0.125", {"start": v(1708.13, 457.2) * mm, "end": v(1708.13, 508) * mm});
            skLineSegment(sketch, "E69.2.0.126", {"start": v(1708.13, 711.2) * mm, "end": v(1708.13, 762) * mm});
            skLineSegment(sketch, "E69.2.0.127", {"start": v(1708.13, 965.2) * mm, "end": v(1708.13, 1016) * mm});
            skLineSegment(sketch, "E69.2.0.128", {"start": v(1263.65, 711.2) * mm, "end": v(1263.65, 762) * mm});
            skLineSegment(sketch, "E69.2.0.129", {"start": v(1263.65, 965.2) * mm, "end": v(1263.65, 1016) * mm});
            skLineSegment(sketch, "E69.2.0.130", {"start": v(1327.15, 711.2) * mm, "end": v(1327.15, 762) * mm});
            skLineSegment(sketch, "E69.2.0.131", {"start": v(1327.15, 965.2) * mm, "end": v(1327.15, 1016) * mm});
            skLineSegment(sketch, "E69.2.0.132", {"start": v(1263.65, 203.2) * mm, "end": v(1263.65, 254) * mm});
            skLineSegment(sketch, "E69.2.0.133", {"start": v(1263.65, 457.2) * mm, "end": v(1263.65, 508) * mm});
            skLineSegment(sketch, "E69.2.0.134", {"start": v(1631.94, 76.2) * mm, "end": v(1581.14, 76.2) * mm});
            skLineSegment(sketch, "E69.2.0.135", {"start": v(1377.95, 76.2) * mm, "end": v(1327.15, 76.2) * mm});
            skLineSegment(sketch, "E69.2.0.136", {"start": v(1504.94, 711.2) * mm, "end": v(1454.14, 711.2) * mm});
            skLineSegment(sketch, "E69.2.0.137", {"start": v(1441.45, 203.2) * mm, "end": v(1390.65, 203.2) * mm});
            skLineSegment(sketch, "E69.2.0.138", {"start": v(1441.45, 457.2) * mm, "end": v(1390.65, 457.2) * mm});
            skLineSegment(sketch, "E69.2.0.139", {"start": v(1568.44, 711.2) * mm, "end": v(1517.64, 711.2) * mm});
            skLineSegment(sketch, "E69.2.0.140", {"start": v(1568.44, 965.2) * mm, "end": v(1517.64, 965.2) * mm});
            skLineSegment(sketch, "E69.2.0.141", {"start": v(1504.94, 203.2) * mm, "end": v(1454.14, 203.2) * mm});
            skLineSegment(sketch, "E69.2.0.142", {"start": v(1504.94, 457.2) * mm, "end": v(1454.14, 457.2) * mm});
            skLineSegment(sketch, "E69.2.0.143", {"start": v(1631.94, 711.2) * mm, "end": v(1581.14, 711.2) * mm});
            skLineSegment(sketch, "E69.2.0.144", {"start": v(1631.94, 965.2) * mm, "end": v(1581.14, 965.2) * mm});
            skLineSegment(sketch, "E69.2.0.145", {"start": v(1568.44, 203.2) * mm, "end": v(1517.64, 203.2) * mm});
            skLineSegment(sketch, "E69.2.0.146", {"start": v(1568.44, 457.2) * mm, "end": v(1517.64, 457.2) * mm});
            skLineSegment(sketch, "E69.2.0.147", {"start": v(1695.44, 965.2) * mm, "end": v(1644.64, 965.2) * mm});
            skLineSegment(sketch, "E69.2.0.148", {"start": v(1631.94, 203.2) * mm, "end": v(1581.14, 203.2) * mm});
            skLineSegment(sketch, "E69.2.0.149", {"start": v(1631.94, 457.2) * mm, "end": v(1581.14, 457.2) * mm});
            skLineSegment(sketch, "E69.2.0.150", {"start": v(1695.44, 203.2) * mm, "end": v(1644.64, 203.2) * mm});
            skLineSegment(sketch, "E69.2.0.151", {"start": v(1695.44, 457.2) * mm, "end": v(1644.64, 457.2) * mm});
            skLineSegment(sketch, "E69.2.0.152", {"start": v(1695.44, 711.2) * mm, "end": v(1644.64, 711.2) * mm});
            skLineSegment(sketch, "E69.2.0.153", {"start": v(1758.93, 203.2) * mm, "end": v(1708.13, 203.2) * mm});
            skLineSegment(sketch, "E69.2.0.154", {"start": v(1758.93, 457.2) * mm, "end": v(1708.13, 457.2) * mm});
            skLineSegment(sketch, "E69.2.0.155", {"start": v(1758.93, 711.2) * mm, "end": v(1708.13, 711.2) * mm});
            skLineSegment(sketch, "E69.2.0.156", {"start": v(1758.93, 965.2) * mm, "end": v(1708.13, 965.2) * mm});
            skLineSegment(sketch, "E69.2.0.157", {"start": v(1695.44, 76.2) * mm, "end": v(1695.44, 127) * mm});
            skLineSegment(sketch, "E69.2.0.158", {"start": v(1441.45, 76.2) * mm, "end": v(1441.45, 127) * mm});
            skLineSegment(sketch, "E69.2.0.159", {"start": v(1314.45, 711.2) * mm, "end": v(1263.65, 711.2) * mm});
            skLineSegment(sketch, "E69.2.0.160", {"start": v(1377.95, 711.2) * mm, "end": v(1327.15, 711.2) * mm});
            skLineSegment(sketch, "E69.2.0.161", {"start": v(1377.95, 965.2) * mm, "end": v(1327.15, 965.2) * mm});
            skLineSegment(sketch, "E69.2.0.162", {"start": v(1314.45, 203.2) * mm, "end": v(1263.65, 203.2) * mm});
            skLineSegment(sketch, "E69.2.0.163", {"start": v(1314.45, 457.2) * mm, "end": v(1263.65, 457.2) * mm});
            skLineSegment(sketch, "E69.2.0.164", {"start": v(1441.45, 711.2) * mm, "end": v(1390.65, 711.2) * mm});
            skLineSegment(sketch, "E69.2.0.165", {"start": v(1441.45, 965.2) * mm, "end": v(1390.65, 965.2) * mm});
            skLineSegment(sketch, "E69.2.0.166", {"start": v(1377.95, 203.2) * mm, "end": v(1327.15, 203.2) * mm});
            skLineSegment(sketch, "E69.2.0.167", {"start": v(1377.95, 457.2) * mm, "end": v(1327.15, 457.2) * mm});
            skLineSegment(sketch, "E69.2.0.168", {"start": v(1568.44, 647.7) * mm, "end": v(1568.44, 698.5) * mm});
            skLineSegment(sketch, "E69.2.0.169", {"start": v(1568.44, 901.7) * mm, "end": v(1568.44, 952.5) * mm});
            skLineSegment(sketch, "E69.2.0.170", {"start": v(1504.94, 139.7) * mm, "end": v(1504.94, 190.5) * mm});
            skLineSegment(sketch, "E69.2.0.171", {"start": v(1504.94, 393.7) * mm, "end": v(1504.94, 444.5) * mm});
            skLineSegment(sketch, "E69.2.0.172", {"start": v(1631.94, 647.7) * mm, "end": v(1631.94, 698.5) * mm});
            skLineSegment(sketch, "E69.2.0.173", {"start": v(1631.94, 901.7) * mm, "end": v(1631.94, 952.5) * mm});
            skLineSegment(sketch, "E69.2.0.174", {"start": v(1568.44, 139.7) * mm, "end": v(1568.44, 190.5) * mm});
            skLineSegment(sketch, "E69.2.0.175", {"start": v(1568.44, 393.7) * mm, "end": v(1568.44, 444.5) * mm});
            skLineSegment(sketch, "E69.2.0.176", {"start": v(1695.44, 901.7) * mm, "end": v(1695.44, 952.5) * mm});
            skLineSegment(sketch, "E69.2.0.177", {"start": v(1631.94, 139.7) * mm, "end": v(1631.94, 190.5) * mm});
            skLineSegment(sketch, "E69.2.0.178", {"start": v(1631.94, 393.7) * mm, "end": v(1631.94, 444.5) * mm});
            skLineSegment(sketch, "E69.2.0.179", {"start": v(1695.44, 139.7) * mm, "end": v(1695.44, 190.5) * mm});
            skLineSegment(sketch, "E69.2.0.180", {"start": v(1695.44, 393.7) * mm, "end": v(1695.44, 444.5) * mm});
            skLineSegment(sketch, "E69.2.0.181", {"start": v(1695.44, 647.7) * mm, "end": v(1695.44, 698.5) * mm});
            skLineSegment(sketch, "E69.2.0.182", {"start": v(1758.93, 139.7) * mm, "end": v(1758.93, 190.5) * mm});
            skLineSegment(sketch, "E69.2.0.183", {"start": v(1758.93, 393.7) * mm, "end": v(1758.93, 444.5) * mm});
            skLineSegment(sketch, "E69.2.0.184", {"start": v(1758.93, 647.7) * mm, "end": v(1758.93, 698.5) * mm});
            skLineSegment(sketch, "E69.2.0.185", {"start": v(1758.93, 901.7) * mm, "end": v(1758.93, 952.5) * mm});
            skLineSegment(sketch, "E69.2.0.186", {"start": v(1695.44, 127) * mm, "end": v(1644.64, 127) * mm});
            skLineSegment(sketch, "E69.2.0.187", {"start": v(1441.45, 127) * mm, "end": v(1390.65, 127) * mm});
            skLineSegment(sketch, "E69.2.0.188", {"start": v(1314.45, 647.7) * mm, "end": v(1314.45, 698.5) * mm});
            skLineSegment(sketch, "E69.2.0.189", {"start": v(1314.45, 901.7) * mm, "end": v(1314.45, 952.5) * mm});
            skLineSegment(sketch, "E69.2.0.190", {"start": v(1377.95, 647.7) * mm, "end": v(1377.95, 698.5) * mm});
            skLineSegment(sketch, "E69.2.0.191", {"start": v(1377.95, 901.7) * mm, "end": v(1377.95, 952.5) * mm});
            skLineSegment(sketch, "E69.2.0.192", {"start": v(1314.45, 139.7) * mm, "end": v(1314.45, 190.5) * mm});
            skLineSegment(sketch, "E69.2.0.193", {"start": v(1314.45, 393.7) * mm, "end": v(1314.45, 444.5) * mm});
            skLineSegment(sketch, "E69.2.0.194", {"start": v(1441.45, 647.7) * mm, "end": v(1441.45, 698.5) * mm});
            skLineSegment(sketch, "E69.2.0.195", {"start": v(1441.45, 901.7) * mm, "end": v(1441.45, 952.5) * mm});
            skLineSegment(sketch, "E69.2.0.196", {"start": v(1377.95, 139.7) * mm, "end": v(1377.95, 190.5) * mm});
            skLineSegment(sketch, "E69.2.0.197", {"start": v(1377.95, 393.7) * mm, "end": v(1377.95, 444.5) * mm});
            skLineSegment(sketch, "E69.2.0.198", {"start": v(1504.94, 647.7) * mm, "end": v(1504.94, 698.5) * mm});
            skLineSegment(sketch, "E69.2.0.199", {"start": v(1504.94, 901.7) * mm, "end": v(1504.94, 952.5) * mm});
            skLineSegment(sketch, "E69.2.0.200", {"start": v(1441.45, 139.7) * mm, "end": v(1441.45, 190.5) * mm});
            skLineSegment(sketch, "E69.2.0.201", {"start": v(1441.45, 393.7) * mm, "end": v(1441.45, 444.5) * mm});
            skLineSegment(sketch, "E69.2.0.202", {"start": v(1631.94, 698.5) * mm, "end": v(1581.14, 698.5) * mm});
            skLineSegment(sketch, "E69.2.0.203", {"start": v(1631.94, 952.5) * mm, "end": v(1581.14, 952.5) * mm});
            skLineSegment(sketch, "E69.2.0.204", {"start": v(1568.44, 190.5) * mm, "end": v(1517.64, 190.5) * mm});
            skLineSegment(sketch, "E69.2.0.205", {"start": v(1568.44, 444.5) * mm, "end": v(1517.64, 444.5) * mm});
            skLineSegment(sketch, "E69.2.0.206", {"start": v(1695.44, 952.5) * mm, "end": v(1644.64, 952.5) * mm});
            skLineSegment(sketch, "E69.2.0.207", {"start": v(1631.94, 190.5) * mm, "end": v(1581.14, 190.5) * mm});
            skLineSegment(sketch, "E69.2.0.208", {"start": v(1631.94, 444.5) * mm, "end": v(1581.14, 444.5) * mm});
            skLineSegment(sketch, "E69.2.0.209", {"start": v(1695.44, 190.5) * mm, "end": v(1644.64, 190.5) * mm});
            skLineSegment(sketch, "E69.2.0.210", {"start": v(1695.44, 444.5) * mm, "end": v(1644.64, 444.5) * mm});
            skLineSegment(sketch, "E69.2.0.211", {"start": v(1695.44, 698.5) * mm, "end": v(1644.64, 698.5) * mm});
            skLineSegment(sketch, "E69.2.0.212", {"start": v(1758.93, 190.5) * mm, "end": v(1708.13, 190.5) * mm});
            skLineSegment(sketch, "E69.2.0.213", {"start": v(1758.93, 444.5) * mm, "end": v(1708.13, 444.5) * mm});
            skLineSegment(sketch, "E69.2.0.214", {"start": v(1758.93, 698.5) * mm, "end": v(1708.13, 698.5) * mm});
            skLineSegment(sketch, "E69.2.0.215", {"start": v(1758.93, 952.5) * mm, "end": v(1708.13, 952.5) * mm});
            skLineSegment(sketch, "E69.2.0.216", {"start": v(1644.64, 76.2) * mm, "end": v(1644.64, 127) * mm});
            skLineSegment(sketch, "E69.2.0.217", {"start": v(1390.65, 76.2) * mm, "end": v(1390.65, 127) * mm});
            skLineSegment(sketch, "E69.2.0.218", {"start": v(1314.45, 698.5) * mm, "end": v(1263.65, 698.5) * mm});
            skLineSegment(sketch, "E69.2.0.219", {"start": v(1377.95, 698.5) * mm, "end": v(1327.15, 698.5) * mm});
            skLineSegment(sketch, "E69.2.0.220", {"start": v(1377.95, 952.5) * mm, "end": v(1327.15, 952.5) * mm});
            skLineSegment(sketch, "E69.2.0.221", {"start": v(1314.45, 190.5) * mm, "end": v(1263.65, 190.5) * mm});
            skLineSegment(sketch, "E69.2.0.222", {"start": v(1314.45, 444.5) * mm, "end": v(1263.65, 444.5) * mm});
            skLineSegment(sketch, "E69.2.0.223", {"start": v(1441.45, 698.5) * mm, "end": v(1390.65, 698.5) * mm});
            skLineSegment(sketch, "E69.2.0.224", {"start": v(1441.45, 952.5) * mm, "end": v(1390.65, 952.5) * mm});
            skLineSegment(sketch, "E69.2.0.225", {"start": v(1377.95, 190.5) * mm, "end": v(1327.15, 190.5) * mm});
            skLineSegment(sketch, "E69.2.0.226", {"start": v(1377.95, 444.5) * mm, "end": v(1327.15, 444.5) * mm});
            skLineSegment(sketch, "E69.2.0.227", {"start": v(1504.94, 698.5) * mm, "end": v(1454.14, 698.5) * mm});
            skLineSegment(sketch, "E69.2.0.228", {"start": v(1441.45, 190.5) * mm, "end": v(1390.65, 190.5) * mm});
            skLineSegment(sketch, "E69.2.0.229", {"start": v(1441.45, 444.5) * mm, "end": v(1390.65, 444.5) * mm});
            skLineSegment(sketch, "E69.2.0.230", {"start": v(1568.44, 698.5) * mm, "end": v(1517.64, 698.5) * mm});
            skLineSegment(sketch, "E69.2.0.231", {"start": v(1568.44, 952.5) * mm, "end": v(1517.64, 952.5) * mm});
            skLineSegment(sketch, "E69.2.0.232", {"start": v(1504.94, 190.5) * mm, "end": v(1454.14, 190.5) * mm});
            skLineSegment(sketch, "E69.2.0.233", {"start": v(1504.94, 444.5) * mm, "end": v(1454.14, 444.5) * mm});
            skLineSegment(sketch, "E69.2.0.234", {"start": v(1644.64, 901.7) * mm, "end": v(1644.64, 952.5) * mm});
            skLineSegment(sketch, "E69.2.0.235", {"start": v(1581.14, 139.7) * mm, "end": v(1581.14, 190.5) * mm});
            skLineSegment(sketch, "E69.2.0.236", {"start": v(1581.14, 393.7) * mm, "end": v(1581.14, 444.5) * mm});
            skLineSegment(sketch, "E69.2.0.237", {"start": v(1644.64, 139.7) * mm, "end": v(1644.64, 190.5) * mm});
            skLineSegment(sketch, "E69.2.0.238", {"start": v(1644.64, 393.7) * mm, "end": v(1644.64, 444.5) * mm});
            skLineSegment(sketch, "E69.2.0.239", {"start": v(1644.64, 647.7) * mm, "end": v(1644.64, 698.5) * mm});
            skLineSegment(sketch, "E69.2.0.240", {"start": v(1708.13, 139.7) * mm, "end": v(1708.13, 190.5) * mm});
            skLineSegment(sketch, "E69.2.0.241", {"start": v(1708.13, 393.7) * mm, "end": v(1708.13, 444.5) * mm});
            skLineSegment(sketch, "E69.2.0.242", {"start": v(1708.13, 647.7) * mm, "end": v(1708.13, 698.5) * mm});
            skLineSegment(sketch, "E69.2.0.243", {"start": v(1708.13, 901.7) * mm, "end": v(1708.13, 952.5) * mm});
            skLineSegment(sketch, "E69.2.0.244", {"start": v(1695.44, 76.2) * mm, "end": v(1644.64, 76.2) * mm});
            skLineSegment(sketch, "E69.2.0.245", {"start": v(1441.45, 76.2) * mm, "end": v(1390.65, 76.2) * mm});
            skLineSegment(sketch, "E69.2.0.246", {"start": v(1263.65, 647.7) * mm, "end": v(1263.65, 698.5) * mm});
            skLineSegment(sketch, "E69.2.0.247", {"start": v(1263.65, 901.7) * mm, "end": v(1263.65, 952.5) * mm});
            skLineSegment(sketch, "E69.2.0.248", {"start": v(1327.15, 647.7) * mm, "end": v(1327.15, 698.5) * mm});
            skLineSegment(sketch, "E69.2.0.249", {"start": v(1327.15, 901.7) * mm, "end": v(1327.15, 952.5) * mm});
            skLineSegment(sketch, "E69.2.0.250", {"start": v(1263.65, 139.7) * mm, "end": v(1263.65, 190.5) * mm});
            skLineSegment(sketch, "E69.2.0.251", {"start": v(1263.65, 393.7) * mm, "end": v(1263.65, 444.5) * mm});
            skLineSegment(sketch, "E69.2.0.252", {"start": v(1390.65, 647.7) * mm, "end": v(1390.65, 698.5) * mm});
            skLineSegment(sketch, "E69.2.0.253", {"start": v(1390.65, 901.7) * mm, "end": v(1390.65, 952.5) * mm});
            skLineSegment(sketch, "E69.2.0.254", {"start": v(1327.15, 139.7) * mm, "end": v(1327.15, 190.5) * mm});
            skLineSegment(sketch, "E69.2.0.255", {"start": v(1327.15, 393.7) * mm, "end": v(1327.15, 444.5) * mm});
            skLineSegment(sketch, "E69.2.0.256", {"start": v(1454.14, 647.7) * mm, "end": v(1454.14, 698.5) * mm});
            skLineSegment(sketch, "E69.2.0.257", {"start": v(1454.14, 901.7) * mm, "end": v(1454.14, 952.5) * mm});
            skLineSegment(sketch, "E69.2.0.258", {"start": v(1390.65, 139.7) * mm, "end": v(1390.65, 190.5) * mm});
            skLineSegment(sketch, "E69.2.0.259", {"start": v(1390.65, 393.7) * mm, "end": v(1390.65, 444.5) * mm});
            skLineSegment(sketch, "E69.2.0.260", {"start": v(1517.64, 647.7) * mm, "end": v(1517.64, 698.5) * mm});
            skLineSegment(sketch, "E69.2.0.261", {"start": v(1517.64, 901.7) * mm, "end": v(1517.64, 952.5) * mm});
            skLineSegment(sketch, "E69.2.0.262", {"start": v(1454.14, 139.7) * mm, "end": v(1454.14, 190.5) * mm});
            skLineSegment(sketch, "E69.2.0.263", {"start": v(1454.14, 393.7) * mm, "end": v(1454.14, 444.5) * mm});
            skLineSegment(sketch, "E69.2.0.264", {"start": v(1581.14, 647.7) * mm, "end": v(1581.14, 698.5) * mm});
            skLineSegment(sketch, "E69.2.0.265", {"start": v(1581.14, 901.7) * mm, "end": v(1581.14, 952.5) * mm});
            skLineSegment(sketch, "E69.2.0.266", {"start": v(1517.64, 139.7) * mm, "end": v(1517.64, 190.5) * mm});
            skLineSegment(sketch, "E69.2.0.267", {"start": v(1517.64, 393.7) * mm, "end": v(1517.64, 444.5) * mm});
            skLineSegment(sketch, "E69.2.0.268", {"start": v(1758.93, 647.7) * mm, "end": v(1708.13, 647.7) * mm});
            skLineSegment(sketch, "E69.2.0.269", {"start": v(1758.93, 901.7) * mm, "end": v(1708.13, 901.7) * mm});
            skLineSegment(sketch, "E69.2.0.270", {"start": v(1695.44, 139.7) * mm, "end": v(1644.64, 139.7) * mm});
            skLineSegment(sketch, "E69.2.0.271", {"start": v(1695.44, 393.7) * mm, "end": v(1644.64, 393.7) * mm});
            skLineSegment(sketch, "E69.2.0.272", {"start": v(1758.93, 76.2) * mm, "end": v(1758.93, 127) * mm});
            skLineSegment(sketch, "E69.2.0.273", {"start": v(1504.94, 76.2) * mm, "end": v(1504.94, 127) * mm});
            skLineSegment(sketch, "E69.2.0.274", {"start": v(1758.93, 139.7) * mm, "end": v(1708.13, 139.7) * mm});
            skLineSegment(sketch, "E69.2.0.275", {"start": v(1758.93, 393.7) * mm, "end": v(1708.13, 393.7) * mm});
            skLineSegment(sketch, "E69.2.0.276", {"start": v(1314.45, 139.7) * mm, "end": v(1263.65, 139.7) * mm});
            skLineSegment(sketch, "E69.2.0.277", {"start": v(1314.45, 393.7) * mm, "end": v(1263.65, 393.7) * mm});
            skLineSegment(sketch, "E69.2.0.278", {"start": v(1314.45, 647.7) * mm, "end": v(1263.65, 647.7) * mm});
            skLineSegment(sketch, "E69.2.0.279", {"start": v(1314.45, 901.7) * mm, "end": v(1263.65, 901.7) * mm});
            skLineSegment(sketch, "E69.2.0.280", {"start": v(1377.95, 139.7) * mm, "end": v(1327.15, 139.7) * mm});
            skLineSegment(sketch, "E69.2.0.281", {"start": v(1377.95, 393.7) * mm, "end": v(1327.15, 393.7) * mm});
            skLineSegment(sketch, "E69.2.0.282", {"start": v(1377.95, 647.7) * mm, "end": v(1327.15, 647.7) * mm});
            skLineSegment(sketch, "E69.2.0.283", {"start": v(1377.95, 901.7) * mm, "end": v(1327.15, 901.7) * mm});
            skLineSegment(sketch, "E69.2.0.284", {"start": v(1441.45, 139.7) * mm, "end": v(1390.65, 139.7) * mm});
            skLineSegment(sketch, "E69.2.0.285", {"start": v(1441.45, 393.7) * mm, "end": v(1390.65, 393.7) * mm});
            skLineSegment(sketch, "E69.2.0.286", {"start": v(1441.45, 647.7) * mm, "end": v(1390.65, 647.7) * mm});
            skLineSegment(sketch, "E69.2.0.287", {"start": v(1441.45, 901.7) * mm, "end": v(1390.65, 901.7) * mm});
            skLineSegment(sketch, "E69.2.0.288", {"start": v(1504.94, 139.7) * mm, "end": v(1454.14, 139.7) * mm});
            skLineSegment(sketch, "E69.2.0.289", {"start": v(1504.94, 393.7) * mm, "end": v(1454.14, 393.7) * mm});
            skLineSegment(sketch, "E69.2.0.290", {"start": v(1504.94, 647.7) * mm, "end": v(1454.14, 647.7) * mm});
            skLineSegment(sketch, "E69.2.0.291", {"start": v(1504.94, 901.7) * mm, "end": v(1454.14, 901.7) * mm});
            skLineSegment(sketch, "E69.2.0.292", {"start": v(1568.44, 139.7) * mm, "end": v(1517.64, 139.7) * mm});
            skLineSegment(sketch, "E69.2.0.293", {"start": v(1568.44, 393.7) * mm, "end": v(1517.64, 393.7) * mm});
            skLineSegment(sketch, "E69.2.0.294", {"start": v(1568.44, 647.7) * mm, "end": v(1517.64, 647.7) * mm});
            skLineSegment(sketch, "E69.2.0.295", {"start": v(1568.44, 901.7) * mm, "end": v(1517.64, 901.7) * mm});
            skLineSegment(sketch, "E69.2.0.296", {"start": v(1631.94, 139.7) * mm, "end": v(1581.14, 139.7) * mm});
            skLineSegment(sketch, "E69.2.0.297", {"start": v(1631.94, 393.7) * mm, "end": v(1581.14, 393.7) * mm});
            skLineSegment(sketch, "E69.2.0.298", {"start": v(1631.94, 647.7) * mm, "end": v(1581.14, 647.7) * mm});
            skLineSegment(sketch, "E69.2.0.299", {"start": v(1631.94, 901.7) * mm, "end": v(1581.14, 901.7) * mm});
            skLineSegment(sketch, "E69.2.0.300", {"start": v(1695.44, 901.7) * mm, "end": v(1644.64, 901.7) * mm});
            skLineSegment(sketch, "E69.2.0.301", {"start": v(1695.44, 647.7) * mm, "end": v(1644.64, 647.7) * mm});
            skLineSegment(sketch, "E69.2.0.302", {"start": v(1377.95, 1092.2) * mm, "end": v(1377.95, 1143) * mm});
            skLineSegment(sketch, "E69.2.0.303", {"start": v(1314.45, 330.2) * mm, "end": v(1314.45, 381) * mm});
            skLineSegment(sketch, "E69.2.0.304", {"start": v(1314.45, 584.2) * mm, "end": v(1314.45, 635) * mm});
            skLineSegment(sketch, "E69.2.0.305", {"start": v(1314.45, 838.2) * mm, "end": v(1314.45, 889) * mm});
            skLineSegment(sketch, "E69.2.0.306", {"start": v(1758.93, 127) * mm, "end": v(1708.13, 127) * mm});
            skLineSegment(sketch, "E69.2.0.307", {"start": v(1504.94, 127) * mm, "end": v(1454.14, 127) * mm});
            skLineSegment(sketch, "E69.2.0.308", {"start": v(1277.58, 1054.37) * mm, "end": v(1369.55, 1054.37) * mm, "construction": true});
            skLineSegment(sketch, "E69.2.0.309", {"start": v(1758.93, 330.2) * mm, "end": v(1758.93, 381) * mm});
            skLineSegment(sketch, "E69.2.0.310", {"start": v(1441.45, 1092.2) * mm, "end": v(1441.45, 1143) * mm});
            skLineSegment(sketch, "E69.2.0.311", {"start": v(1377.95, 330.2) * mm, "end": v(1377.95, 381) * mm});
            skLineSegment(sketch, "E69.2.0.312", {"start": v(1377.95, 584.2) * mm, "end": v(1377.95, 635) * mm});
            skLineSegment(sketch, "E69.2.0.313", {"start": v(1377.95, 838.2) * mm, "end": v(1377.95, 889) * mm});
            skLineSegment(sketch, "E69.2.0.314", {"start": v(1504.94, 1092.2) * mm, "end": v(1504.94, 1143) * mm});
            skLineSegment(sketch, "E69.2.0.315", {"start": v(1441.45, 330.2) * mm, "end": v(1441.45, 381) * mm});
            skLineSegment(sketch, "E69.2.0.316", {"start": v(1441.45, 584.2) * mm, "end": v(1441.45, 635) * mm});
            skLineSegment(sketch, "E69.2.0.317", {"start": v(1441.45, 838.2) * mm, "end": v(1441.45, 889) * mm});
            skLineSegment(sketch, "E69.2.0.318", {"start": v(1568.44, 1092.2) * mm, "end": v(1568.44, 1143) * mm});
            skLineSegment(sketch, "E69.2.0.319", {"start": v(1504.94, 330.2) * mm, "end": v(1504.94, 381) * mm});
            skLineSegment(sketch, "E69.2.0.320", {"start": v(1504.94, 838.2) * mm, "end": v(1504.94, 889) * mm});
            skLineSegment(sketch, "E69.2.0.321", {"start": v(1631.94, 1092.2) * mm, "end": v(1631.94, 1143) * mm});
            skLineSegment(sketch, "E69.2.0.322", {"start": v(1568.44, 330.2) * mm, "end": v(1568.44, 381) * mm});
            skLineSegment(sketch, "E69.2.0.323", {"start": v(1568.44, 584.2) * mm, "end": v(1568.44, 635) * mm});
            skLineSegment(sketch, "E69.2.0.324", {"start": v(1568.44, 838.2) * mm, "end": v(1568.44, 889) * mm});
            skLineSegment(sketch, "E69.2.0.325", {"start": v(1695.44, 1092.2) * mm, "end": v(1695.44, 1143) * mm});
            skLineSegment(sketch, "E69.2.0.326", {"start": v(1631.94, 330.2) * mm, "end": v(1631.94, 381) * mm});
            skLineSegment(sketch, "E69.2.0.327", {"start": v(1631.94, 584.2) * mm, "end": v(1631.94, 635) * mm});
            skLineSegment(sketch, "E69.2.0.328", {"start": v(1631.94, 838.2) * mm, "end": v(1631.94, 889) * mm});
            skLineSegment(sketch, "E69.2.0.329", {"start": v(1695.44, 838.2) * mm, "end": v(1695.44, 889) * mm});
            skLineSegment(sketch, "E69.2.0.330", {"start": v(1695.44, 584.2) * mm, "end": v(1695.44, 635) * mm});
            skLineSegment(sketch, "E69.2.0.331", {"start": v(1758.93, 838.2) * mm, "end": v(1758.93, 889) * mm});
            skLineSegment(sketch, "E69.2.0.332", {"start": v(1758.93, 1092.2) * mm, "end": v(1758.93, 1143) * mm});
            skLineSegment(sketch, "E69.2.0.333", {"start": v(1695.44, 330.2) * mm, "end": v(1695.44, 381) * mm});
            skLineSegment(sketch, "E69.2.0.334", {"start": v(1377.95, 1143) * mm, "end": v(1327.15, 1143) * mm});
            skLineSegment(sketch, "E69.2.0.335", {"start": v(1314.45, 381) * mm, "end": v(1263.65, 381) * mm});
            skLineSegment(sketch, "E69.2.0.336", {"start": v(1314.45, 635) * mm, "end": v(1263.65, 635) * mm});
            skLineSegment(sketch, "E69.2.0.337", {"start": v(1314.45, 889) * mm, "end": v(1263.65, 889) * mm});
            skLineSegment(sketch, "E69.2.0.338", {"start": v(1441.45, 1143) * mm, "end": v(1390.65, 1143) * mm});
            skLineSegment(sketch, "E69.2.0.339", {"start": v(1377.95, 381) * mm, "end": v(1327.15, 381) * mm});
            skLineSegment(sketch, "E69.2.0.340", {"start": v(1377.95, 635) * mm, "end": v(1327.15, 635) * mm});
            skLineSegment(sketch, "E69.2.0.341", {"start": v(1377.95, 889) * mm, "end": v(1327.15, 889) * mm});
            skLineSegment(sketch, "E69.2.0.342", {"start": v(1504.94, 1143) * mm, "end": v(1454.14, 1143) * mm});
            skLineSegment(sketch, "E69.2.0.343", {"start": v(1441.45, 381) * mm, "end": v(1390.65, 381) * mm});
            skLineSegment(sketch, "E69.2.0.344", {"start": v(1441.45, 635) * mm, "end": v(1390.65, 635) * mm});
            skLineSegment(sketch, "E69.2.0.345", {"start": v(1441.45, 889) * mm, "end": v(1390.65, 889) * mm});
            skLineSegment(sketch, "E69.2.0.346", {"start": v(1568.44, 1143) * mm, "end": v(1517.64, 1143) * mm});
            skLineSegment(sketch, "E69.2.0.347", {"start": v(1504.94, 381) * mm, "end": v(1454.14, 381) * mm});
            skLineSegment(sketch, "E69.2.0.348", {"start": v(1504.94, 635) * mm, "end": v(1454.14, 635) * mm});
            skLineSegment(sketch, "E69.2.0.349", {"start": v(1504.94, 889) * mm, "end": v(1454.14, 889) * mm});
            skLineSegment(sketch, "E69.2.0.350", {"start": v(1631.94, 1143) * mm, "end": v(1581.14, 1143) * mm});
            skLineSegment(sketch, "E69.2.0.351", {"start": v(1568.44, 381) * mm, "end": v(1517.64, 381) * mm});
            skLineSegment(sketch, "E69.2.0.352", {"start": v(1568.44, 635) * mm, "end": v(1517.64, 635) * mm});
            skLineSegment(sketch, "E69.2.0.353", {"start": v(1568.44, 889) * mm, "end": v(1517.64, 889) * mm});
            skLineSegment(sketch, "E69.2.0.354", {"start": v(1695.44, 1143) * mm, "end": v(1644.64, 1143) * mm});
            skLineSegment(sketch, "E69.2.0.355", {"start": v(1631.94, 381) * mm, "end": v(1581.14, 381) * mm});
            skLineSegment(sketch, "E69.2.0.356", {"start": v(1631.94, 635) * mm, "end": v(1581.14, 635) * mm});
            skLineSegment(sketch, "E69.2.0.357", {"start": v(1631.94, 889) * mm, "end": v(1581.14, 889) * mm});
            skLineSegment(sketch, "E69.2.0.358", {"start": v(1695.44, 889) * mm, "end": v(1644.64, 889) * mm});
            skLineSegment(sketch, "E69.2.0.359", {"start": v(1695.44, 635) * mm, "end": v(1644.64, 635) * mm});
            skLineSegment(sketch, "E69.2.0.360", {"start": v(1758.93, 635) * mm, "end": v(1708.13, 635) * mm});
            skLineSegment(sketch, "E69.2.0.361", {"start": v(1758.93, 889) * mm, "end": v(1708.13, 889) * mm});
            skLineSegment(sketch, "E69.2.0.362", {"start": v(1758.93, 1143) * mm, "end": v(1708.13, 1143) * mm});
            skLineSegment(sketch, "E69.2.0.363", {"start": v(1695.44, 381) * mm, "end": v(1644.64, 381) * mm});
            skLineSegment(sketch, "E69.2.0.364", {"start": v(1708.13, 76.2) * mm, "end": v(1708.13, 127) * mm});
            skLineSegment(sketch, "E69.2.0.365", {"start": v(1454.14, 76.2) * mm, "end": v(1454.14, 127) * mm});
            skLineSegment(sketch, "E69.2.0.366", {"start": v(1277.58, 1054.37) * mm, "end": v(1277.58, 952.93) * mm, "construction": true});
            skLineSegment(sketch, "E69.2.0.367", {"start": v(1758.93, 381) * mm, "end": v(1708.13, 381) * mm});
            skLineSegment(sketch, "E69.2.0.368", {"start": v(1327.15, 1092.2) * mm, "end": v(1327.15, 1143) * mm});
            skLineSegment(sketch, "E69.2.0.369", {"start": v(1263.65, 330.2) * mm, "end": v(1263.65, 381) * mm});
            skLineSegment(sketch, "E69.2.0.370", {"start": v(1263.65, 838.2) * mm, "end": v(1263.65, 889) * mm});
            skLineSegment(sketch, "E69.2.0.371", {"start": v(1390.65, 1092.2) * mm, "end": v(1390.65, 1143) * mm});
            skLineSegment(sketch, "E69.2.0.372", {"start": v(1327.15, 330.2) * mm, "end": v(1327.15, 381) * mm});
            skLineSegment(sketch, "E69.2.0.373", {"start": v(1327.15, 584.2) * mm, "end": v(1327.15, 635) * mm});
            skLineSegment(sketch, "E69.2.0.374", {"start": v(1327.15, 838.2) * mm, "end": v(1327.15, 889) * mm});
            skLineSegment(sketch, "E69.2.0.375", {"start": v(1454.14, 1092.2) * mm, "end": v(1454.14, 1143) * mm});
            skLineSegment(sketch, "E69.2.0.376", {"start": v(1390.65, 330.2) * mm, "end": v(1390.65, 381) * mm});
            skLineSegment(sketch, "E69.2.0.377", {"start": v(1390.65, 584.2) * mm, "end": v(1390.65, 635) * mm});
            skLineSegment(sketch, "E69.2.0.378", {"start": v(1390.65, 838.2) * mm, "end": v(1390.65, 889) * mm});
            skLineSegment(sketch, "E69.2.0.379", {"start": v(1517.64, 1092.2) * mm, "end": v(1517.64, 1143) * mm});
            skLineSegment(sketch, "E69.2.0.380", {"start": v(1454.14, 330.2) * mm, "end": v(1454.14, 381) * mm});
            skLineSegment(sketch, "E69.2.0.381", {"start": v(1454.14, 584.2) * mm, "end": v(1454.14, 635) * mm});
            skLineSegment(sketch, "E69.2.0.382", {"start": v(1454.14, 838.2) * mm, "end": v(1454.14, 889) * mm});
            skLineSegment(sketch, "E69.2.0.383", {"start": v(1581.14, 1092.2) * mm, "end": v(1581.14, 1143) * mm});
            skLineSegment(sketch, "E69.2.0.384", {"start": v(1517.64, 330.2) * mm, "end": v(1517.64, 381) * mm});
            skLineSegment(sketch, "E69.2.0.385", {"start": v(1517.64, 838.2) * mm, "end": v(1517.64, 889) * mm});
            skLineSegment(sketch, "E69.2.0.386", {"start": v(1644.64, 1092.2) * mm, "end": v(1644.64, 1143) * mm});
            skLineSegment(sketch, "E69.2.0.387", {"start": v(1581.14, 330.2) * mm, "end": v(1581.14, 381) * mm});
            skLineSegment(sketch, "E69.2.0.388", {"start": v(1581.14, 584.2) * mm, "end": v(1581.14, 635) * mm});
            skLineSegment(sketch, "E69.2.0.389", {"start": v(1581.14, 838.2) * mm, "end": v(1581.14, 889) * mm});
            skLineSegment(sketch, "E69.2.0.390", {"start": v(1644.64, 838.2) * mm, "end": v(1644.64, 889) * mm});
            skLineSegment(sketch, "E69.2.0.391", {"start": v(1644.64, 584.2) * mm, "end": v(1644.64, 635) * mm});
            skLineSegment(sketch, "E69.2.0.392", {"start": v(1708.13, 584.2) * mm, "end": v(1708.13, 635) * mm});
            skLineSegment(sketch, "E69.2.0.393", {"start": v(1708.13, 838.2) * mm, "end": v(1708.13, 889) * mm});
            skLineSegment(sketch, "E69.2.0.394", {"start": v(1708.13, 1092.2) * mm, "end": v(1708.13, 1143) * mm});
            skLineSegment(sketch, "E69.2.0.395", {"start": v(1644.64, 330.2) * mm, "end": v(1644.64, 381) * mm});
            skLineSegment(sketch, "E69.2.0.396", {"start": v(1504.94, 76.2) * mm, "end": v(1454.14, 76.2) * mm});
            skLineSegment(sketch, "E69.2.0.397", {"start": v(1263.65, 266.7) * mm, "end": v(1847.85, 266.7) * mm, "construction": true});
            skLineSegment(sketch, "E69.2.0.398", {"start": v(1708.13, 330.2) * mm, "end": v(1708.13, 381) * mm});
            skLineSegment(sketch, "E69.2.0.399", {"start": v(1377.95, 1092.2) * mm, "end": v(1327.15, 1092.2) * mm});
            skLineSegment(sketch, "E69.2.0.400", {"start": v(1314.45, 330.2) * mm, "end": v(1263.65, 330.2) * mm});
            skLineSegment(sketch, "E69.2.0.401", {"start": v(1314.45, 584.2) * mm, "end": v(1263.65, 584.2) * mm});
            skLineSegment(sketch, "E69.2.0.402", {"start": v(1314.45, 838.2) * mm, "end": v(1263.65, 838.2) * mm});
            skLineSegment(sketch, "E69.2.0.403", {"start": v(1441.45, 1092.2) * mm, "end": v(1390.65, 1092.2) * mm});
            skLineSegment(sketch, "E69.2.0.404", {"start": v(1377.95, 330.2) * mm, "end": v(1327.15, 330.2) * mm});
            skLineSegment(sketch, "E69.2.0.405", {"start": v(1377.95, 584.2) * mm, "end": v(1327.15, 584.2) * mm});
            skLineSegment(sketch, "E69.2.0.406", {"start": v(1377.95, 838.2) * mm, "end": v(1327.15, 838.2) * mm});
            skLineSegment(sketch, "E69.2.0.407", {"start": v(1504.94, 1092.2) * mm, "end": v(1454.14, 1092.2) * mm});
            skLineSegment(sketch, "E69.2.0.408", {"start": v(1441.45, 330.2) * mm, "end": v(1390.65, 330.2) * mm});
            skLineSegment(sketch, "E69.2.0.409", {"start": v(1441.45, 584.2) * mm, "end": v(1390.65, 584.2) * mm});
            skLineSegment(sketch, "E69.2.0.410", {"start": v(1441.45, 838.2) * mm, "end": v(1390.65, 838.2) * mm});
            skLineSegment(sketch, "E69.2.0.411", {"start": v(1568.44, 1092.2) * mm, "end": v(1517.64, 1092.2) * mm});
            skLineSegment(sketch, "E69.2.0.412", {"start": v(1504.94, 330.2) * mm, "end": v(1454.14, 330.2) * mm});
            skLineSegment(sketch, "E69.2.0.413", {"start": v(1504.94, 584.2) * mm, "end": v(1454.14, 584.2) * mm});
            skLineSegment(sketch, "E69.2.0.414", {"start": v(1504.94, 838.2) * mm, "end": v(1454.14, 838.2) * mm});
            skLineSegment(sketch, "E69.2.0.415", {"start": v(1631.94, 1092.2) * mm, "end": v(1581.14, 1092.2) * mm});
            skLineSegment(sketch, "E69.2.0.416", {"start": v(1568.44, 330.2) * mm, "end": v(1517.64, 330.2) * mm});
            skLineSegment(sketch, "E69.2.0.417", {"start": v(1568.44, 584.2) * mm, "end": v(1517.64, 584.2) * mm});
            skLineSegment(sketch, "E69.2.0.418", {"start": v(1568.44, 838.2) * mm, "end": v(1517.64, 838.2) * mm});
            skLineSegment(sketch, "E69.2.0.419", {"start": v(1695.44, 1092.2) * mm, "end": v(1644.64, 1092.2) * mm});
            skLineSegment(sketch, "E69.2.0.420", {"start": v(1631.94, 330.2) * mm, "end": v(1581.14, 330.2) * mm});
            skLineSegment(sketch, "E69.2.0.421", {"start": v(1631.94, 584.2) * mm, "end": v(1581.14, 584.2) * mm});
            skLineSegment(sketch, "E69.2.0.422", {"start": v(1631.94, 838.2) * mm, "end": v(1581.14, 838.2) * mm});
            skLineSegment(sketch, "E69.2.0.423", {"start": v(1695.44, 838.2) * mm, "end": v(1644.64, 838.2) * mm});
            skLineSegment(sketch, "E69.2.0.424", {"start": v(1695.44, 584.2) * mm, "end": v(1644.64, 584.2) * mm});
            skLineSegment(sketch, "E69.2.0.425", {"start": v(1758.93, 584.2) * mm, "end": v(1708.13, 584.2) * mm});
            skLineSegment(sketch, "E69.2.0.426", {"start": v(1758.93, 838.2) * mm, "end": v(1708.13, 838.2) * mm});
            skLineSegment(sketch, "E69.2.0.427", {"start": v(1758.93, 1092.2) * mm, "end": v(1708.13, 1092.2) * mm});
            skLineSegment(sketch, "E69.2.0.428", {"start": v(1695.44, 330.2) * mm, "end": v(1644.64, 330.2) * mm});
            skLineSegment(sketch, "E69.2.0.429", {"start": v(1454.14, 127) * mm, "end": v(2038.7, 127) * mm, "construction": true});
            skLineSegment(sketch, "E69.2.0.430", {"start": v(1314.45, 76.2) * mm, "end": v(1314.45, 127) * mm});
            skLineSegment(sketch, "E69.2.0.431", {"start": v(1758.93, 330.2) * mm, "end": v(1708.13, 330.2) * mm});
            skLineSegment(sketch, "E69.2.0.432", {"start": v(1314.45, 266.7) * mm, "end": v(1314.45, 317.5) * mm});
            skLineSegment(sketch, "E69.2.0.433", {"start": v(1314.45, 520.7) * mm, "end": v(1314.45, 571.5) * mm});
            skLineSegment(sketch, "E69.2.0.434", {"start": v(1314.45, 774.7) * mm, "end": v(1314.45, 825.5) * mm});
            skLineSegment(sketch, "E69.2.0.435", {"start": v(1441.45, 1028.7) * mm, "end": v(1441.45, 1079.5) * mm});
            skLineSegment(sketch, "E69.2.0.436", {"start": v(1377.95, 266.7) * mm, "end": v(1377.95, 317.5) * mm});
            skLineSegment(sketch, "E69.2.0.437", {"start": v(1377.95, 520.7) * mm, "end": v(1377.95, 571.5) * mm});
            skLineSegment(sketch, "E69.2.0.438", {"start": v(1377.95, 774.7) * mm, "end": v(1377.95, 825.5) * mm});
            skLineSegment(sketch, "E69.2.0.439", {"start": v(1504.94, 1028.7) * mm, "end": v(1504.94, 1079.5) * mm});
            skLineSegment(sketch, "E69.2.0.440", {"start": v(1441.45, 266.7) * mm, "end": v(1441.45, 317.5) * mm});
            skLineSegment(sketch, "E69.2.0.441", {"start": v(1441.45, 520.7) * mm, "end": v(1441.45, 571.5) * mm});
            skLineSegment(sketch, "E69.2.0.442", {"start": v(1441.45, 774.7) * mm, "end": v(1441.45, 825.5) * mm});
            skLineSegment(sketch, "E69.2.0.443", {"start": v(1568.44, 1028.7) * mm, "end": v(1568.44, 1079.5) * mm});
            skLineSegment(sketch, "E69.2.0.444", {"start": v(1504.94, 266.7) * mm, "end": v(1504.94, 317.5) * mm});
            skLineSegment(sketch, "E69.2.0.445", {"start": v(1504.94, 520.7) * mm, "end": v(1504.94, 571.5) * mm});
            skLineSegment(sketch, "E69.2.0.446", {"start": v(1504.94, 774.7) * mm, "end": v(1504.94, 825.5) * mm});
            skLineSegment(sketch, "E69.2.0.447", {"start": v(1631.94, 1028.7) * mm, "end": v(1631.94, 1079.5) * mm});
            skLineSegment(sketch, "E69.2.0.448", {"start": v(1568.44, 266.7) * mm, "end": v(1568.44, 317.5) * mm});
            skLineSegment(sketch, "E69.2.0.449", {"start": v(1568.44, 520.7) * mm, "end": v(1568.44, 571.5) * mm});
            skLineSegment(sketch, "E69.2.0.450", {"start": v(1568.44, 774.7) * mm, "end": v(1568.44, 825.5) * mm});
            skLineSegment(sketch, "E69.2.0.451", {"start": v(1695.44, 1028.7) * mm, "end": v(1695.44, 1079.5) * mm});
            skLineSegment(sketch, "E69.2.0.452", {"start": v(1631.94, 266.7) * mm, "end": v(1631.94, 317.5) * mm});
            skLineSegment(sketch, "E69.2.0.453", {"start": v(1631.94, 520.7) * mm, "end": v(1631.94, 571.5) * mm});
            skLineSegment(sketch, "E69.2.0.454", {"start": v(1631.94, 774.7) * mm, "end": v(1631.94, 825.5) * mm});
            skLineSegment(sketch, "E69.2.0.455", {"start": v(1695.44, 774.7) * mm, "end": v(1695.44, 825.5) * mm});
            skLineSegment(sketch, "E69.2.0.456", {"start": v(1695.44, 520.7) * mm, "end": v(1695.44, 571.5) * mm});
            skLineSegment(sketch, "E69.2.0.457", {"start": v(1758.93, 520.7) * mm, "end": v(1758.93, 571.5) * mm});
            skLineSegment(sketch, "E69.2.0.458", {"start": v(1758.93, 774.7) * mm, "end": v(1758.93, 825.5) * mm});
            skLineSegment(sketch, "E69.2.0.459", {"start": v(1758.93, 1028.7) * mm, "end": v(1758.93, 1079.5) * mm});
            skLineSegment(sketch, "E69.2.0.460", {"start": v(1695.44, 266.7) * mm, "end": v(1695.44, 317.5) * mm});
            skLineSegment(sketch, "E69.2.0.461", {"start": v(1568.44, 127) * mm, "end": v(1517.64, 127) * mm});
            skLineSegment(sketch, "E69.2.0.462", {"start": v(1314.45, 127) * mm, "end": v(1263.65, 127) * mm});
            skLineSegment(sketch, "E69.2.0.463", {"start": v(1758.93, 266.7) * mm, "end": v(1758.93, 317.5) * mm});
            skPoint(sketch, "E69.2.0.464", {"position": v(1289.05, 1117.6) * mm});
            skLineSegment(sketch, "E69.2.0.465", {"start": v(1568.44, 825.5) * mm, "end": v(1517.64, 825.5) * mm});
            skLineSegment(sketch, "E69.2.0.466", {"start": v(1568.44, 1079.5) * mm, "end": v(1517.64, 1079.5) * mm});
            skLineSegment(sketch, "E69.2.0.467", {"start": v(1504.94, 317.5) * mm, "end": v(1454.14, 317.5) * mm});
            skLineSegment(sketch, "E69.2.0.468", {"start": v(1504.94, 571.5) * mm, "end": v(1454.14, 571.5) * mm});
            skLineSegment(sketch, "E69.2.0.469", {"start": v(1631.94, 825.5) * mm, "end": v(1581.14, 825.5) * mm});
            skLineSegment(sketch, "E69.2.0.470", {"start": v(1631.94, 1079.5) * mm, "end": v(1581.14, 1079.5) * mm});
            skLineSegment(sketch, "E69.2.0.471", {"start": v(1568.44, 317.5) * mm, "end": v(1517.64, 317.5) * mm});
            skLineSegment(sketch, "E69.2.0.472", {"start": v(1568.44, 571.5) * mm, "end": v(1517.64, 571.5) * mm});
            skLineSegment(sketch, "E69.2.0.473", {"start": v(1695.44, 825.5) * mm, "end": v(1644.64, 825.5) * mm});
            skLineSegment(sketch, "E69.2.0.474", {"start": v(1695.44, 1079.5) * mm, "end": v(1644.64, 1079.5) * mm});
            skLineSegment(sketch, "E69.2.0.475", {"start": v(1631.94, 317.5) * mm, "end": v(1581.14, 317.5) * mm});
            skLineSegment(sketch, "E69.2.0.476", {"start": v(1631.94, 571.5) * mm, "end": v(1581.14, 571.5) * mm});
            skLineSegment(sketch, "E69.2.0.477", {"start": v(1695.44, 317.5) * mm, "end": v(1644.64, 317.5) * mm});
            skLineSegment(sketch, "E69.2.0.478", {"start": v(1695.44, 571.5) * mm, "end": v(1644.64, 571.5) * mm});
            skLineSegment(sketch, "E69.2.0.479", {"start": v(1758.93, 317.5) * mm, "end": v(1708.13, 317.5) * mm});
            skLineSegment(sketch, "E69.2.0.480", {"start": v(1758.93, 571.5) * mm, "end": v(1708.13, 571.5) * mm});
            skLineSegment(sketch, "E69.2.0.481", {"start": v(1758.93, 825.5) * mm, "end": v(1708.13, 825.5) * mm});
            skLineSegment(sketch, "E69.2.0.482", {"start": v(1758.93, 1079.5) * mm, "end": v(1708.13, 1079.5) * mm});
            skLineSegment(sketch, "E69.2.0.483", {"start": v(1517.64, 76.2) * mm, "end": v(1517.64, 127) * mm});
            skLineSegment(sketch, "E69.2.0.484", {"start": v(1263.65, 76.2) * mm, "end": v(1263.65, 127) * mm});
            skLineSegment(sketch, "E69.2.0.485", {"start": v(1314.45, 825.5) * mm, "end": v(1263.65, 825.5) * mm});
            skLineSegment(sketch, "E69.2.0.486", {"start": v(1377.95, 825.5) * mm, "end": v(1327.15, 825.5) * mm});
            skLineSegment(sketch, "E69.2.0.487", {"start": v(1377.95, 1079.5) * mm, "end": v(1327.15, 1079.5) * mm});
            skLineSegment(sketch, "E69.2.0.488", {"start": v(1314.45, 317.5) * mm, "end": v(1263.65, 317.5) * mm});
            skLineSegment(sketch, "E69.2.0.489", {"start": v(1314.45, 571.5) * mm, "end": v(1263.65, 571.5) * mm});
            skLineSegment(sketch, "E69.2.0.490", {"start": v(1441.45, 825.5) * mm, "end": v(1390.65, 825.5) * mm});
            skLineSegment(sketch, "E69.2.0.491", {"start": v(1441.45, 1079.5) * mm, "end": v(1390.65, 1079.5) * mm});
            skLineSegment(sketch, "E69.2.0.492", {"start": v(1377.95, 317.5) * mm, "end": v(1327.15, 317.5) * mm});
            skLineSegment(sketch, "E69.2.0.493", {"start": v(1377.95, 571.5) * mm, "end": v(1327.15, 571.5) * mm});
            skLineSegment(sketch, "E69.2.0.494", {"start": v(1504.94, 825.5) * mm, "end": v(1454.14, 825.5) * mm});
            skLineSegment(sketch, "E69.2.0.495", {"start": v(1504.94, 1079.5) * mm, "end": v(1454.14, 1079.5) * mm});
            skLineSegment(sketch, "E69.2.0.496", {"start": v(1441.45, 317.5) * mm, "end": v(1390.65, 317.5) * mm});
            skLineSegment(sketch, "E69.2.0.497", {"start": v(1441.45, 571.5) * mm, "end": v(1390.65, 571.5) * mm});
            skLineSegment(sketch, "E69.2.0.498", {"start": v(1314.45, 1079.5) * mm, "end": v(1263.65, 1079.5) * mm});
            skLineSegment(sketch, "E69.2.0.499", {"start": v(1314.45, 1028.7) * mm, "end": v(1263.65, 1028.7) * mm});
            skLineSegment(sketch, "E69.2.0.500", {"start": v(1771.65, 1155.7) * mm, "end": v(1250.95, 1155.7) * mm});
            skLineSegment(sketch, "E69.2.0.501", {"start": v(1771.65, 63.5) * mm, "end": v(1250.95, 63.5) * mm});
            skLineSegment(sketch, "E69.2.0.502", {"start": v(1771.65, 1155.7) * mm, "end": v(1771.65, 63.5) * mm});
            skLineSegment(sketch, "E69.2.0.503", {"start": v(1250.95, 1155.7) * mm, "end": v(1250.95, 63.5) * mm});
            skLineSegment(sketch, "E69.2.0.504", {"start": v(1581.14, 774.7) * mm, "end": v(1581.14, 825.5) * mm});
            skLineSegment(sketch, "E69.2.0.505", {"start": v(1581.14, 1028.7) * mm, "end": v(1581.14, 1079.5) * mm});
            skLineSegment(sketch, "E69.2.0.506", {"start": v(1517.64, 266.7) * mm, "end": v(1517.64, 317.5) * mm});
            skLineSegment(sketch, "E69.2.0.507", {"start": v(1517.64, 520.7) * mm, "end": v(1517.64, 571.5) * mm});
            skLineSegment(sketch, "E69.2.0.508", {"start": v(1314.45, 1092.2) * mm, "end": v(1263.65, 1092.2) * mm});
            skLineSegment(sketch, "E69.2.0.509", {"start": v(1644.64, 774.7) * mm, "end": v(1644.64, 825.5) * mm});
            skLineSegment(sketch, "E69.2.0.510", {"start": v(1644.64, 1028.7) * mm, "end": v(1644.64, 1079.5) * mm});
            skLineSegment(sketch, "E69.2.0.511", {"start": v(1581.14, 266.7) * mm, "end": v(1581.14, 317.5) * mm});
            skLineSegment(sketch, "E69.2.0.512", {"start": v(1581.14, 520.7) * mm, "end": v(1581.14, 571.5) * mm});
            skLineSegment(sketch, "E69.2.0.513", {"start": v(1314.45, 1143) * mm, "end": v(1263.65, 1143) * mm});
            skLineSegment(sketch, "E69.2.0.514", {"start": v(1314.45, 1092.2) * mm, "end": v(1314.45, 1143) * mm});
            skLineSegment(sketch, "E69.2.0.515", {"start": v(1644.64, 266.7) * mm, "end": v(1644.64, 317.5) * mm});
            skLineSegment(sketch, "E69.2.0.516", {"start": v(1644.64, 520.7) * mm, "end": v(1644.64, 571.5) * mm});
            skLineSegment(sketch, "E69.2.0.517", {"start": v(1263.65, 1092.2) * mm, "end": v(1263.65, 1143) * mm});
            skLineSegment(sketch, "E69.2.0.518", {"start": v(1708.13, 266.7) * mm, "end": v(1708.13, 317.5) * mm});
            skLineSegment(sketch, "E69.2.0.519", {"start": v(1708.13, 520.7) * mm, "end": v(1708.13, 571.5) * mm});
            skLineSegment(sketch, "E69.2.0.520", {"start": v(1708.13, 774.7) * mm, "end": v(1708.13, 825.5) * mm});
            skLineSegment(sketch, "E69.2.0.521", {"start": v(1708.13, 1028.7) * mm, "end": v(1708.13, 1079.5) * mm});
            skLineSegment(sketch, "E69.2.0.522", {"start": v(1314.45, 1028.7) * mm, "end": v(1314.45, 1079.5) * mm});
            skLineSegment(sketch, "E69.2.0.523", {"start": v(1314.45, 76.2) * mm, "end": v(1263.65, 76.2) * mm});
            skLineSegment(sketch, "E69.2.0.524", {"start": v(1263.65, 774.7) * mm, "end": v(1263.65, 825.5) * mm});
            skLineSegment(sketch, "E69.2.0.525", {"start": v(1327.15, 774.7) * mm, "end": v(1327.15, 825.5) * mm});
            skLineSegment(sketch, "E69.2.0.526", {"start": v(1327.15, 1028.7) * mm, "end": v(1327.15, 1079.5) * mm});
            skLineSegment(sketch, "E69.2.0.527", {"start": v(1263.65, 266.7) * mm, "end": v(1263.65, 317.5) * mm});
            skLineSegment(sketch, "E69.2.0.528", {"start": v(1263.65, 520.7) * mm, "end": v(1263.65, 571.5) * mm});
            skLineSegment(sketch, "E69.2.0.529", {"start": v(1390.65, 774.7) * mm, "end": v(1390.65, 825.5) * mm});
            skLineSegment(sketch, "E69.2.0.530", {"start": v(1390.65, 1028.7) * mm, "end": v(1390.65, 1079.5) * mm});
            skLineSegment(sketch, "E69.2.0.531", {"start": v(1327.15, 266.7) * mm, "end": v(1327.15, 317.5) * mm});
            skLineSegment(sketch, "E69.2.0.532", {"start": v(1327.15, 520.7) * mm, "end": v(1327.15, 571.5) * mm});
            skLineSegment(sketch, "E69.2.0.533", {"start": v(1454.14, 774.7) * mm, "end": v(1454.14, 825.5) * mm});
            skLineSegment(sketch, "E69.2.0.534", {"start": v(1454.14, 1028.7) * mm, "end": v(1454.14, 1079.5) * mm});
            skLineSegment(sketch, "E69.2.0.535", {"start": v(1390.65, 266.7) * mm, "end": v(1390.65, 317.5) * mm});
            skLineSegment(sketch, "E69.2.0.536", {"start": v(1390.65, 520.7) * mm, "end": v(1390.65, 571.5) * mm});
            skLineSegment(sketch, "E69.2.0.537", {"start": v(1517.64, 774.7) * mm, "end": v(1517.64, 825.5) * mm});
            skLineSegment(sketch, "E69.2.0.538", {"start": v(1517.64, 1028.7) * mm, "end": v(1517.64, 1079.5) * mm});
            skLineSegment(sketch, "E69.2.0.539", {"start": v(1454.14, 266.7) * mm, "end": v(1454.14, 317.5) * mm});
            skLineSegment(sketch, "E69.2.0.540", {"start": v(1454.14, 520.7) * mm, "end": v(1454.14, 571.5) * mm});
            skLineSegment(sketch, "E69.2.0.541", {"start": v(1504.94, 965.2) * mm, "end": v(1454.14, 965.2) * mm});
            skLineSegment(sketch, "E69.2.0.542", {"start": v(1314.45, 965.2) * mm, "end": v(1263.65, 965.2) * mm});
            skLineSegment(sketch, "E69.2.0.543", {"start": v(1314.45, 952.5) * mm, "end": v(1263.65, 952.5) * mm});
            skLineSegment(sketch, "E69.2.0.544", {"start": v(1504.94, 952.5) * mm, "end": v(1454.14, 952.5) * mm});
            skLineSegment(sketch, "E69.2.0.545", {"start": v(1504.94, 584.2) * mm, "end": v(1504.94, 635) * mm});
            skLineSegment(sketch, "E69.2.0.546", {"start": v(1758.93, 584.2) * mm, "end": v(1758.93, 635) * mm});
            skLineSegment(sketch, "E69.2.0.547", {"start": v(1263.65, 584.2) * mm, "end": v(1263.65, 635) * mm});
            skLineSegment(sketch, "E69.2.0.548", {"start": v(1517.64, 584.2) * mm, "end": v(1517.64, 635) * mm});
            skLineSegment(sketch, "E69.2.0.549", {"start": v(1758.93, 76.2) * mm, "end": v(1708.13, 76.2) * mm});
            skLineSegment(sketch, "E69.2.0.550", {"start": v(1568.44, 76.2) * mm, "end": v(1568.44, 127) * mm});
            skLineSegment(sketch, "E69.2.0.551", {"start": v(1377.95, 1028.7) * mm, "end": v(1377.95, 1079.5) * mm});
            skLineSegment(sketch, "E69.2.0.552", {"start": v(1511.3, 1193.8) * mm, "end": v(1511.3, 1155.7) * mm, "construction": true});
            skLineSegment(sketch, "E69.2.0.553", {"start": v(1771.65, 609.6) * mm, "end": v(1803.4, 609.6) * mm, "construction": true});
            skLineSegment(sketch, "E69.2.0.554", {"start": v(1511.3, 25.4) * mm, "end": v(1511.3, 63.5) * mm, "construction": true});
            skLineSegment(sketch, "E69.2.0.555", {"start": v(1219.2, 609.6) * mm, "end": v(1250.95, 609.6) * mm, "construction": true});
            skLineSegment(sketch, "E69.2.0.556", {"start": v(1568.44, 76.2) * mm, "end": v(1517.64, 76.2) * mm});
            skLineSegment(sketch, "E69.2.0.557", {"start": v(1263.65, 1028.7) * mm, "end": v(1263.65, 1079.5) * mm});
            skLineSegment(sketch, "E69.direction1", {"start": v(476.24, 774.7) * mm, "end": v(1060.44, 774.7) * mm, "construction": true});
            skSolve(sketch);
        }
        {
            var Q0;
            Q0 = qSketchRegion(id + "F4", true);
            extrude(context, id + "F5", {"entities" : qUnion([Q0]), "operationType" : NewBodyOperationType.REMOVE, "oppositeDirection" : true, "depth" : 12.7 * mm});
        }
    });
